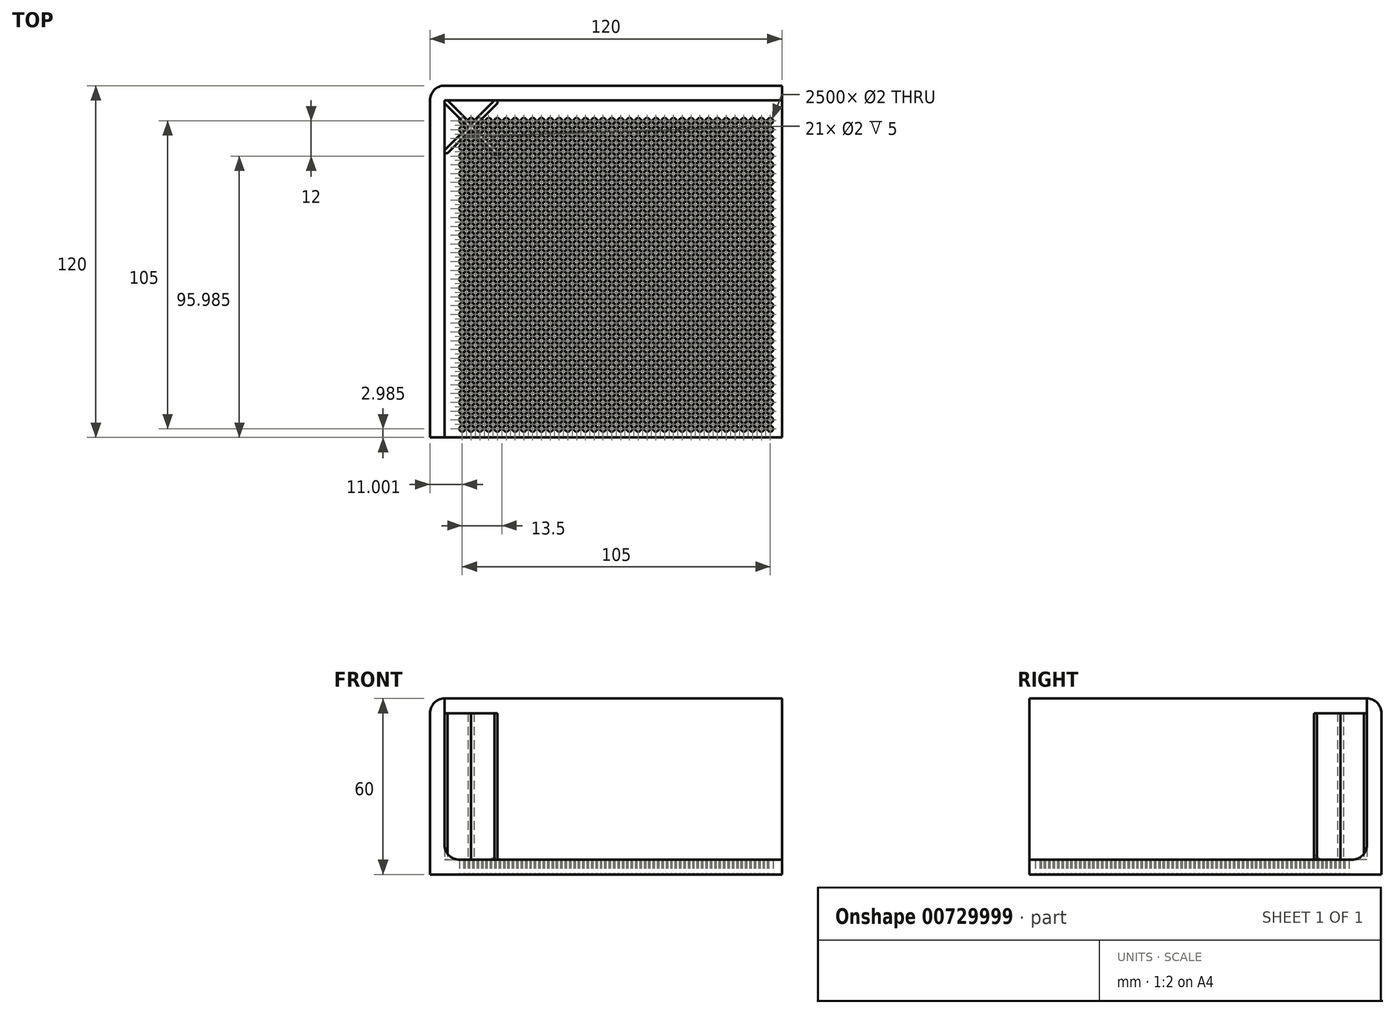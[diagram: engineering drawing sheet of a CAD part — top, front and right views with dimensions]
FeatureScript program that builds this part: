
annotation { "Feature Type Name" : "Feature", "Feature Type Description" : "" }
export const myFeature = defineFeature(function(context is Context, id is Id, definition is map)
    precondition{}
    {
        {
            var Q0;
            Q0=qCreatedBy(makeId("Top.planeOp"),FACE);
            var sketch = newSketch(context, id + "F0", { "sketchPlane" : qUnion([Q0])});
            skLineSegment(sketch, "E0.bottom", {"start": v(-61.1, 44.5) * mm, "end": v(58.9, 44.5) * mm});
            skLineSegment(sketch, "E0.top", {"start": v(-61.1, -75.5) * mm, "end": v(58.9, -75.5) * mm});
            skLineSegment(sketch, "E0.left", {"start": v(-61.1, 44.5) * mm, "end": v(-61.1, -75.5) * mm});
            skLineSegment(sketch, "E0.right", {"start": v(58.9, 44.5) * mm, "end": v(58.9, -75.5) * mm});
            skSolve(sketch);
        }
        {
            var Q0;
            Q0 = qSketchRegion(id + "F0", true);
            extrude(context, id + "F1", {"entities" : qUnion([Q0]), "depth" : 60 * mm, "offsetDistance" : 25 * mm});
        }
        {
            var Q0;
            Q0=makeQuery(id+"F1.opExtrude","CAP_FACE",FACE,{"disambiguationData":[OSD([sQuery(id+"F0.wireOp",EDGE,"E0.bottom"),sQuery(id+"F0.wireOp",EDGE,"E0.top"),sQuery(id+"F0.wireOp",EDGE,"E0.left"),sQuery(id+"F0.wireOp",EDGE,"E0.right")])],"isStart":false});
            var sketch = newSketch(context, id + "F2", { "sketchPlane" : qUnion([Q0])});
            skLineSegment(sketch, "E1.bottom", {"start": v(-56.1, 39.5) * mm, "end": v(58.9, 39.5) * mm});
            skLineSegment(sketch, "E1.top", {"start": v(-56.1, -75.5) * mm, "end": v(58.9, -75.5) * mm});
            skLineSegment(sketch, "E1.left", {"start": v(-56.1, 39.5) * mm, "end": v(-56.1, -75.5) * mm});
            skLineSegment(sketch, "E1.right", {"start": v(58.9, 39.5) * mm, "end": v(58.9, -75.5) * mm});
            skSolve(sketch);
        }
        {
            var Q0;
            Q0 = qSketchRegion(id + "F2", true);
            extrude(context, id + "F3", {"entities" : qUnion([Q0]), "operationType" : NewBodyOperationType.REMOVE, "oppositeDirection" : true, "depth" : 55 * mm, "offsetDistance" : 25 * mm});
        }
        {
            var Q0;
            Q0=makeQuery(id+"F3.boolean.opBoolean","COPY",FACE,{"derivedFrom":makeQuery(id+"F3.opExtrude","CAP_FACE",FACE,{"disambiguationData":[OSD([sQuery(id+"F2.wireOp",EDGE,"E1.bottom"),sQuery(id+"F2.wireOp",EDGE,"E1.top"),sQuery(id+"F2.wireOp",EDGE,"E1.left"),sQuery(id+"F2.wireOp",EDGE,"E1.right")])],"isStart":false})});
            var sketch = newSketch(context, id + "F4", { "sketchPlane" : qUnion([Q0])});
            skLineSegment(sketch, "E2.bottom", {"start": v(-56.1, 39.5) * mm, "end": v(-36.1, 39.5) * mm});
            skLineSegment(sketch, "E2.top", {"start": v(-56.1, 19.5) * mm, "end": v(-36.1, 19.5) * mm});
            skLineSegment(sketch, "E2.left", {"start": v(-56.1, 39.5) * mm, "end": v(-56.1, 19.5) * mm});
            skLineSegment(sketch, "E2.right", {"start": v(-36.1, 39.5) * mm, "end": v(-36.1, 19.5) * mm});
            skLineSegment(sketch, "E3.bottom", {"start": v(-56.1, 39.5) * mm, "end": v(-38.1, 39.5) * mm});
            skLineSegment(sketch, "E3.left", {"start": v(-56.1, 39.5) * mm, "end": v(-56.1, 21.52) * mm});
            skLineSegment(sketch, "E3.right", {"start": v(-38.1, 39.5) * mm, "end": v(-38.1, 21.5) * mm});
            skLineSegment(sketch, "E4", {"start": v(-56.1, 38.5) * mm, "end": v(-48.12, 30.51) * mm});
            skLineSegment(sketch, "E5", {"start": v(-48.12, 30.51) * mm, "end": v(-56.1, 22.52) * mm});
            skLineSegment(sketch, "E6", {"start": v(-55.1, 39.5) * mm, "end": v(-47.1, 31.5) * mm});
            skLineSegment(sketch, "E7", {"start": v(-47.1, 31.5) * mm, "end": v(-39.1, 39.5) * mm});
            skLineSegment(sketch, "E8", {"start": v(-38.1, 38.5) * mm, "end": v(-46.1, 30.5) * mm});
            skLineSegment(sketch, "E9", {"start": v(-46.1, 30.5) * mm, "end": v(-38.1, 22.5) * mm});
            skLineSegment(sketch, "E10", {"start": v(-39.1, 21.5) * mm, "end": v(-47.11, 29.51) * mm});
            skLineSegment(sketch, "E11", {"start": v(-47.11, 29.51) * mm, "end": v(-55.1, 21.52) * mm});
            skLineSegment(sketch, "E12", {"start": v(-56.1, 22.52) * mm, "end": v(-56.1, 21.52) * mm});
            skLineSegment(sketch, "E13", {"start": v(-56.1, 21.52) * mm, "end": v(-38.1, 21.5) * mm});
            skSolve(sketch);
        }
        {
            var Q0;
            Q0=makeQuery(id+"F4.imprint","IMPRINT",FACE,{"disambiguationData":[TD([[makeQuery(id+"F4.imprint","IMPRINT",EDGE,{"derivedFrom":sQuery(id+"F4.wireOp",EDGE,"E2.bottom")}),-1.0]])]});
            extrude(context, id + "F5", {"entities" : qUnion([Q0]), "operationType" : NewBodyOperationType.ADD, "depth" : 50 * mm, "offsetDistance" : 25 * mm});
        }
        {
            var Q0;
            {var subQ9=sQuery(id+"F4.wireOp",EDGE,"E4");Q0=makeQuery(id+"F4.imprint","IMPRINT",FACE,{"disambiguationData":[TD([[makeQuery(id+"F4.imprint","IMPRINT",EDGE,{"derivedFrom":subQ9}),1.0]])]});}
            extrude(context, id + "F6", {"entities" : qUnion([Q0]), "operationType" : NewBodyOperationType.ADD, "depth" : 50 * mm, "offsetDistance" : 25 * mm});
        }
        {
            var Q0;
            Q0=makeQuery(id+"F1.opExtrude","SWEPT_EDGE",EDGE,{"disambiguationData":[OSD([sQuery(id+"F0.wireOp",EDGE,"E0.bottom"),sQuery(id+"F0.wireOp",EDGE,"E0.left")])]});
            var Q1;
            Q1=makeQuery(id+"F1.opExtrude","CAP_EDGE",EDGE,{"disambiguationData":[OSD([sQuery(id+"F0.wireOp",EDGE,"E0.left")])],"isStart":false});
            var Q2;
            Q2=makeQuery(id+"F1.opExtrude","CAP_EDGE",EDGE,{"disambiguationData":[OSD([sQuery(id+"F0.wireOp",EDGE,"E0.bottom")])],"isStart":false});
            fillet(context, id + "F7", {"entities" : qUnion([Q0, Q1, Q2]), "radius" : 5 * mm, "tangentPropagation" : true, "allowEdgeOverflow" : false});
        }
        {
            var Q0;
            {var subQ0=sQuery(id+"F2.wireOp",EDGE,"E1.left");Q0=makeQuery(id+"F5.boolean.opBoolean","SPLIT",EDGE,{"disambiguationData":[TD([makeQuery(id+"F1.opExtrude","SWEPT_FACE",FACE,{"disambiguationData":[OSD([sQuery(id+"F0.wireOp",EDGE,"E0.top")])]})])],"derivedFrom":makeQuery(id+"F3.boolean.opBoolean","COPY",EDGE,{"derivedFrom":makeQuery(id+"F3.opExtrude","CAP_EDGE",EDGE,{"disambiguationData":[OSD([subQ0])],"isStart":false})})});}
            var Q1;
            Q1=makeQuery(id+"F5.opExtrude","CAP_EDGE",EDGE,{"disambiguationData":[OSD([sQuery(id+"F4.wireOp",EDGE,"E2.top")])],"isStart":true});
            var Q2;
            Q2=makeQuery(id+"F5.opExtrude","SWEPT_EDGE",EDGE,{"disambiguationData":[OSD([sQuery(id+"F2.wireOp",EDGE,"E1.left"),sQuery(id+"F4.wireOp",EDGE,"E2.top"),sQuery(id+"F4.wireOp",EDGE,"E2.left")])]});
            var Q3;
            Q3=makeQuery(id+"F5.opExtrude","SWEPT_EDGE",EDGE,{"disambiguationData":[OSD([sQuery(id+"F4.wireOp",EDGE,"E2.top"),sQuery(id+"F4.wireOp",EDGE,"E2.right")])]});
            var Q4;
            Q4=makeQuery(id+"F5.opExtrude","CAP_EDGE",EDGE,{"disambiguationData":[OSD([sQuery(id+"F4.wireOp",EDGE,"E2.right")])],"isStart":true});
            var Q5;
            Q5=makeQuery(id+"F5.opExtrude","SWEPT_EDGE",EDGE,{"disambiguationData":[OSD([sQuery(id+"F2.wireOp",EDGE,"E1.bottom"),sQuery(id+"F4.wireOp",EDGE,"E2.bottom"),sQuery(id+"F4.wireOp",EDGE,"E2.right")])]});
            var Q6;
            {var subQ0=sQuery(id+"F2.wireOp",EDGE,"E1.bottom");Q6=makeQuery(id+"F5.boolean.opBoolean","SPLIT",EDGE,{"disambiguationData":[TD([makeQuery(id+"F1.opExtrude","SWEPT_FACE",FACE,{"disambiguationData":[OSD([sQuery(id+"F0.wireOp",EDGE,"E0.right")])]})])],"derivedFrom":makeQuery(id+"F3.boolean.opBoolean","COPY",EDGE,{"derivedFrom":makeQuery(id+"F3.opExtrude","CAP_EDGE",EDGE,{"disambiguationData":[OSD([subQ0])],"isStart":false})})});}
            fillet(context, id + "F8", {"entities" : qUnion([Q0, Q1, Q2, Q3, Q4, Q5, Q6]), "radius" : 5 * mm, "tangentPropagation" : true, "allowEdgeOverflow" : false});
        }
        {
            var Q0;
            Q0=makeQuery(id+"F6.opExtrude","SWEPT_EDGE",EDGE,{"disambiguationData":[OSD([sQuery(id+"F4.wireOp",EDGE,"E3.left"),sQuery(id+"F4.wireOp",EDGE,"E4")])]});
            var Q1;
            Q1=makeQuery(id+"F6.opExtrude","SWEPT_EDGE",EDGE,{"disambiguationData":[OSD([sQuery(id+"F4.wireOp",EDGE,"E4"),sQuery(id+"F4.wireOp",EDGE,"E5")])]});
            var Q2;
            Q2=makeQuery(id+"F6.opExtrude","SWEPT_EDGE",EDGE,{"disambiguationData":[OSD([sQuery(id+"F4.wireOp",EDGE,"E3.left"),sQuery(id+"F4.wireOp",EDGE,"E5"),sQuery(id+"F4.wireOp",EDGE,"E12")])]});
            var Q3;
            Q3=makeQuery(id+"F6.opExtrude","SWEPT_EDGE",EDGE,{"disambiguationData":[OSD([sQuery(id+"F4.wireOp",EDGE,"E6"),sQuery(id+"F4.wireOp",EDGE,"E7")])]});
            var Q4;
            Q4=makeQuery(id+"F6.opExtrude","SWEPT_EDGE",EDGE,{"disambiguationData":[OSD([sQuery(id+"F4.wireOp",EDGE,"E3.bottom"),sQuery(id+"F4.wireOp",EDGE,"E6")])]});
            var Q5;
            Q5=makeQuery(id+"F6.opExtrude","SWEPT_EDGE",EDGE,{"disambiguationData":[OSD([sQuery(id+"F4.wireOp",EDGE,"E3.bottom"),sQuery(id+"F4.wireOp",EDGE,"E7")])]});
            var Q6;
            Q6=makeQuery(id+"F6.opExtrude","SWEPT_EDGE",EDGE,{"disambiguationData":[OSD([sQuery(id+"F4.wireOp",EDGE,"E8"),sQuery(id+"F4.wireOp",EDGE,"E9")])]});
            var Q7;
            Q7=makeQuery(id+"F6.opExtrude","SWEPT_EDGE",EDGE,{"disambiguationData":[OSD([sQuery(id+"F4.wireOp",EDGE,"E3.right"),sQuery(id+"F4.wireOp",EDGE,"E8")])]});
            var Q8;
            Q8=makeQuery(id+"F6.opExtrude","SWEPT_EDGE",EDGE,{"disambiguationData":[OSD([sQuery(id+"F4.wireOp",EDGE,"E3.right"),sQuery(id+"F4.wireOp",EDGE,"E9")])]});
            var Q9;
            Q9=makeQuery(id+"F6.opExtrude","SWEPT_EDGE",EDGE,{"disambiguationData":[OSD([sQuery(id+"F4.wireOp",EDGE,"E10"),sQuery(id+"F4.wireOp",EDGE,"E11")])]});
            var Q10;
            Q10=makeQuery(id+"F6.opExtrude","SWEPT_EDGE",EDGE,{"disambiguationData":[OSD([sQuery(id+"F4.wireOp",EDGE,"E3.top"),sQuery(id+"F4.wireOp",EDGE,"E10")])]});
            var Q11;
            Q11=makeQuery(id+"F6.opExtrude","SWEPT_EDGE",EDGE,{"disambiguationData":[OSD([sQuery(id+"F4.wireOp",EDGE,"E3.top"),sQuery(id+"F4.wireOp",EDGE,"E11")])]});
            var Q12;
            Q12=makeQuery(id+"F6.opExtrude","CAP_EDGE",EDGE,{"disambiguationData":[OSD([sQuery(id+"F4.wireOp",EDGE,"E11")])],"isStart":true});
            var Q13;
            Q13=makeQuery(id+"F5.opExtrude","CAP_EDGE",EDGE,{"disambiguationData":[OSD([sQuery(id+"F4.wireOp",EDGE,"E3.top")])],"isStart":true});
            var Q14;
            Q14=makeQuery(id+"F6.opExtrude","CAP_EDGE",EDGE,{"disambiguationData":[OSD([sQuery(id+"F4.wireOp",EDGE,"E10")])],"isStart":true});
            var Q15;
            Q15=makeQuery(id+"F6.opExtrude","CAP_EDGE",EDGE,{"disambiguationData":[OSD([sQuery(id+"F4.wireOp",EDGE,"E9")])],"isStart":true});
            var Q16;
            Q16=makeQuery(id+"F6.opExtrude","CAP_EDGE",EDGE,{"disambiguationData":[OSD([sQuery(id+"F4.wireOp",EDGE,"E8")])],"isStart":true});
            var Q17;
            Q17=makeQuery(id+"F5.opExtrude","CAP_EDGE",EDGE,{"disambiguationData":[OSD([sQuery(id+"F4.wireOp",EDGE,"E3.right")])],"isStart":true});
            var Q18;
            Q18=makeQuery(id+"F6.opExtrude","CAP_EDGE",EDGE,{"disambiguationData":[OSD([sQuery(id+"F4.wireOp",EDGE,"E7")])],"isStart":true});
            var Q19;
            {var subQ0=sQuery(id+"F2.wireOp",EDGE,"E1.bottom");var subQ1=sQuery(id+"F2.wireOp",EDGE,"E1.left");Q19=makeQuery(id+"F5.boolean.opBoolean","SPLIT",EDGE,{"disambiguationData":[TD([makeQuery(id+"F3.boolean.opBoolean","COPY",FACE,{"derivedFrom":makeQuery(id+"F3.opExtrude","SWEPT_FACE",FACE,{"disambiguationData":[OSD([subQ1])]})})])],"derivedFrom":makeQuery(id+"F3.boolean.opBoolean","COPY",EDGE,{"derivedFrom":makeQuery(id+"F3.opExtrude","CAP_EDGE",EDGE,{"disambiguationData":[OSD([subQ0])],"isStart":false})})});}
            var Q20;
            Q20=makeQuery(id+"F6.opExtrude","CAP_EDGE",EDGE,{"disambiguationData":[OSD([sQuery(id+"F4.wireOp",EDGE,"E6")])],"isStart":true});
            var Q21;
            {var subQ0=sQuery(id+"F2.wireOp",EDGE,"E1.bottom");var subQ1=sQuery(id+"F2.wireOp",EDGE,"E1.left");Q21=makeQuery(id+"F5.boolean.opBoolean","SPLIT",EDGE,{"disambiguationData":[TD([makeQuery(id+"F3.boolean.opBoolean","COPY",FACE,{"derivedFrom":makeQuery(id+"F3.opExtrude","SWEPT_FACE",FACE,{"disambiguationData":[OSD([subQ0])]})})])],"derivedFrom":makeQuery(id+"F3.boolean.opBoolean","COPY",EDGE,{"derivedFrom":makeQuery(id+"F3.opExtrude","CAP_EDGE",EDGE,{"disambiguationData":[OSD([subQ1])],"isStart":false})})});}
            var Q22;
            Q22=makeQuery(id+"F6.opExtrude","CAP_EDGE",EDGE,{"disambiguationData":[OSD([sQuery(id+"F4.wireOp",EDGE,"E4")])],"isStart":true});
            var Q23;
            Q23=makeQuery(id+"F6.opExtrude","CAP_EDGE",EDGE,{"disambiguationData":[OSD([sQuery(id+"F4.wireOp",EDGE,"E5")])],"isStart":true});
            var Q24;
            Q24=makeQuery(id+"F5.opExtrude","CAP_EDGE",EDGE,{"disambiguationData":[OSD([sQuery(id+"F4.wireOp",EDGE,"E13")])],"isStart":true});
            fillet(context, id + "F9", {"entities" : qUnion([Q0, Q1, Q2, Q3, Q4, Q5, Q6, Q7, Q8, Q9, Q10, Q11, Q12, Q13, Q14, Q15, Q16, Q17, Q18, Q19, Q20, Q21, Q22, Q23, Q24]), "radius" : 1 * mm, "tangentPropagation" : true, "allowEdgeOverflow" : false});
        }
        {
            var Q0;
            Q0=makeQuery(id+"F1.opExtrude","CAP_FACE",FACE,{"disambiguationData":[OSD([sQuery(id+"F0.wireOp",EDGE,"E0.bottom"),sQuery(id+"F0.wireOp",EDGE,"E0.top"),sQuery(id+"F0.wireOp",EDGE,"E0.left"),sQuery(id+"F0.wireOp",EDGE,"E0.right")])],"isStart":true});
            var sketch = newSketch(context, id + "F10", { "sketchPlane" : qUnion([Q0])});
            skLineSegment(sketch, "E14.top", {"start": v(-51.1, -34.5) * mm, "end": v(56.9, -34.5) * mm, "construction": true});
            skLineSegment(sketch, "E14.left", {"start": v(-51.1, 73.5) * mm, "end": v(-51.1, -34.5) * mm, "construction": true});
            skLineSegment(sketch, "E14.right", {"start": v(56.9, 73.5) * mm, "end": v(56.9, -34.5) * mm, "construction": true});
            skLineSegment(sketch, "E15", {"start": v(-51.1, 73.5) * mm, "end": v(56.9, 73.5) * mm, "construction": true});
            skLineSegment(sketch, "E16", {"start": v(-51.1, 72.5) * mm, "end": v(-50.1, 72.5) * mm, "construction": true});
            skLineSegment(sketch, "E17", {"start": v(-50.1, 72.5) * mm, "end": v(-50.1, 73.5) * mm, "construction": true});
            skCircle(sketch, "E18", {"center": v(-50.1, 72.5) * mm, "radius": 1 * mm});
            skLineSegment(sketch, "E19", {"start": v(-51.1, 71) * mm, "end": v(-48.6, 71) * mm, "construction": true});
            skLineSegment(sketch, "E20", {"start": v(-48.6, 71) * mm, "end": v(-48.6, 73.5) * mm, "construction": true});
            skCircle(sketch, "E21", {"center": v(-48.6, 71) * mm, "radius": 1 * mm});
            skCircle(sketch, "E22.1.0.0", {"center": v(-47.1, 72.5) * mm, "radius": 1 * mm});
            skCircle(sketch, "E22.2.0.0", {"center": v(-44.1, 72.5) * mm, "radius": 1 * mm});
            skCircle(sketch, "E22.3.0.0", {"center": v(-41.1, 72.5) * mm, "radius": 1 * mm});
            skCircle(sketch, "E22.4.0.0", {"center": v(-38.1, 72.5) * mm, "radius": 1 * mm});
            skCircle(sketch, "E22.5.0.0", {"center": v(-35.1, 72.5) * mm, "radius": 1 * mm});
            skCircle(sketch, "E22.6.0.0", {"center": v(-32.1, 72.5) * mm, "radius": 1 * mm});
            skCircle(sketch, "E22.7.0.0", {"center": v(-29.1, 72.5) * mm, "radius": 1 * mm});
            skCircle(sketch, "E22.8.0.0", {"center": v(-26.1, 72.5) * mm, "radius": 1 * mm});
            skCircle(sketch, "E22.9.0.0", {"center": v(-23.1, 72.5) * mm, "radius": 1 * mm});
            skCircle(sketch, "E22.10.0.0", {"center": v(-20.1, 72.5) * mm, "radius": 1 * mm});
            skCircle(sketch, "E22.11.0.0", {"center": v(-17.1, 72.5) * mm, "radius": 1 * mm});
            skCircle(sketch, "E22.12.0.0", {"center": v(-14.1, 72.5) * mm, "radius": 1 * mm});
            skCircle(sketch, "E22.13.0.0", {"center": v(-11.1, 72.5) * mm, "radius": 1 * mm});
            skCircle(sketch, "E22.14.0.0", {"center": v(-8.1, 72.5) * mm, "radius": 1 * mm});
            skCircle(sketch, "E22.15.0.0", {"center": v(-5.1, 72.5) * mm, "radius": 1 * mm});
            skCircle(sketch, "E22.16.0.0", {"center": v(-2.1, 72.5) * mm, "radius": 1 * mm});
            skCircle(sketch, "E22.17.0.0", {"center": v(0.9, 72.5) * mm, "radius": 1 * mm});
            skCircle(sketch, "E22.18.0.0", {"center": v(3.9, 72.5) * mm, "radius": 1 * mm});
            skCircle(sketch, "E22.19.0.0", {"center": v(6.9, 72.5) * mm, "radius": 1 * mm});
            skCircle(sketch, "E22.20.0.0", {"center": v(9.9, 72.5) * mm, "radius": 1 * mm});
            skCircle(sketch, "E22.21.0.0", {"center": v(12.9, 72.5) * mm, "radius": 1 * mm});
            skCircle(sketch, "E22.22.0.0", {"center": v(15.9, 72.5) * mm, "radius": 1 * mm});
            skCircle(sketch, "E22.23.0.0", {"center": v(18.9, 72.5) * mm, "radius": 1 * mm});
            skCircle(sketch, "E22.24.0.0", {"center": v(21.9, 72.5) * mm, "radius": 1 * mm});
            skCircle(sketch, "E22.25.0.0", {"center": v(24.9, 72.5) * mm, "radius": 1 * mm});
            skCircle(sketch, "E22.26.0.0", {"center": v(27.9, 72.5) * mm, "radius": 1 * mm});
            skCircle(sketch, "E22.27.0.0", {"center": v(30.9, 72.5) * mm, "radius": 1 * mm});
            skCircle(sketch, "E22.28.0.0", {"center": v(33.9, 72.5) * mm, "radius": 1 * mm});
            skCircle(sketch, "E22.29.0.0", {"center": v(36.9, 72.5) * mm, "radius": 1 * mm});
            skCircle(sketch, "E22.30.0.0", {"center": v(39.9, 72.5) * mm, "radius": 1 * mm});
            skCircle(sketch, "E22.31.0.0", {"center": v(42.9, 72.5) * mm, "radius": 1 * mm});
            skCircle(sketch, "E22.32.0.0", {"center": v(45.9, 72.5) * mm, "radius": 1 * mm});
            skCircle(sketch, "E22.33.0.0", {"center": v(48.9, 72.5) * mm, "radius": 1 * mm});
            skCircle(sketch, "E22.34.0.0", {"center": v(51.9, 72.5) * mm, "radius": 1 * mm});
            skCircle(sketch, "E22.35.0.0", {"center": v(54.9, 72.5) * mm, "radius": 1 * mm});
            skLineSegment(sketch, "E22.direction1", {"start": v(-50.1, 72.5) * mm, "end": v(-47.1, 72.5) * mm, "construction": true});
            skCircle(sketch, "E23.1.0.0", {"center": v(-45.6, 71) * mm, "radius": 1 * mm});
            skCircle(sketch, "E23.2.0.0", {"center": v(-42.6, 71) * mm, "radius": 1 * mm});
            skCircle(sketch, "E23.3.0.0", {"center": v(-39.6, 71) * mm, "radius": 1 * mm});
            skCircle(sketch, "E23.4.0.0", {"center": v(-36.6, 71) * mm, "radius": 1 * mm});
            skCircle(sketch, "E23.5.0.0", {"center": v(-33.6, 71) * mm, "radius": 1 * mm});
            skCircle(sketch, "E23.6.0.0", {"center": v(-30.6, 71) * mm, "radius": 1 * mm});
            skCircle(sketch, "E23.7.0.0", {"center": v(-27.6, 71) * mm, "radius": 1 * mm});
            skCircle(sketch, "E23.8.0.0", {"center": v(-24.6, 71) * mm, "radius": 1 * mm});
            skCircle(sketch, "E23.9.0.0", {"center": v(-21.6, 71) * mm, "radius": 1 * mm});
            skCircle(sketch, "E23.10.0.0", {"center": v(-18.6, 71) * mm, "radius": 1 * mm});
            skCircle(sketch, "E23.11.0.0", {"center": v(-15.6, 71) * mm, "radius": 1 * mm});
            skCircle(sketch, "E23.12.0.0", {"center": v(-12.6, 71) * mm, "radius": 1 * mm});
            skCircle(sketch, "E23.13.0.0", {"center": v(-9.6, 71) * mm, "radius": 1 * mm});
            skCircle(sketch, "E23.14.0.0", {"center": v(-6.6, 71) * mm, "radius": 1 * mm});
            skCircle(sketch, "E23.15.0.0", {"center": v(-3.6, 71) * mm, "radius": 1 * mm});
            skCircle(sketch, "E23.16.0.0", {"center": v(-0.6, 71) * mm, "radius": 1 * mm});
            skCircle(sketch, "E23.17.0.0", {"center": v(2.4, 71) * mm, "radius": 1 * mm});
            skCircle(sketch, "E23.18.0.0", {"center": v(5.4, 71) * mm, "radius": 1 * mm});
            skCircle(sketch, "E23.19.0.0", {"center": v(8.4, 71) * mm, "radius": 1 * mm});
            skCircle(sketch, "E23.20.0.0", {"center": v(11.4, 71) * mm, "radius": 1 * mm});
            skCircle(sketch, "E23.21.0.0", {"center": v(14.4, 71) * mm, "radius": 1 * mm});
            skCircle(sketch, "E23.22.0.0", {"center": v(17.4, 71) * mm, "radius": 1 * mm});
            skCircle(sketch, "E23.23.0.0", {"center": v(20.4, 71) * mm, "radius": 1 * mm});
            skCircle(sketch, "E23.24.0.0", {"center": v(23.4, 71) * mm, "radius": 1 * mm});
            skCircle(sketch, "E23.25.0.0", {"center": v(26.4, 71) * mm, "radius": 1 * mm});
            skCircle(sketch, "E23.26.0.0", {"center": v(29.4, 71) * mm, "radius": 1 * mm});
            skCircle(sketch, "E23.27.0.0", {"center": v(32.4, 71) * mm, "radius": 1 * mm});
            skCircle(sketch, "E23.28.0.0", {"center": v(35.4, 71) * mm, "radius": 1 * mm});
            skCircle(sketch, "E23.29.0.0", {"center": v(38.4, 71) * mm, "radius": 1 * mm});
            skCircle(sketch, "E23.30.0.0", {"center": v(41.4, 71) * mm, "radius": 1 * mm});
            skCircle(sketch, "E23.31.0.0", {"center": v(44.4, 71) * mm, "radius": 1 * mm});
            skCircle(sketch, "E23.32.0.0", {"center": v(47.4, 71) * mm, "radius": 1 * mm});
            skCircle(sketch, "E23.33.0.0", {"center": v(50.4, 71) * mm, "radius": 1 * mm});
            skCircle(sketch, "E23.34.0.0", {"center": v(53.4, 71) * mm, "radius": 1 * mm});
            skLineSegment(sketch, "E23.direction1", {"start": v(-48.6, 71) * mm, "end": v(-45.6, 71) * mm, "construction": true});
            skCircle(sketch, "E24.1.0.0", {"center": v(27.9, 69.5) * mm, "radius": 1 * mm});
            skCircle(sketch, "E24.1.0.1", {"center": v(-32.1, 69.5) * mm, "radius": 1 * mm});
            skCircle(sketch, "E24.1.0.2", {"center": v(36.9, 69.5) * mm, "radius": 1 * mm});
            skCircle(sketch, "E24.1.0.3", {"center": v(3.9, 69.5) * mm, "radius": 1 * mm});
            skCircle(sketch, "E24.1.0.4", {"center": v(54.9, 69.5) * mm, "radius": 1 * mm});
            skCircle(sketch, "E24.1.0.5", {"center": v(53.4, 68) * mm, "radius": 1 * mm});
            skCircle(sketch, "E24.1.0.6", {"center": v(29.4, 68) * mm, "radius": 1 * mm});
            skCircle(sketch, "E24.1.0.7", {"center": v(2.4, 68) * mm, "radius": 1 * mm});
            skCircle(sketch, "E24.1.0.9", {"center": v(18.9, 69.5) * mm, "radius": 1 * mm});
            skCircle(sketch, "E24.1.0.10", {"center": v(-30.6, 68) * mm, "radius": 1 * mm});
            skCircle(sketch, "E24.1.0.12", {"center": v(-44.1, 69.5) * mm, "radius": 1 * mm});
            skCircle(sketch, "E24.1.0.13", {"center": v(30.9, 69.5) * mm, "radius": 1 * mm});
            skCircle(sketch, "E24.1.0.14", {"center": v(-9.6, 68) * mm, "radius": 1 * mm});
            skCircle(sketch, "E24.1.0.16", {"center": v(-14.1, 69.5) * mm, "radius": 1 * mm});
            skCircle(sketch, "E24.1.0.17", {"center": v(-2.1, 69.5) * mm, "radius": 1 * mm});
            skCircle(sketch, "E24.1.0.18", {"center": v(9.9, 69.5) * mm, "radius": 1 * mm});
            skCircle(sketch, "E24.1.0.19", {"center": v(24.9, 69.5) * mm, "radius": 1 * mm});
            skCircle(sketch, "E24.1.0.20", {"center": v(5.4, 68) * mm, "radius": 1 * mm});
            skCircle(sketch, "E24.1.0.21", {"center": v(-23.1, 69.5) * mm, "radius": 1 * mm});
            skCircle(sketch, "E24.1.0.22", {"center": v(-5.1, 69.5) * mm, "radius": 1 * mm});
            skCircle(sketch, "E24.1.0.23", {"center": v(23.4, 68) * mm, "radius": 1 * mm});
            skCircle(sketch, "E24.1.0.24", {"center": v(42.9, 69.5) * mm, "radius": 1 * mm});
            skCircle(sketch, "E24.1.0.25", {"center": v(0.9, 69.5) * mm, "radius": 1 * mm});
            skCircle(sketch, "E24.1.0.26", {"center": v(-36.6, 68) * mm, "radius": 1 * mm});
            skCircle(sketch, "E24.1.0.27", {"center": v(41.4, 68) * mm, "radius": 1 * mm});
            skCircle(sketch, "E24.1.0.28", {"center": v(-12.6, 68) * mm, "radius": 1 * mm});
            skCircle(sketch, "E24.1.0.29", {"center": v(-26.1, 69.5) * mm, "radius": 1 * mm});
            skCircle(sketch, "E24.1.0.30", {"center": v(-8.1, 69.5) * mm, "radius": 1 * mm});
            skCircle(sketch, "E24.1.0.31", {"center": v(-27.6, 68) * mm, "radius": 1 * mm});
            skCircle(sketch, "E24.1.0.32", {"center": v(-29.1, 69.5) * mm, "radius": 1 * mm});
            skCircle(sketch, "E24.1.0.33", {"center": v(15.9, 69.5) * mm, "radius": 1 * mm});
            skCircle(sketch, "E24.1.0.34", {"center": v(-3.6, 68) * mm, "radius": 1 * mm});
            skCircle(sketch, "E24.1.0.35", {"center": v(-11.1, 69.5) * mm, "radius": 1 * mm});
            skCircle(sketch, "E24.1.0.36", {"center": v(44.4, 68) * mm, "radius": 1 * mm});
            skCircle(sketch, "E24.1.0.37", {"center": v(8.4, 68) * mm, "radius": 1 * mm});
            skCircle(sketch, "E24.1.0.38", {"center": v(33.9, 69.5) * mm, "radius": 1 * mm});
            skCircle(sketch, "E24.1.0.39", {"center": v(12.9, 69.5) * mm, "radius": 1 * mm});
            skCircle(sketch, "E24.1.0.40", {"center": v(-38.1, 69.5) * mm, "radius": 1 * mm});
            skCircle(sketch, "E24.1.0.41", {"center": v(-18.6, 68) * mm, "radius": 1 * mm});
            skCircle(sketch, "E24.1.0.42", {"center": v(-17.1, 69.5) * mm, "radius": 1 * mm});
            skCircle(sketch, "E24.1.0.43", {"center": v(48.9, 69.5) * mm, "radius": 1 * mm});
            skCircle(sketch, "E24.1.0.44", {"center": v(35.4, 68) * mm, "radius": 1 * mm});
            skCircle(sketch, "E24.1.0.45", {"center": v(11.4, 68) * mm, "radius": 1 * mm});
            skCircle(sketch, "E24.1.0.46", {"center": v(-24.6, 68) * mm, "radius": 1 * mm});
            skCircle(sketch, "E24.1.0.47", {"center": v(21.9, 69.5) * mm, "radius": 1 * mm});
            skCircle(sketch, "E24.1.0.48", {"center": v(50.4, 68) * mm, "radius": 1 * mm});
            skCircle(sketch, "E24.1.0.49", {"center": v(26.4, 68) * mm, "radius": 1 * mm});
            skCircle(sketch, "E24.1.0.50", {"center": v(20.4, 68) * mm, "radius": 1 * mm});
            skCircle(sketch, "E24.1.0.51", {"center": v(39.9, 69.5) * mm, "radius": 1 * mm});
            skCircle(sketch, "E24.1.0.52", {"center": v(-0.6, 68) * mm, "radius": 1 * mm});
            skCircle(sketch, "E24.1.0.53", {"center": v(47.4, 68) * mm, "radius": 1 * mm});
            skCircle(sketch, "E24.1.0.55", {"center": v(-39.6, 68) * mm, "radius": 1 * mm});
            skCircle(sketch, "E24.1.0.56", {"center": v(38.4, 68) * mm, "radius": 1 * mm});
            skCircle(sketch, "E24.1.0.57", {"center": v(-35.1, 69.5) * mm, "radius": 1 * mm});
            skCircle(sketch, "E24.1.0.58", {"center": v(17.4, 68) * mm, "radius": 1 * mm});
            skCircle(sketch, "E24.1.0.59", {"center": v(51.9, 69.5) * mm, "radius": 1 * mm});
            skCircle(sketch, "E24.1.0.60", {"center": v(-33.6, 68) * mm, "radius": 1 * mm});
            skCircle(sketch, "E24.1.0.62", {"center": v(-15.6, 68) * mm, "radius": 1 * mm});
            skCircle(sketch, "E24.1.0.63", {"center": v(14.4, 68) * mm, "radius": 1 * mm});
            skCircle(sketch, "E24.1.0.64", {"center": v(45.9, 69.5) * mm, "radius": 1 * mm});
            skCircle(sketch, "E24.1.0.65", {"center": v(-6.6, 68) * mm, "radius": 1 * mm});
            skCircle(sketch, "E24.1.0.66", {"center": v(32.4, 68) * mm, "radius": 1 * mm});
            skCircle(sketch, "E24.1.0.67", {"center": v(-21.6, 68) * mm, "radius": 1 * mm});
            skCircle(sketch, "E24.1.0.68", {"center": v(6.9, 69.5) * mm, "radius": 1 * mm});
            skCircle(sketch, "E24.1.0.69", {"center": v(-20.1, 69.5) * mm, "radius": 1 * mm});
            skCircle(sketch, "E24.1.0.70", {"center": v(-41.1, 69.5) * mm, "radius": 1 * mm});
            skCircle(sketch, "E24.1.0.72", {"center": v(-47.1, 69.5) * mm, "radius": 1 * mm});
            skCircle(sketch, "E24.1.0.73", {"center": v(-42.6, 68) * mm, "radius": 1 * mm});
            skCircle(sketch, "E24.1.0.74", {"center": v(-45.6, 68) * mm, "radius": 1 * mm});
            skCircle(sketch, "E24.1.0.75", {"center": v(-48.6, 68) * mm, "radius": 1 * mm});
            skLineSegment(sketch, "E24.1.0.76", {"start": v(-50.1, 69.5) * mm, "end": v(-50.1, 70.5) * mm, "construction": true});
            skCircle(sketch, "E24.1.0.77", {"center": v(-50.1, 69.5) * mm, "radius": 1 * mm});
            skLineSegment(sketch, "E24.1.0.78", {"start": v(-51.1, 69.5) * mm, "end": v(-50.1, 69.5) * mm, "construction": true});
            skLineSegment(sketch, "E24.1.0.79", {"start": v(-51.1, 68) * mm, "end": v(-48.6, 68) * mm, "construction": true});
            skLineSegment(sketch, "E24.1.0.80", {"start": v(-48.6, 68) * mm, "end": v(-48.6, 70.5) * mm, "construction": true});
            skCircle(sketch, "E24.2.0.0", {"center": v(27.9, 66.5) * mm, "radius": 1 * mm});
            skCircle(sketch, "E24.2.0.1", {"center": v(-32.1, 66.5) * mm, "radius": 1 * mm});
            skCircle(sketch, "E24.2.0.2", {"center": v(36.9, 66.5) * mm, "radius": 1 * mm});
            skCircle(sketch, "E24.2.0.3", {"center": v(3.9, 66.5) * mm, "radius": 1 * mm});
            skCircle(sketch, "E24.2.0.4", {"center": v(54.9, 66.5) * mm, "radius": 1 * mm});
            skCircle(sketch, "E24.2.0.5", {"center": v(53.4, 65) * mm, "radius": 1 * mm});
            skCircle(sketch, "E24.2.0.6", {"center": v(29.4, 65) * mm, "radius": 1 * mm});
            skCircle(sketch, "E24.2.0.7", {"center": v(2.4, 65) * mm, "radius": 1 * mm});
            skCircle(sketch, "E24.2.0.9", {"center": v(18.9, 66.5) * mm, "radius": 1 * mm});
            skCircle(sketch, "E24.2.0.10", {"center": v(-30.6, 65) * mm, "radius": 1 * mm});
            skCircle(sketch, "E24.2.0.12", {"center": v(-44.1, 66.5) * mm, "radius": 1 * mm});
            skCircle(sketch, "E24.2.0.13", {"center": v(30.9, 66.5) * mm, "radius": 1 * mm});
            skCircle(sketch, "E24.2.0.14", {"center": v(-9.6, 65) * mm, "radius": 1 * mm});
            skCircle(sketch, "E24.2.0.16", {"center": v(-14.1, 66.5) * mm, "radius": 1 * mm});
            skCircle(sketch, "E24.2.0.17", {"center": v(-2.1, 66.5) * mm, "radius": 1 * mm});
            skCircle(sketch, "E24.2.0.18", {"center": v(9.9, 66.5) * mm, "radius": 1 * mm});
            skCircle(sketch, "E24.2.0.19", {"center": v(24.9, 66.5) * mm, "radius": 1 * mm});
            skCircle(sketch, "E24.2.0.20", {"center": v(5.4, 65) * mm, "radius": 1 * mm});
            skCircle(sketch, "E24.2.0.21", {"center": v(-23.1, 66.5) * mm, "radius": 1 * mm});
            skCircle(sketch, "E24.2.0.22", {"center": v(-5.1, 66.5) * mm, "radius": 1 * mm});
            skCircle(sketch, "E24.2.0.23", {"center": v(23.4, 65) * mm, "radius": 1 * mm});
            skCircle(sketch, "E24.2.0.24", {"center": v(42.9, 66.5) * mm, "radius": 1 * mm});
            skCircle(sketch, "E24.2.0.25", {"center": v(0.9, 66.5) * mm, "radius": 1 * mm});
            skCircle(sketch, "E24.2.0.26", {"center": v(-36.6, 65) * mm, "radius": 1 * mm});
            skCircle(sketch, "E24.2.0.27", {"center": v(41.4, 65) * mm, "radius": 1 * mm});
            skCircle(sketch, "E24.2.0.28", {"center": v(-12.6, 65) * mm, "radius": 1 * mm});
            skCircle(sketch, "E24.2.0.29", {"center": v(-26.1, 66.5) * mm, "radius": 1 * mm});
            skCircle(sketch, "E24.2.0.30", {"center": v(-8.1, 66.5) * mm, "radius": 1 * mm});
            skCircle(sketch, "E24.2.0.31", {"center": v(-27.6, 65) * mm, "radius": 1 * mm});
            skCircle(sketch, "E24.2.0.32", {"center": v(-29.1, 66.5) * mm, "radius": 1 * mm});
            skCircle(sketch, "E24.2.0.33", {"center": v(15.9, 66.5) * mm, "radius": 1 * mm});
            skCircle(sketch, "E24.2.0.34", {"center": v(-3.6, 65) * mm, "radius": 1 * mm});
            skCircle(sketch, "E24.2.0.35", {"center": v(-11.1, 66.5) * mm, "radius": 1 * mm});
            skCircle(sketch, "E24.2.0.36", {"center": v(44.4, 65) * mm, "radius": 1 * mm});
            skCircle(sketch, "E24.2.0.37", {"center": v(8.4, 65) * mm, "radius": 1 * mm});
            skCircle(sketch, "E24.2.0.38", {"center": v(33.9, 66.5) * mm, "radius": 1 * mm});
            skCircle(sketch, "E24.2.0.39", {"center": v(12.9, 66.5) * mm, "radius": 1 * mm});
            skCircle(sketch, "E24.2.0.40", {"center": v(-38.1, 66.5) * mm, "radius": 1 * mm});
            skCircle(sketch, "E24.2.0.41", {"center": v(-18.6, 65) * mm, "radius": 1 * mm});
            skCircle(sketch, "E24.2.0.42", {"center": v(-17.1, 66.5) * mm, "radius": 1 * mm});
            skCircle(sketch, "E24.2.0.43", {"center": v(48.9, 66.5) * mm, "radius": 1 * mm});
            skCircle(sketch, "E24.2.0.44", {"center": v(35.4, 65) * mm, "radius": 1 * mm});
            skCircle(sketch, "E24.2.0.45", {"center": v(11.4, 65) * mm, "radius": 1 * mm});
            skCircle(sketch, "E24.2.0.46", {"center": v(-24.6, 65) * mm, "radius": 1 * mm});
            skCircle(sketch, "E24.2.0.47", {"center": v(21.9, 66.5) * mm, "radius": 1 * mm});
            skCircle(sketch, "E24.2.0.48", {"center": v(50.4, 65) * mm, "radius": 1 * mm});
            skCircle(sketch, "E24.2.0.49", {"center": v(26.4, 65) * mm, "radius": 1 * mm});
            skCircle(sketch, "E24.2.0.50", {"center": v(20.4, 65) * mm, "radius": 1 * mm});
            skCircle(sketch, "E24.2.0.51", {"center": v(39.9, 66.5) * mm, "radius": 1 * mm});
            skCircle(sketch, "E24.2.0.52", {"center": v(-0.6, 65) * mm, "radius": 1 * mm});
            skCircle(sketch, "E24.2.0.53", {"center": v(47.4, 65) * mm, "radius": 1 * mm});
            skCircle(sketch, "E24.2.0.55", {"center": v(-39.6, 65) * mm, "radius": 1 * mm});
            skCircle(sketch, "E24.2.0.56", {"center": v(38.4, 65) * mm, "radius": 1 * mm});
            skCircle(sketch, "E24.2.0.57", {"center": v(-35.1, 66.5) * mm, "radius": 1 * mm});
            skCircle(sketch, "E24.2.0.58", {"center": v(17.4, 65) * mm, "radius": 1 * mm});
            skCircle(sketch, "E24.2.0.59", {"center": v(51.9, 66.5) * mm, "radius": 1 * mm});
            skCircle(sketch, "E24.2.0.60", {"center": v(-33.6, 65) * mm, "radius": 1 * mm});
            skCircle(sketch, "E24.2.0.62", {"center": v(-15.6, 65) * mm, "radius": 1 * mm});
            skCircle(sketch, "E24.2.0.63", {"center": v(14.4, 65) * mm, "radius": 1 * mm});
            skCircle(sketch, "E24.2.0.64", {"center": v(45.9, 66.5) * mm, "radius": 1 * mm});
            skCircle(sketch, "E24.2.0.65", {"center": v(-6.6, 65) * mm, "radius": 1 * mm});
            skCircle(sketch, "E24.2.0.66", {"center": v(32.4, 65) * mm, "radius": 1 * mm});
            skCircle(sketch, "E24.2.0.67", {"center": v(-21.6, 65) * mm, "radius": 1 * mm});
            skCircle(sketch, "E24.2.0.68", {"center": v(6.9, 66.5) * mm, "radius": 1 * mm});
            skCircle(sketch, "E24.2.0.69", {"center": v(-20.1, 66.5) * mm, "radius": 1 * mm});
            skCircle(sketch, "E24.2.0.70", {"center": v(-41.1, 66.5) * mm, "radius": 1 * mm});
            skCircle(sketch, "E24.2.0.72", {"center": v(-47.1, 66.5) * mm, "radius": 1 * mm});
            skCircle(sketch, "E24.2.0.73", {"center": v(-42.6, 65) * mm, "radius": 1 * mm});
            skCircle(sketch, "E24.2.0.74", {"center": v(-45.6, 65) * mm, "radius": 1 * mm});
            skCircle(sketch, "E24.2.0.75", {"center": v(-48.6, 65) * mm, "radius": 1 * mm});
            skLineSegment(sketch, "E24.2.0.76", {"start": v(-50.1, 66.5) * mm, "end": v(-50.1, 67.5) * mm, "construction": true});
            skCircle(sketch, "E24.2.0.77", {"center": v(-50.1, 66.5) * mm, "radius": 1 * mm});
            skLineSegment(sketch, "E24.2.0.78", {"start": v(-51.1, 66.5) * mm, "end": v(-50.1, 66.5) * mm, "construction": true});
            skLineSegment(sketch, "E24.2.0.79", {"start": v(-51.1, 65) * mm, "end": v(-48.6, 65) * mm, "construction": true});
            skLineSegment(sketch, "E24.2.0.80", {"start": v(-48.6, 65) * mm, "end": v(-48.6, 67.5) * mm, "construction": true});
            skLineSegment(sketch, "E24.direction1", {"start": v(-51.1, 71) * mm, "end": v(-51.1, 68) * mm, "construction": true});
            skCircle(sketch, "E25.0.3.0", {"center": v(27.9, 63.5) * mm, "radius": 1 * mm});
            skCircle(sketch, "E25.2.3.0", {"center": v(-32.1, 63.5) * mm, "radius": 1 * mm});
            skCircle(sketch, "E25.4.3.0", {"center": v(36.9, 63.5) * mm, "radius": 1 * mm});
            skCircle(sketch, "E25.6.3.0", {"center": v(3.9, 63.5) * mm, "radius": 1 * mm});
            skCircle(sketch, "E25.8.3.0", {"center": v(54.9, 63.5) * mm, "radius": 1 * mm});
            skCircle(sketch, "E25.10.3.0", {"center": v(53.4, 62) * mm, "radius": 1 * mm});
            skCircle(sketch, "E25.12.3.0", {"center": v(29.4, 62) * mm, "radius": 1 * mm});
            skCircle(sketch, "E25.14.3.0", {"center": v(2.4, 62) * mm, "radius": 1 * mm});
            skCircle(sketch, "E25.18.3.0", {"center": v(18.9, 63.5) * mm, "radius": 1 * mm});
            skCircle(sketch, "E25.20.3.0", {"center": v(-30.6, 62) * mm, "radius": 1 * mm});
            skCircle(sketch, "E25.24.3.0", {"center": v(-44.1, 63.5) * mm, "radius": 1 * mm});
            skCircle(sketch, "E25.26.3.0", {"center": v(30.9, 63.5) * mm, "radius": 1 * mm});
            skCircle(sketch, "E25.28.3.0", {"center": v(-9.6, 62) * mm, "radius": 1 * mm});
            skCircle(sketch, "E25.32.3.0", {"center": v(-14.1, 63.5) * mm, "radius": 1 * mm});
            skCircle(sketch, "E25.34.3.0", {"center": v(-2.1, 63.5) * mm, "radius": 1 * mm});
            skCircle(sketch, "E25.36.3.0", {"center": v(9.9, 63.5) * mm, "radius": 1 * mm});
            skCircle(sketch, "E25.38.3.0", {"center": v(24.9, 63.5) * mm, "radius": 1 * mm});
            skCircle(sketch, "E25.40.3.0", {"center": v(5.4, 62) * mm, "radius": 1 * mm});
            skCircle(sketch, "E25.42.3.0", {"center": v(-23.1, 63.5) * mm, "radius": 1 * mm});
            skCircle(sketch, "E25.44.3.0", {"center": v(-5.1, 63.5) * mm, "radius": 1 * mm});
            skCircle(sketch, "E25.46.3.0", {"center": v(23.4, 62) * mm, "radius": 1 * mm});
            skCircle(sketch, "E25.48.3.0", {"center": v(42.9, 63.5) * mm, "radius": 1 * mm});
            skCircle(sketch, "E25.50.3.0", {"center": v(0.9, 63.5) * mm, "radius": 1 * mm});
            skCircle(sketch, "E25.52.3.0", {"center": v(-36.6, 62) * mm, "radius": 1 * mm});
            skCircle(sketch, "E25.54.3.0", {"center": v(41.4, 62) * mm, "radius": 1 * mm});
            skCircle(sketch, "E25.56.3.0", {"center": v(-12.6, 62) * mm, "radius": 1 * mm});
            skCircle(sketch, "E25.58.3.0", {"center": v(-26.1, 63.5) * mm, "radius": 1 * mm});
            skCircle(sketch, "E25.60.3.0", {"center": v(-8.1, 63.5) * mm, "radius": 1 * mm});
            skCircle(sketch, "E25.62.3.0", {"center": v(-27.6, 62) * mm, "radius": 1 * mm});
            skCircle(sketch, "E25.64.3.0", {"center": v(-29.1, 63.5) * mm, "radius": 1 * mm});
            skCircle(sketch, "E25.66.3.0", {"center": v(15.9, 63.5) * mm, "radius": 1 * mm});
            skCircle(sketch, "E25.68.3.0", {"center": v(-3.6, 62) * mm, "radius": 1 * mm});
            skCircle(sketch, "E25.70.3.0", {"center": v(-11.1, 63.5) * mm, "radius": 1 * mm});
            skCircle(sketch, "E25.72.3.0", {"center": v(44.4, 62) * mm, "radius": 1 * mm});
            skCircle(sketch, "E25.74.3.0", {"center": v(8.4, 62) * mm, "radius": 1 * mm});
            skCircle(sketch, "E25.76.3.0", {"center": v(33.9, 63.5) * mm, "radius": 1 * mm});
            skCircle(sketch, "E25.78.3.0", {"center": v(12.9, 63.5) * mm, "radius": 1 * mm});
            skCircle(sketch, "E25.80.3.0", {"center": v(-38.1, 63.5) * mm, "radius": 1 * mm});
            skCircle(sketch, "E25.82.3.0", {"center": v(-18.6, 62) * mm, "radius": 1 * mm});
            skCircle(sketch, "E25.84.3.0", {"center": v(-17.1, 63.5) * mm, "radius": 1 * mm});
            skCircle(sketch, "E25.86.3.0", {"center": v(48.9, 63.5) * mm, "radius": 1 * mm});
            skCircle(sketch, "E25.88.3.0", {"center": v(35.4, 62) * mm, "radius": 1 * mm});
            skCircle(sketch, "E25.90.3.0", {"center": v(11.4, 62) * mm, "radius": 1 * mm});
            skCircle(sketch, "E25.92.3.0", {"center": v(-24.6, 62) * mm, "radius": 1 * mm});
            skCircle(sketch, "E25.94.3.0", {"center": v(21.9, 63.5) * mm, "radius": 1 * mm});
            skCircle(sketch, "E25.96.3.0", {"center": v(50.4, 62) * mm, "radius": 1 * mm});
            skCircle(sketch, "E25.98.3.0", {"center": v(26.4, 62) * mm, "radius": 1 * mm});
            skCircle(sketch, "E25.100.3.0", {"center": v(20.4, 62) * mm, "radius": 1 * mm});
            skCircle(sketch, "E25.102.3.0", {"center": v(39.9, 63.5) * mm, "radius": 1 * mm});
            skCircle(sketch, "E25.104.3.0", {"center": v(-0.6, 62) * mm, "radius": 1 * mm});
            skCircle(sketch, "E25.106.3.0", {"center": v(47.4, 62) * mm, "radius": 1 * mm});
            skCircle(sketch, "E25.110.3.0", {"center": v(-39.6, 62) * mm, "radius": 1 * mm});
            skCircle(sketch, "E25.112.3.0", {"center": v(38.4, 62) * mm, "radius": 1 * mm});
            skCircle(sketch, "E25.114.3.0", {"center": v(-35.1, 63.5) * mm, "radius": 1 * mm});
            skCircle(sketch, "E25.116.3.0", {"center": v(17.4, 62) * mm, "radius": 1 * mm});
            skCircle(sketch, "E25.118.3.0", {"center": v(51.9, 63.5) * mm, "radius": 1 * mm});
            skCircle(sketch, "E25.120.3.0", {"center": v(-33.6, 62) * mm, "radius": 1 * mm});
            skCircle(sketch, "E25.124.3.0", {"center": v(-15.6, 62) * mm, "radius": 1 * mm});
            skCircle(sketch, "E25.126.3.0", {"center": v(14.4, 62) * mm, "radius": 1 * mm});
            skCircle(sketch, "E25.128.3.0", {"center": v(45.9, 63.5) * mm, "radius": 1 * mm});
            skCircle(sketch, "E25.130.3.0", {"center": v(-6.6, 62) * mm, "radius": 1 * mm});
            skCircle(sketch, "E25.132.3.0", {"center": v(32.4, 62) * mm, "radius": 1 * mm});
            skCircle(sketch, "E25.134.3.0", {"center": v(-21.6, 62) * mm, "radius": 1 * mm});
            skCircle(sketch, "E25.136.3.0", {"center": v(6.9, 63.5) * mm, "radius": 1 * mm});
            skCircle(sketch, "E25.138.3.0", {"center": v(-20.1, 63.5) * mm, "radius": 1 * mm});
            skCircle(sketch, "E25.140.3.0", {"center": v(-41.1, 63.5) * mm, "radius": 1 * mm});
            skCircle(sketch, "E25.144.3.0", {"center": v(-47.1, 63.5) * mm, "radius": 1 * mm});
            skCircle(sketch, "E25.146.3.0", {"center": v(-42.6, 62) * mm, "radius": 1 * mm});
            skCircle(sketch, "E25.148.3.0", {"center": v(-45.6, 62) * mm, "radius": 1 * mm});
            skCircle(sketch, "E25.150.3.0", {"center": v(-48.6, 62) * mm, "radius": 1 * mm});
            skLineSegment(sketch, "E25.152.3.0", {"start": v(-50.1, 63.5) * mm, "end": v(-50.1, 64.5) * mm, "construction": true});
            skCircle(sketch, "E25.155.3.0", {"center": v(-50.1, 63.5) * mm, "radius": 1 * mm});
            skLineSegment(sketch, "E25.157.3.0", {"start": v(-51.1, 63.5) * mm, "end": v(-50.1, 63.5) * mm, "construction": true});
            skLineSegment(sketch, "E25.160.3.0", {"start": v(-51.1, 62) * mm, "end": v(-48.6, 62) * mm, "construction": true});
            skLineSegment(sketch, "E25.163.3.0", {"start": v(-48.6, 62) * mm, "end": v(-48.6, 64.5) * mm, "construction": true});
            skCircle(sketch, "E25.0.4.0", {"center": v(27.9, 60.5) * mm, "radius": 1 * mm});
            skCircle(sketch, "E25.2.4.0", {"center": v(-32.1, 60.5) * mm, "radius": 1 * mm});
            skCircle(sketch, "E25.4.4.0", {"center": v(36.9, 60.5) * mm, "radius": 1 * mm});
            skCircle(sketch, "E25.6.4.0", {"center": v(3.9, 60.5) * mm, "radius": 1 * mm});
            skCircle(sketch, "E25.8.4.0", {"center": v(54.9, 60.5) * mm, "radius": 1 * mm});
            skCircle(sketch, "E25.10.4.0", {"center": v(53.4, 59) * mm, "radius": 1 * mm});
            skCircle(sketch, "E25.12.4.0", {"center": v(29.4, 59) * mm, "radius": 1 * mm});
            skCircle(sketch, "E25.14.4.0", {"center": v(2.4, 59) * mm, "radius": 1 * mm});
            skCircle(sketch, "E25.18.4.0", {"center": v(18.9, 60.5) * mm, "radius": 1 * mm});
            skCircle(sketch, "E25.20.4.0", {"center": v(-30.6, 59) * mm, "radius": 1 * mm});
            skCircle(sketch, "E25.24.4.0", {"center": v(-44.1, 60.5) * mm, "radius": 1 * mm});
            skCircle(sketch, "E25.26.4.0", {"center": v(30.9, 60.5) * mm, "radius": 1 * mm});
            skCircle(sketch, "E25.28.4.0", {"center": v(-9.6, 59) * mm, "radius": 1 * mm});
            skCircle(sketch, "E25.32.4.0", {"center": v(-14.1, 60.5) * mm, "radius": 1 * mm});
            skCircle(sketch, "E25.34.4.0", {"center": v(-2.1, 60.5) * mm, "radius": 1 * mm});
            skCircle(sketch, "E25.36.4.0", {"center": v(9.9, 60.5) * mm, "radius": 1 * mm});
            skCircle(sketch, "E25.38.4.0", {"center": v(24.9, 60.5) * mm, "radius": 1 * mm});
            skCircle(sketch, "E25.40.4.0", {"center": v(5.4, 59) * mm, "radius": 1 * mm});
            skCircle(sketch, "E25.42.4.0", {"center": v(-23.1, 60.5) * mm, "radius": 1 * mm});
            skCircle(sketch, "E25.44.4.0", {"center": v(-5.1, 60.5) * mm, "radius": 1 * mm});
            skCircle(sketch, "E25.46.4.0", {"center": v(23.4, 59) * mm, "radius": 1 * mm});
            skCircle(sketch, "E25.48.4.0", {"center": v(42.9, 60.5) * mm, "radius": 1 * mm});
            skCircle(sketch, "E25.50.4.0", {"center": v(0.9, 60.5) * mm, "radius": 1 * mm});
            skCircle(sketch, "E25.52.4.0", {"center": v(-36.6, 59) * mm, "radius": 1 * mm});
            skCircle(sketch, "E25.54.4.0", {"center": v(41.4, 59) * mm, "radius": 1 * mm});
            skCircle(sketch, "E25.56.4.0", {"center": v(-12.6, 59) * mm, "radius": 1 * mm});
            skCircle(sketch, "E25.58.4.0", {"center": v(-26.1, 60.5) * mm, "radius": 1 * mm});
            skCircle(sketch, "E25.60.4.0", {"center": v(-8.1, 60.5) * mm, "radius": 1 * mm});
            skCircle(sketch, "E25.62.4.0", {"center": v(-27.6, 59) * mm, "radius": 1 * mm});
            skCircle(sketch, "E25.64.4.0", {"center": v(-29.1, 60.5) * mm, "radius": 1 * mm});
            skCircle(sketch, "E25.66.4.0", {"center": v(15.9, 60.5) * mm, "radius": 1 * mm});
            skCircle(sketch, "E25.68.4.0", {"center": v(-3.6, 59) * mm, "radius": 1 * mm});
            skCircle(sketch, "E25.70.4.0", {"center": v(-11.1, 60.5) * mm, "radius": 1 * mm});
            skCircle(sketch, "E25.72.4.0", {"center": v(44.4, 59) * mm, "radius": 1 * mm});
            skCircle(sketch, "E25.74.4.0", {"center": v(8.4, 59) * mm, "radius": 1 * mm});
            skCircle(sketch, "E25.76.4.0", {"center": v(33.9, 60.5) * mm, "radius": 1 * mm});
            skCircle(sketch, "E25.78.4.0", {"center": v(12.9, 60.5) * mm, "radius": 1 * mm});
            skCircle(sketch, "E25.80.4.0", {"center": v(-38.1, 60.5) * mm, "radius": 1 * mm});
            skCircle(sketch, "E25.82.4.0", {"center": v(-18.6, 59) * mm, "radius": 1 * mm});
            skCircle(sketch, "E25.84.4.0", {"center": v(-17.1, 60.5) * mm, "radius": 1 * mm});
            skCircle(sketch, "E25.86.4.0", {"center": v(48.9, 60.5) * mm, "radius": 1 * mm});
            skCircle(sketch, "E25.88.4.0", {"center": v(35.4, 59) * mm, "radius": 1 * mm});
            skCircle(sketch, "E25.90.4.0", {"center": v(11.4, 59) * mm, "radius": 1 * mm});
            skCircle(sketch, "E25.92.4.0", {"center": v(-24.6, 59) * mm, "radius": 1 * mm});
            skCircle(sketch, "E25.94.4.0", {"center": v(21.9, 60.5) * mm, "radius": 1 * mm});
            skCircle(sketch, "E25.96.4.0", {"center": v(50.4, 59) * mm, "radius": 1 * mm});
            skCircle(sketch, "E25.98.4.0", {"center": v(26.4, 59) * mm, "radius": 1 * mm});
            skCircle(sketch, "E25.100.4.0", {"center": v(20.4, 59) * mm, "radius": 1 * mm});
            skCircle(sketch, "E25.102.4.0", {"center": v(39.9, 60.5) * mm, "radius": 1 * mm});
            skCircle(sketch, "E25.104.4.0", {"center": v(-0.6, 59) * mm, "radius": 1 * mm});
            skCircle(sketch, "E25.106.4.0", {"center": v(47.4, 59) * mm, "radius": 1 * mm});
            skCircle(sketch, "E25.110.4.0", {"center": v(-39.6, 59) * mm, "radius": 1 * mm});
            skCircle(sketch, "E25.112.4.0", {"center": v(38.4, 59) * mm, "radius": 1 * mm});
            skCircle(sketch, "E25.114.4.0", {"center": v(-35.1, 60.5) * mm, "radius": 1 * mm});
            skCircle(sketch, "E25.116.4.0", {"center": v(17.4, 59) * mm, "radius": 1 * mm});
            skCircle(sketch, "E25.118.4.0", {"center": v(51.9, 60.5) * mm, "radius": 1 * mm});
            skCircle(sketch, "E25.120.4.0", {"center": v(-33.6, 59) * mm, "radius": 1 * mm});
            skCircle(sketch, "E25.124.4.0", {"center": v(-15.6, 59) * mm, "radius": 1 * mm});
            skCircle(sketch, "E25.126.4.0", {"center": v(14.4, 59) * mm, "radius": 1 * mm});
            skCircle(sketch, "E25.128.4.0", {"center": v(45.9, 60.5) * mm, "radius": 1 * mm});
            skCircle(sketch, "E25.130.4.0", {"center": v(-6.6, 59) * mm, "radius": 1 * mm});
            skCircle(sketch, "E25.132.4.0", {"center": v(32.4, 59) * mm, "radius": 1 * mm});
            skCircle(sketch, "E25.134.4.0", {"center": v(-21.6, 59) * mm, "radius": 1 * mm});
            skCircle(sketch, "E25.136.4.0", {"center": v(6.9, 60.5) * mm, "radius": 1 * mm});
            skCircle(sketch, "E25.138.4.0", {"center": v(-20.1, 60.5) * mm, "radius": 1 * mm});
            skCircle(sketch, "E25.140.4.0", {"center": v(-41.1, 60.5) * mm, "radius": 1 * mm});
            skCircle(sketch, "E25.144.4.0", {"center": v(-47.1, 60.5) * mm, "radius": 1 * mm});
            skCircle(sketch, "E25.146.4.0", {"center": v(-42.6, 59) * mm, "radius": 1 * mm});
            skCircle(sketch, "E25.148.4.0", {"center": v(-45.6, 59) * mm, "radius": 1 * mm});
            skCircle(sketch, "E25.150.4.0", {"center": v(-48.6, 59) * mm, "radius": 1 * mm});
            skLineSegment(sketch, "E25.152.4.0", {"start": v(-50.1, 60.5) * mm, "end": v(-50.1, 61.5) * mm, "construction": true});
            skCircle(sketch, "E25.155.4.0", {"center": v(-50.1, 60.5) * mm, "radius": 1 * mm});
            skLineSegment(sketch, "E25.157.4.0", {"start": v(-51.1, 60.5) * mm, "end": v(-50.1, 60.5) * mm, "construction": true});
            skLineSegment(sketch, "E25.160.4.0", {"start": v(-51.1, 59) * mm, "end": v(-48.6, 59) * mm, "construction": true});
            skLineSegment(sketch, "E25.163.4.0", {"start": v(-48.6, 59) * mm, "end": v(-48.6, 61.5) * mm, "construction": true});
            skCircle(sketch, "E25.0.5.0", {"center": v(27.9, 57.5) * mm, "radius": 1 * mm});
            skCircle(sketch, "E25.2.5.0", {"center": v(-32.1, 57.5) * mm, "radius": 1 * mm});
            skCircle(sketch, "E25.4.5.0", {"center": v(36.9, 57.5) * mm, "radius": 1 * mm});
            skCircle(sketch, "E25.6.5.0", {"center": v(3.9, 57.5) * mm, "radius": 1 * mm});
            skCircle(sketch, "E25.8.5.0", {"center": v(54.9, 57.5) * mm, "radius": 1 * mm});
            skCircle(sketch, "E25.10.5.0", {"center": v(53.4, 56) * mm, "radius": 1 * mm});
            skCircle(sketch, "E25.12.5.0", {"center": v(29.4, 56) * mm, "radius": 1 * mm});
            skCircle(sketch, "E25.14.5.0", {"center": v(2.4, 56) * mm, "radius": 1 * mm});
            skCircle(sketch, "E25.18.5.0", {"center": v(18.9, 57.5) * mm, "radius": 1 * mm});
            skCircle(sketch, "E25.20.5.0", {"center": v(-30.6, 56) * mm, "radius": 1 * mm});
            skCircle(sketch, "E25.24.5.0", {"center": v(-44.1, 57.5) * mm, "radius": 1 * mm});
            skCircle(sketch, "E25.26.5.0", {"center": v(30.9, 57.5) * mm, "radius": 1 * mm});
            skCircle(sketch, "E25.28.5.0", {"center": v(-9.6, 56) * mm, "radius": 1 * mm});
            skCircle(sketch, "E25.32.5.0", {"center": v(-14.1, 57.5) * mm, "radius": 1 * mm});
            skCircle(sketch, "E25.34.5.0", {"center": v(-2.1, 57.5) * mm, "radius": 1 * mm});
            skCircle(sketch, "E25.36.5.0", {"center": v(9.9, 57.5) * mm, "radius": 1 * mm});
            skCircle(sketch, "E25.38.5.0", {"center": v(24.9, 57.5) * mm, "radius": 1 * mm});
            skCircle(sketch, "E25.40.5.0", {"center": v(5.4, 56) * mm, "radius": 1 * mm});
            skCircle(sketch, "E25.42.5.0", {"center": v(-23.1, 57.5) * mm, "radius": 1 * mm});
            skCircle(sketch, "E25.44.5.0", {"center": v(-5.1, 57.5) * mm, "radius": 1 * mm});
            skCircle(sketch, "E25.46.5.0", {"center": v(23.4, 56) * mm, "radius": 1 * mm});
            skCircle(sketch, "E25.48.5.0", {"center": v(42.9, 57.5) * mm, "radius": 1 * mm});
            skCircle(sketch, "E25.50.5.0", {"center": v(0.9, 57.5) * mm, "radius": 1 * mm});
            skCircle(sketch, "E25.52.5.0", {"center": v(-36.6, 56) * mm, "radius": 1 * mm});
            skCircle(sketch, "E25.54.5.0", {"center": v(41.4, 56) * mm, "radius": 1 * mm});
            skCircle(sketch, "E25.56.5.0", {"center": v(-12.6, 56) * mm, "radius": 1 * mm});
            skCircle(sketch, "E25.58.5.0", {"center": v(-26.1, 57.5) * mm, "radius": 1 * mm});
            skCircle(sketch, "E25.60.5.0", {"center": v(-8.1, 57.5) * mm, "radius": 1 * mm});
            skCircle(sketch, "E25.62.5.0", {"center": v(-27.6, 56) * mm, "radius": 1 * mm});
            skCircle(sketch, "E25.64.5.0", {"center": v(-29.1, 57.5) * mm, "radius": 1 * mm});
            skCircle(sketch, "E25.66.5.0", {"center": v(15.9, 57.5) * mm, "radius": 1 * mm});
            skCircle(sketch, "E25.68.5.0", {"center": v(-3.6, 56) * mm, "radius": 1 * mm});
            skCircle(sketch, "E25.70.5.0", {"center": v(-11.1, 57.5) * mm, "radius": 1 * mm});
            skCircle(sketch, "E25.72.5.0", {"center": v(44.4, 56) * mm, "radius": 1 * mm});
            skCircle(sketch, "E25.74.5.0", {"center": v(8.4, 56) * mm, "radius": 1 * mm});
            skCircle(sketch, "E25.76.5.0", {"center": v(33.9, 57.5) * mm, "radius": 1 * mm});
            skCircle(sketch, "E25.78.5.0", {"center": v(12.9, 57.5) * mm, "radius": 1 * mm});
            skCircle(sketch, "E25.80.5.0", {"center": v(-38.1, 57.5) * mm, "radius": 1 * mm});
            skCircle(sketch, "E25.82.5.0", {"center": v(-18.6, 56) * mm, "radius": 1 * mm});
            skCircle(sketch, "E25.84.5.0", {"center": v(-17.1, 57.5) * mm, "radius": 1 * mm});
            skCircle(sketch, "E25.86.5.0", {"center": v(48.9, 57.5) * mm, "radius": 1 * mm});
            skCircle(sketch, "E25.88.5.0", {"center": v(35.4, 56) * mm, "radius": 1 * mm});
            skCircle(sketch, "E25.90.5.0", {"center": v(11.4, 56) * mm, "radius": 1 * mm});
            skCircle(sketch, "E25.92.5.0", {"center": v(-24.6, 56) * mm, "radius": 1 * mm});
            skCircle(sketch, "E25.94.5.0", {"center": v(21.9, 57.5) * mm, "radius": 1 * mm});
            skCircle(sketch, "E25.96.5.0", {"center": v(50.4, 56) * mm, "radius": 1 * mm});
            skCircle(sketch, "E25.98.5.0", {"center": v(26.4, 56) * mm, "radius": 1 * mm});
            skCircle(sketch, "E25.100.5.0", {"center": v(20.4, 56) * mm, "radius": 1 * mm});
            skCircle(sketch, "E25.102.5.0", {"center": v(39.9, 57.5) * mm, "radius": 1 * mm});
            skCircle(sketch, "E25.104.5.0", {"center": v(-0.6, 56) * mm, "radius": 1 * mm});
            skCircle(sketch, "E25.106.5.0", {"center": v(47.4, 56) * mm, "radius": 1 * mm});
            skCircle(sketch, "E25.110.5.0", {"center": v(-39.6, 56) * mm, "radius": 1 * mm});
            skCircle(sketch, "E25.112.5.0", {"center": v(38.4, 56) * mm, "radius": 1 * mm});
            skCircle(sketch, "E25.114.5.0", {"center": v(-35.1, 57.5) * mm, "radius": 1 * mm});
            skCircle(sketch, "E25.116.5.0", {"center": v(17.4, 56) * mm, "radius": 1 * mm});
            skCircle(sketch, "E25.118.5.0", {"center": v(51.9, 57.5) * mm, "radius": 1 * mm});
            skCircle(sketch, "E25.120.5.0", {"center": v(-33.6, 56) * mm, "radius": 1 * mm});
            skCircle(sketch, "E25.124.5.0", {"center": v(-15.6, 56) * mm, "radius": 1 * mm});
            skCircle(sketch, "E25.126.5.0", {"center": v(14.4, 56) * mm, "radius": 1 * mm});
            skCircle(sketch, "E25.128.5.0", {"center": v(45.9, 57.5) * mm, "radius": 1 * mm});
            skCircle(sketch, "E25.130.5.0", {"center": v(-6.6, 56) * mm, "radius": 1 * mm});
            skCircle(sketch, "E25.132.5.0", {"center": v(32.4, 56) * mm, "radius": 1 * mm});
            skCircle(sketch, "E25.134.5.0", {"center": v(-21.6, 56) * mm, "radius": 1 * mm});
            skCircle(sketch, "E25.136.5.0", {"center": v(6.9, 57.5) * mm, "radius": 1 * mm});
            skCircle(sketch, "E25.138.5.0", {"center": v(-20.1, 57.5) * mm, "radius": 1 * mm});
            skCircle(sketch, "E25.140.5.0", {"center": v(-41.1, 57.5) * mm, "radius": 1 * mm});
            skCircle(sketch, "E25.144.5.0", {"center": v(-47.1, 57.5) * mm, "radius": 1 * mm});
            skCircle(sketch, "E25.146.5.0", {"center": v(-42.6, 56) * mm, "radius": 1 * mm});
            skCircle(sketch, "E25.148.5.0", {"center": v(-45.6, 56) * mm, "radius": 1 * mm});
            skCircle(sketch, "E25.150.5.0", {"center": v(-48.6, 56) * mm, "radius": 1 * mm});
            skLineSegment(sketch, "E25.152.5.0", {"start": v(-50.1, 57.5) * mm, "end": v(-50.1, 58.5) * mm, "construction": true});
            skCircle(sketch, "E25.155.5.0", {"center": v(-50.1, 57.5) * mm, "radius": 1 * mm});
            skLineSegment(sketch, "E25.157.5.0", {"start": v(-51.1, 57.5) * mm, "end": v(-50.1, 57.5) * mm, "construction": true});
            skLineSegment(sketch, "E25.160.5.0", {"start": v(-51.1, 56) * mm, "end": v(-48.6, 56) * mm, "construction": true});
            skLineSegment(sketch, "E25.163.5.0", {"start": v(-48.6, 56) * mm, "end": v(-48.6, 58.5) * mm, "construction": true});
            skCircle(sketch, "E25.0.6.0", {"center": v(27.9, 54.5) * mm, "radius": 1 * mm});
            skCircle(sketch, "E25.2.6.0", {"center": v(-32.1, 54.5) * mm, "radius": 1 * mm});
            skCircle(sketch, "E25.4.6.0", {"center": v(36.9, 54.5) * mm, "radius": 1 * mm});
            skCircle(sketch, "E25.6.6.0", {"center": v(3.9, 54.5) * mm, "radius": 1 * mm});
            skCircle(sketch, "E25.8.6.0", {"center": v(54.9, 54.5) * mm, "radius": 1 * mm});
            skCircle(sketch, "E25.10.6.0", {"center": v(53.4, 53) * mm, "radius": 1 * mm});
            skCircle(sketch, "E25.12.6.0", {"center": v(29.4, 53) * mm, "radius": 1 * mm});
            skCircle(sketch, "E25.14.6.0", {"center": v(2.4, 53) * mm, "radius": 1 * mm});
            skCircle(sketch, "E25.18.6.0", {"center": v(18.9, 54.5) * mm, "radius": 1 * mm});
            skCircle(sketch, "E25.20.6.0", {"center": v(-30.6, 53) * mm, "radius": 1 * mm});
            skCircle(sketch, "E25.24.6.0", {"center": v(-44.1, 54.5) * mm, "radius": 1 * mm});
            skCircle(sketch, "E25.26.6.0", {"center": v(30.9, 54.5) * mm, "radius": 1 * mm});
            skCircle(sketch, "E25.28.6.0", {"center": v(-9.6, 53) * mm, "radius": 1 * mm});
            skCircle(sketch, "E25.32.6.0", {"center": v(-14.1, 54.5) * mm, "radius": 1 * mm});
            skCircle(sketch, "E25.34.6.0", {"center": v(-2.1, 54.5) * mm, "radius": 1 * mm});
            skCircle(sketch, "E25.36.6.0", {"center": v(9.9, 54.5) * mm, "radius": 1 * mm});
            skCircle(sketch, "E25.38.6.0", {"center": v(24.9, 54.5) * mm, "radius": 1 * mm});
            skCircle(sketch, "E25.40.6.0", {"center": v(5.4, 53) * mm, "radius": 1 * mm});
            skCircle(sketch, "E25.42.6.0", {"center": v(-23.1, 54.5) * mm, "radius": 1 * mm});
            skCircle(sketch, "E25.44.6.0", {"center": v(-5.1, 54.5) * mm, "radius": 1 * mm});
            skCircle(sketch, "E25.46.6.0", {"center": v(23.4, 53) * mm, "radius": 1 * mm});
            skCircle(sketch, "E25.48.6.0", {"center": v(42.9, 54.5) * mm, "radius": 1 * mm});
            skCircle(sketch, "E25.50.6.0", {"center": v(0.9, 54.5) * mm, "radius": 1 * mm});
            skCircle(sketch, "E25.52.6.0", {"center": v(-36.6, 53) * mm, "radius": 1 * mm});
            skCircle(sketch, "E25.54.6.0", {"center": v(41.4, 53) * mm, "radius": 1 * mm});
            skCircle(sketch, "E25.56.6.0", {"center": v(-12.6, 53) * mm, "radius": 1 * mm});
            skCircle(sketch, "E25.58.6.0", {"center": v(-26.1, 54.5) * mm, "radius": 1 * mm});
            skCircle(sketch, "E25.60.6.0", {"center": v(-8.1, 54.5) * mm, "radius": 1 * mm});
            skCircle(sketch, "E25.62.6.0", {"center": v(-27.6, 53) * mm, "radius": 1 * mm});
            skCircle(sketch, "E25.64.6.0", {"center": v(-29.1, 54.5) * mm, "radius": 1 * mm});
            skCircle(sketch, "E25.66.6.0", {"center": v(15.9, 54.5) * mm, "radius": 1 * mm});
            skCircle(sketch, "E25.68.6.0", {"center": v(-3.6, 53) * mm, "radius": 1 * mm});
            skCircle(sketch, "E25.70.6.0", {"center": v(-11.1, 54.5) * mm, "radius": 1 * mm});
            skCircle(sketch, "E25.72.6.0", {"center": v(44.4, 53) * mm, "radius": 1 * mm});
            skCircle(sketch, "E25.74.6.0", {"center": v(8.4, 53) * mm, "radius": 1 * mm});
            skCircle(sketch, "E25.76.6.0", {"center": v(33.9, 54.5) * mm, "radius": 1 * mm});
            skCircle(sketch, "E25.78.6.0", {"center": v(12.9, 54.5) * mm, "radius": 1 * mm});
            skCircle(sketch, "E25.80.6.0", {"center": v(-38.1, 54.5) * mm, "radius": 1 * mm});
            skCircle(sketch, "E25.82.6.0", {"center": v(-18.6, 53) * mm, "radius": 1 * mm});
            skCircle(sketch, "E25.84.6.0", {"center": v(-17.1, 54.5) * mm, "radius": 1 * mm});
            skCircle(sketch, "E25.86.6.0", {"center": v(48.9, 54.5) * mm, "radius": 1 * mm});
            skCircle(sketch, "E25.88.6.0", {"center": v(35.4, 53) * mm, "radius": 1 * mm});
            skCircle(sketch, "E25.90.6.0", {"center": v(11.4, 53) * mm, "radius": 1 * mm});
            skCircle(sketch, "E25.92.6.0", {"center": v(-24.6, 53) * mm, "radius": 1 * mm});
            skCircle(sketch, "E25.94.6.0", {"center": v(21.9, 54.5) * mm, "radius": 1 * mm});
            skCircle(sketch, "E25.96.6.0", {"center": v(50.4, 53) * mm, "radius": 1 * mm});
            skCircle(sketch, "E25.98.6.0", {"center": v(26.4, 53) * mm, "radius": 1 * mm});
            skCircle(sketch, "E25.100.6.0", {"center": v(20.4, 53) * mm, "radius": 1 * mm});
            skCircle(sketch, "E25.102.6.0", {"center": v(39.9, 54.5) * mm, "radius": 1 * mm});
            skCircle(sketch, "E25.104.6.0", {"center": v(-0.6, 53) * mm, "radius": 1 * mm});
            skCircle(sketch, "E25.106.6.0", {"center": v(47.4, 53) * mm, "radius": 1 * mm});
            skCircle(sketch, "E25.110.6.0", {"center": v(-39.6, 53) * mm, "radius": 1 * mm});
            skCircle(sketch, "E25.112.6.0", {"center": v(38.4, 53) * mm, "radius": 1 * mm});
            skCircle(sketch, "E25.114.6.0", {"center": v(-35.1, 54.5) * mm, "radius": 1 * mm});
            skCircle(sketch, "E25.116.6.0", {"center": v(17.4, 53) * mm, "radius": 1 * mm});
            skCircle(sketch, "E25.118.6.0", {"center": v(51.9, 54.5) * mm, "radius": 1 * mm});
            skCircle(sketch, "E25.120.6.0", {"center": v(-33.6, 53) * mm, "radius": 1 * mm});
            skCircle(sketch, "E25.124.6.0", {"center": v(-15.6, 53) * mm, "radius": 1 * mm});
            skCircle(sketch, "E25.126.6.0", {"center": v(14.4, 53) * mm, "radius": 1 * mm});
            skCircle(sketch, "E25.128.6.0", {"center": v(45.9, 54.5) * mm, "radius": 1 * mm});
            skCircle(sketch, "E25.130.6.0", {"center": v(-6.6, 53) * mm, "radius": 1 * mm});
            skCircle(sketch, "E25.132.6.0", {"center": v(32.4, 53) * mm, "radius": 1 * mm});
            skCircle(sketch, "E25.134.6.0", {"center": v(-21.6, 53) * mm, "radius": 1 * mm});
            skCircle(sketch, "E25.136.6.0", {"center": v(6.9, 54.5) * mm, "radius": 1 * mm});
            skCircle(sketch, "E25.138.6.0", {"center": v(-20.1, 54.5) * mm, "radius": 1 * mm});
            skCircle(sketch, "E25.140.6.0", {"center": v(-41.1, 54.5) * mm, "radius": 1 * mm});
            skCircle(sketch, "E25.144.6.0", {"center": v(-47.1, 54.5) * mm, "radius": 1 * mm});
            skCircle(sketch, "E25.146.6.0", {"center": v(-42.6, 53) * mm, "radius": 1 * mm});
            skCircle(sketch, "E25.148.6.0", {"center": v(-45.6, 53) * mm, "radius": 1 * mm});
            skCircle(sketch, "E25.150.6.0", {"center": v(-48.6, 53) * mm, "radius": 1 * mm});
            skLineSegment(sketch, "E25.152.6.0", {"start": v(-50.1, 54.5) * mm, "end": v(-50.1, 55.5) * mm, "construction": true});
            skCircle(sketch, "E25.155.6.0", {"center": v(-50.1, 54.5) * mm, "radius": 1 * mm});
            skLineSegment(sketch, "E25.157.6.0", {"start": v(-51.1, 54.5) * mm, "end": v(-50.1, 54.5) * mm, "construction": true});
            skLineSegment(sketch, "E25.160.6.0", {"start": v(-51.1, 53) * mm, "end": v(-48.6, 53) * mm, "construction": true});
            skLineSegment(sketch, "E25.163.6.0", {"start": v(-48.6, 53) * mm, "end": v(-48.6, 55.5) * mm, "construction": true});
            skCircle(sketch, "E25.0.7.0", {"center": v(27.9, 51.5) * mm, "radius": 1 * mm});
            skCircle(sketch, "E25.2.7.0", {"center": v(-32.1, 51.5) * mm, "radius": 1 * mm});
            skCircle(sketch, "E25.4.7.0", {"center": v(36.9, 51.5) * mm, "radius": 1 * mm});
            skCircle(sketch, "E25.6.7.0", {"center": v(3.9, 51.5) * mm, "radius": 1 * mm});
            skCircle(sketch, "E25.8.7.0", {"center": v(54.9, 51.5) * mm, "radius": 1 * mm});
            skCircle(sketch, "E25.10.7.0", {"center": v(53.4, 50) * mm, "radius": 1 * mm});
            skCircle(sketch, "E25.12.7.0", {"center": v(29.4, 50) * mm, "radius": 1 * mm});
            skCircle(sketch, "E25.14.7.0", {"center": v(2.4, 50) * mm, "radius": 1 * mm});
            skCircle(sketch, "E25.18.7.0", {"center": v(18.9, 51.5) * mm, "radius": 1 * mm});
            skCircle(sketch, "E25.20.7.0", {"center": v(-30.6, 50) * mm, "radius": 1 * mm});
            skCircle(sketch, "E25.24.7.0", {"center": v(-44.1, 51.5) * mm, "radius": 1 * mm});
            skCircle(sketch, "E25.26.7.0", {"center": v(30.9, 51.5) * mm, "radius": 1 * mm});
            skCircle(sketch, "E25.28.7.0", {"center": v(-9.6, 50) * mm, "radius": 1 * mm});
            skCircle(sketch, "E25.32.7.0", {"center": v(-14.1, 51.5) * mm, "radius": 1 * mm});
            skCircle(sketch, "E25.34.7.0", {"center": v(-2.1, 51.5) * mm, "radius": 1 * mm});
            skCircle(sketch, "E25.36.7.0", {"center": v(9.9, 51.5) * mm, "radius": 1 * mm});
            skCircle(sketch, "E25.38.7.0", {"center": v(24.9, 51.5) * mm, "radius": 1 * mm});
            skCircle(sketch, "E25.40.7.0", {"center": v(5.4, 50) * mm, "radius": 1 * mm});
            skCircle(sketch, "E25.42.7.0", {"center": v(-23.1, 51.5) * mm, "radius": 1 * mm});
            skCircle(sketch, "E25.44.7.0", {"center": v(-5.1, 51.5) * mm, "radius": 1 * mm});
            skCircle(sketch, "E25.46.7.0", {"center": v(23.4, 50) * mm, "radius": 1 * mm});
            skCircle(sketch, "E25.48.7.0", {"center": v(42.9, 51.5) * mm, "radius": 1 * mm});
            skCircle(sketch, "E25.50.7.0", {"center": v(0.9, 51.5) * mm, "radius": 1 * mm});
            skCircle(sketch, "E25.52.7.0", {"center": v(-36.6, 50) * mm, "radius": 1 * mm});
            skCircle(sketch, "E25.54.7.0", {"center": v(41.4, 50) * mm, "radius": 1 * mm});
            skCircle(sketch, "E25.56.7.0", {"center": v(-12.6, 50) * mm, "radius": 1 * mm});
            skCircle(sketch, "E25.58.7.0", {"center": v(-26.1, 51.5) * mm, "radius": 1 * mm});
            skCircle(sketch, "E25.60.7.0", {"center": v(-8.1, 51.5) * mm, "radius": 1 * mm});
            skCircle(sketch, "E25.62.7.0", {"center": v(-27.6, 50) * mm, "radius": 1 * mm});
            skCircle(sketch, "E25.64.7.0", {"center": v(-29.1, 51.5) * mm, "radius": 1 * mm});
            skCircle(sketch, "E25.66.7.0", {"center": v(15.9, 51.5) * mm, "radius": 1 * mm});
            skCircle(sketch, "E25.68.7.0", {"center": v(-3.6, 50) * mm, "radius": 1 * mm});
            skCircle(sketch, "E25.70.7.0", {"center": v(-11.1, 51.5) * mm, "radius": 1 * mm});
            skCircle(sketch, "E25.72.7.0", {"center": v(44.4, 50) * mm, "radius": 1 * mm});
            skCircle(sketch, "E25.74.7.0", {"center": v(8.4, 50) * mm, "radius": 1 * mm});
            skCircle(sketch, "E25.76.7.0", {"center": v(33.9, 51.5) * mm, "radius": 1 * mm});
            skCircle(sketch, "E25.78.7.0", {"center": v(12.9, 51.5) * mm, "radius": 1 * mm});
            skCircle(sketch, "E25.80.7.0", {"center": v(-38.1, 51.5) * mm, "radius": 1 * mm});
            skCircle(sketch, "E25.82.7.0", {"center": v(-18.6, 50) * mm, "radius": 1 * mm});
            skCircle(sketch, "E25.84.7.0", {"center": v(-17.1, 51.5) * mm, "radius": 1 * mm});
            skCircle(sketch, "E25.86.7.0", {"center": v(48.9, 51.5) * mm, "radius": 1 * mm});
            skCircle(sketch, "E25.88.7.0", {"center": v(35.4, 50) * mm, "radius": 1 * mm});
            skCircle(sketch, "E25.90.7.0", {"center": v(11.4, 50) * mm, "radius": 1 * mm});
            skCircle(sketch, "E25.92.7.0", {"center": v(-24.6, 50) * mm, "radius": 1 * mm});
            skCircle(sketch, "E25.94.7.0", {"center": v(21.9, 51.5) * mm, "radius": 1 * mm});
            skCircle(sketch, "E25.96.7.0", {"center": v(50.4, 50) * mm, "radius": 1 * mm});
            skCircle(sketch, "E25.98.7.0", {"center": v(26.4, 50) * mm, "radius": 1 * mm});
            skCircle(sketch, "E25.100.7.0", {"center": v(20.4, 50) * mm, "radius": 1 * mm});
            skCircle(sketch, "E25.102.7.0", {"center": v(39.9, 51.5) * mm, "radius": 1 * mm});
            skCircle(sketch, "E25.104.7.0", {"center": v(-0.6, 50) * mm, "radius": 1 * mm});
            skCircle(sketch, "E25.106.7.0", {"center": v(47.4, 50) * mm, "radius": 1 * mm});
            skCircle(sketch, "E25.110.7.0", {"center": v(-39.6, 50) * mm, "radius": 1 * mm});
            skCircle(sketch, "E25.112.7.0", {"center": v(38.4, 50) * mm, "radius": 1 * mm});
            skCircle(sketch, "E25.114.7.0", {"center": v(-35.1, 51.5) * mm, "radius": 1 * mm});
            skCircle(sketch, "E25.116.7.0", {"center": v(17.4, 50) * mm, "radius": 1 * mm});
            skCircle(sketch, "E25.118.7.0", {"center": v(51.9, 51.5) * mm, "radius": 1 * mm});
            skCircle(sketch, "E25.120.7.0", {"center": v(-33.6, 50) * mm, "radius": 1 * mm});
            skCircle(sketch, "E25.124.7.0", {"center": v(-15.6, 50) * mm, "radius": 1 * mm});
            skCircle(sketch, "E25.126.7.0", {"center": v(14.4, 50) * mm, "radius": 1 * mm});
            skCircle(sketch, "E25.128.7.0", {"center": v(45.9, 51.5) * mm, "radius": 1 * mm});
            skCircle(sketch, "E25.130.7.0", {"center": v(-6.6, 50) * mm, "radius": 1 * mm});
            skCircle(sketch, "E25.132.7.0", {"center": v(32.4, 50) * mm, "radius": 1 * mm});
            skCircle(sketch, "E25.134.7.0", {"center": v(-21.6, 50) * mm, "radius": 1 * mm});
            skCircle(sketch, "E25.136.7.0", {"center": v(6.9, 51.5) * mm, "radius": 1 * mm});
            skCircle(sketch, "E25.138.7.0", {"center": v(-20.1, 51.5) * mm, "radius": 1 * mm});
            skCircle(sketch, "E25.140.7.0", {"center": v(-41.1, 51.5) * mm, "radius": 1 * mm});
            skCircle(sketch, "E25.144.7.0", {"center": v(-47.1, 51.5) * mm, "radius": 1 * mm});
            skCircle(sketch, "E25.146.7.0", {"center": v(-42.6, 50) * mm, "radius": 1 * mm});
            skCircle(sketch, "E25.148.7.0", {"center": v(-45.6, 50) * mm, "radius": 1 * mm});
            skCircle(sketch, "E25.150.7.0", {"center": v(-48.6, 50) * mm, "radius": 1 * mm});
            skLineSegment(sketch, "E25.152.7.0", {"start": v(-50.1, 51.5) * mm, "end": v(-50.1, 52.5) * mm, "construction": true});
            skCircle(sketch, "E25.155.7.0", {"center": v(-50.1, 51.5) * mm, "radius": 1 * mm});
            skLineSegment(sketch, "E25.157.7.0", {"start": v(-51.1, 51.5) * mm, "end": v(-50.1, 51.5) * mm, "construction": true});
            skLineSegment(sketch, "E25.160.7.0", {"start": v(-51.1, 50) * mm, "end": v(-48.6, 50) * mm, "construction": true});
            skLineSegment(sketch, "E25.163.7.0", {"start": v(-48.6, 50) * mm, "end": v(-48.6, 52.5) * mm, "construction": true});
            skCircle(sketch, "E25.0.8.0", {"center": v(27.9, 48.5) * mm, "radius": 1 * mm});
            skCircle(sketch, "E25.2.8.0", {"center": v(-32.1, 48.5) * mm, "radius": 1 * mm});
            skCircle(sketch, "E25.4.8.0", {"center": v(36.9, 48.5) * mm, "radius": 1 * mm});
            skCircle(sketch, "E25.6.8.0", {"center": v(3.9, 48.5) * mm, "radius": 1 * mm});
            skCircle(sketch, "E25.8.8.0", {"center": v(54.9, 48.5) * mm, "radius": 1 * mm});
            skCircle(sketch, "E25.10.8.0", {"center": v(53.4, 47) * mm, "radius": 1 * mm});
            skCircle(sketch, "E25.12.8.0", {"center": v(29.4, 47) * mm, "radius": 1 * mm});
            skCircle(sketch, "E25.14.8.0", {"center": v(2.4, 47) * mm, "radius": 1 * mm});
            skCircle(sketch, "E25.18.8.0", {"center": v(18.9, 48.5) * mm, "radius": 1 * mm});
            skCircle(sketch, "E25.20.8.0", {"center": v(-30.6, 47) * mm, "radius": 1 * mm});
            skCircle(sketch, "E25.24.8.0", {"center": v(-44.1, 48.5) * mm, "radius": 1 * mm});
            skCircle(sketch, "E25.26.8.0", {"center": v(30.9, 48.5) * mm, "radius": 1 * mm});
            skCircle(sketch, "E25.28.8.0", {"center": v(-9.6, 47) * mm, "radius": 1 * mm});
            skCircle(sketch, "E25.32.8.0", {"center": v(-14.1, 48.5) * mm, "radius": 1 * mm});
            skCircle(sketch, "E25.34.8.0", {"center": v(-2.1, 48.5) * mm, "radius": 1 * mm});
            skCircle(sketch, "E25.36.8.0", {"center": v(9.9, 48.5) * mm, "radius": 1 * mm});
            skCircle(sketch, "E25.38.8.0", {"center": v(24.9, 48.5) * mm, "radius": 1 * mm});
            skCircle(sketch, "E25.40.8.0", {"center": v(5.4, 47) * mm, "radius": 1 * mm});
            skCircle(sketch, "E25.42.8.0", {"center": v(-23.1, 48.5) * mm, "radius": 1 * mm});
            skCircle(sketch, "E25.44.8.0", {"center": v(-5.1, 48.5) * mm, "radius": 1 * mm});
            skCircle(sketch, "E25.46.8.0", {"center": v(23.4, 47) * mm, "radius": 1 * mm});
            skCircle(sketch, "E25.48.8.0", {"center": v(42.9, 48.5) * mm, "radius": 1 * mm});
            skCircle(sketch, "E25.50.8.0", {"center": v(0.9, 48.5) * mm, "radius": 1 * mm});
            skCircle(sketch, "E25.52.8.0", {"center": v(-36.6, 47) * mm, "radius": 1 * mm});
            skCircle(sketch, "E25.54.8.0", {"center": v(41.4, 47) * mm, "radius": 1 * mm});
            skCircle(sketch, "E25.56.8.0", {"center": v(-12.6, 47) * mm, "radius": 1 * mm});
            skCircle(sketch, "E25.58.8.0", {"center": v(-26.1, 48.5) * mm, "radius": 1 * mm});
            skCircle(sketch, "E25.60.8.0", {"center": v(-8.1, 48.5) * mm, "radius": 1 * mm});
            skCircle(sketch, "E25.62.8.0", {"center": v(-27.6, 47) * mm, "radius": 1 * mm});
            skCircle(sketch, "E25.64.8.0", {"center": v(-29.1, 48.5) * mm, "radius": 1 * mm});
            skCircle(sketch, "E25.66.8.0", {"center": v(15.9, 48.5) * mm, "radius": 1 * mm});
            skCircle(sketch, "E25.68.8.0", {"center": v(-3.6, 47) * mm, "radius": 1 * mm});
            skCircle(sketch, "E25.70.8.0", {"center": v(-11.1, 48.5) * mm, "radius": 1 * mm});
            skCircle(sketch, "E25.72.8.0", {"center": v(44.4, 47) * mm, "radius": 1 * mm});
            skCircle(sketch, "E25.74.8.0", {"center": v(8.4, 47) * mm, "radius": 1 * mm});
            skCircle(sketch, "E25.76.8.0", {"center": v(33.9, 48.5) * mm, "radius": 1 * mm});
            skCircle(sketch, "E25.78.8.0", {"center": v(12.9, 48.5) * mm, "radius": 1 * mm});
            skCircle(sketch, "E25.80.8.0", {"center": v(-38.1, 48.5) * mm, "radius": 1 * mm});
            skCircle(sketch, "E25.82.8.0", {"center": v(-18.6, 47) * mm, "radius": 1 * mm});
            skCircle(sketch, "E25.84.8.0", {"center": v(-17.1, 48.5) * mm, "radius": 1 * mm});
            skCircle(sketch, "E25.86.8.0", {"center": v(48.9, 48.5) * mm, "radius": 1 * mm});
            skCircle(sketch, "E25.88.8.0", {"center": v(35.4, 47) * mm, "radius": 1 * mm});
            skCircle(sketch, "E25.90.8.0", {"center": v(11.4, 47) * mm, "radius": 1 * mm});
            skCircle(sketch, "E25.92.8.0", {"center": v(-24.6, 47) * mm, "radius": 1 * mm});
            skCircle(sketch, "E25.94.8.0", {"center": v(21.9, 48.5) * mm, "radius": 1 * mm});
            skCircle(sketch, "E25.96.8.0", {"center": v(50.4, 47) * mm, "radius": 1 * mm});
            skCircle(sketch, "E25.98.8.0", {"center": v(26.4, 47) * mm, "radius": 1 * mm});
            skCircle(sketch, "E25.100.8.0", {"center": v(20.4, 47) * mm, "radius": 1 * mm});
            skCircle(sketch, "E25.102.8.0", {"center": v(39.9, 48.5) * mm, "radius": 1 * mm});
            skCircle(sketch, "E25.104.8.0", {"center": v(-0.6, 47) * mm, "radius": 1 * mm});
            skCircle(sketch, "E25.106.8.0", {"center": v(47.4, 47) * mm, "radius": 1 * mm});
            skCircle(sketch, "E25.110.8.0", {"center": v(-39.6, 47) * mm, "radius": 1 * mm});
            skCircle(sketch, "E25.112.8.0", {"center": v(38.4, 47) * mm, "radius": 1 * mm});
            skCircle(sketch, "E25.114.8.0", {"center": v(-35.1, 48.5) * mm, "radius": 1 * mm});
            skCircle(sketch, "E25.116.8.0", {"center": v(17.4, 47) * mm, "radius": 1 * mm});
            skCircle(sketch, "E25.118.8.0", {"center": v(51.9, 48.5) * mm, "radius": 1 * mm});
            skCircle(sketch, "E25.120.8.0", {"center": v(-33.6, 47) * mm, "radius": 1 * mm});
            skCircle(sketch, "E25.124.8.0", {"center": v(-15.6, 47) * mm, "radius": 1 * mm});
            skCircle(sketch, "E25.126.8.0", {"center": v(14.4, 47) * mm, "radius": 1 * mm});
            skCircle(sketch, "E25.128.8.0", {"center": v(45.9, 48.5) * mm, "radius": 1 * mm});
            skCircle(sketch, "E25.130.8.0", {"center": v(-6.6, 47) * mm, "radius": 1 * mm});
            skCircle(sketch, "E25.132.8.0", {"center": v(32.4, 47) * mm, "radius": 1 * mm});
            skCircle(sketch, "E25.134.8.0", {"center": v(-21.6, 47) * mm, "radius": 1 * mm});
            skCircle(sketch, "E25.136.8.0", {"center": v(6.9, 48.5) * mm, "radius": 1 * mm});
            skCircle(sketch, "E25.138.8.0", {"center": v(-20.1, 48.5) * mm, "radius": 1 * mm});
            skCircle(sketch, "E25.140.8.0", {"center": v(-41.1, 48.5) * mm, "radius": 1 * mm});
            skCircle(sketch, "E25.144.8.0", {"center": v(-47.1, 48.5) * mm, "radius": 1 * mm});
            skCircle(sketch, "E25.146.8.0", {"center": v(-42.6, 47) * mm, "radius": 1 * mm});
            skCircle(sketch, "E25.148.8.0", {"center": v(-45.6, 47) * mm, "radius": 1 * mm});
            skCircle(sketch, "E25.150.8.0", {"center": v(-48.6, 47) * mm, "radius": 1 * mm});
            skLineSegment(sketch, "E25.152.8.0", {"start": v(-50.1, 48.5) * mm, "end": v(-50.1, 49.5) * mm, "construction": true});
            skCircle(sketch, "E25.155.8.0", {"center": v(-50.1, 48.5) * mm, "radius": 1 * mm});
            skLineSegment(sketch, "E25.157.8.0", {"start": v(-51.1, 48.5) * mm, "end": v(-50.1, 48.5) * mm, "construction": true});
            skLineSegment(sketch, "E25.160.8.0", {"start": v(-51.1, 47) * mm, "end": v(-48.6, 47) * mm, "construction": true});
            skLineSegment(sketch, "E25.163.8.0", {"start": v(-48.6, 47) * mm, "end": v(-48.6, 49.5) * mm, "construction": true});
            skCircle(sketch, "E25.0.9.0", {"center": v(27.9, 45.5) * mm, "radius": 1 * mm});
            skCircle(sketch, "E25.2.9.0", {"center": v(-32.1, 45.5) * mm, "radius": 1 * mm});
            skCircle(sketch, "E25.4.9.0", {"center": v(36.9, 45.5) * mm, "radius": 1 * mm});
            skCircle(sketch, "E25.6.9.0", {"center": v(3.9, 45.5) * mm, "radius": 1 * mm});
            skCircle(sketch, "E25.8.9.0", {"center": v(54.9, 45.5) * mm, "radius": 1 * mm});
            skCircle(sketch, "E25.10.9.0", {"center": v(53.4, 44) * mm, "radius": 1 * mm});
            skCircle(sketch, "E25.12.9.0", {"center": v(29.4, 44) * mm, "radius": 1 * mm});
            skCircle(sketch, "E25.14.9.0", {"center": v(2.4, 44) * mm, "radius": 1 * mm});
            skCircle(sketch, "E25.18.9.0", {"center": v(18.9, 45.5) * mm, "radius": 1 * mm});
            skCircle(sketch, "E25.20.9.0", {"center": v(-30.6, 44) * mm, "radius": 1 * mm});
            skCircle(sketch, "E25.24.9.0", {"center": v(-44.1, 45.5) * mm, "radius": 1 * mm});
            skCircle(sketch, "E25.26.9.0", {"center": v(30.9, 45.5) * mm, "radius": 1 * mm});
            skCircle(sketch, "E25.28.9.0", {"center": v(-9.6, 44) * mm, "radius": 1 * mm});
            skCircle(sketch, "E25.32.9.0", {"center": v(-14.1, 45.5) * mm, "radius": 1 * mm});
            skCircle(sketch, "E25.34.9.0", {"center": v(-2.1, 45.5) * mm, "radius": 1 * mm});
            skCircle(sketch, "E25.36.9.0", {"center": v(9.9, 45.5) * mm, "radius": 1 * mm});
            skCircle(sketch, "E25.38.9.0", {"center": v(24.9, 45.5) * mm, "radius": 1 * mm});
            skCircle(sketch, "E25.40.9.0", {"center": v(5.4, 44) * mm, "radius": 1 * mm});
            skCircle(sketch, "E25.42.9.0", {"center": v(-23.1, 45.5) * mm, "radius": 1 * mm});
            skCircle(sketch, "E25.44.9.0", {"center": v(-5.1, 45.5) * mm, "radius": 1 * mm});
            skCircle(sketch, "E25.46.9.0", {"center": v(23.4, 44) * mm, "radius": 1 * mm});
            skCircle(sketch, "E25.48.9.0", {"center": v(42.9, 45.5) * mm, "radius": 1 * mm});
            skCircle(sketch, "E25.50.9.0", {"center": v(0.9, 45.5) * mm, "radius": 1 * mm});
            skCircle(sketch, "E25.52.9.0", {"center": v(-36.6, 44) * mm, "radius": 1 * mm});
            skCircle(sketch, "E25.54.9.0", {"center": v(41.4, 44) * mm, "radius": 1 * mm});
            skCircle(sketch, "E25.56.9.0", {"center": v(-12.6, 44) * mm, "radius": 1 * mm});
            skCircle(sketch, "E25.58.9.0", {"center": v(-26.1, 45.5) * mm, "radius": 1 * mm});
            skCircle(sketch, "E25.60.9.0", {"center": v(-8.1, 45.5) * mm, "radius": 1 * mm});
            skCircle(sketch, "E25.62.9.0", {"center": v(-27.6, 44) * mm, "radius": 1 * mm});
            skCircle(sketch, "E25.64.9.0", {"center": v(-29.1, 45.5) * mm, "radius": 1 * mm});
            skCircle(sketch, "E25.66.9.0", {"center": v(15.9, 45.5) * mm, "radius": 1 * mm});
            skCircle(sketch, "E25.68.9.0", {"center": v(-3.6, 44) * mm, "radius": 1 * mm});
            skCircle(sketch, "E25.70.9.0", {"center": v(-11.1, 45.5) * mm, "radius": 1 * mm});
            skCircle(sketch, "E25.72.9.0", {"center": v(44.4, 44) * mm, "radius": 1 * mm});
            skCircle(sketch, "E25.74.9.0", {"center": v(8.4, 44) * mm, "radius": 1 * mm});
            skCircle(sketch, "E25.76.9.0", {"center": v(33.9, 45.5) * mm, "radius": 1 * mm});
            skCircle(sketch, "E25.78.9.0", {"center": v(12.9, 45.5) * mm, "radius": 1 * mm});
            skCircle(sketch, "E25.80.9.0", {"center": v(-38.1, 45.5) * mm, "radius": 1 * mm});
            skCircle(sketch, "E25.82.9.0", {"center": v(-18.6, 44) * mm, "radius": 1 * mm});
            skCircle(sketch, "E25.84.9.0", {"center": v(-17.1, 45.5) * mm, "radius": 1 * mm});
            skCircle(sketch, "E25.86.9.0", {"center": v(48.9, 45.5) * mm, "radius": 1 * mm});
            skCircle(sketch, "E25.88.9.0", {"center": v(35.4, 44) * mm, "radius": 1 * mm});
            skCircle(sketch, "E25.90.9.0", {"center": v(11.4, 44) * mm, "radius": 1 * mm});
            skCircle(sketch, "E25.92.9.0", {"center": v(-24.6, 44) * mm, "radius": 1 * mm});
            skCircle(sketch, "E25.94.9.0", {"center": v(21.9, 45.5) * mm, "radius": 1 * mm});
            skCircle(sketch, "E25.96.9.0", {"center": v(50.4, 44) * mm, "radius": 1 * mm});
            skCircle(sketch, "E25.98.9.0", {"center": v(26.4, 44) * mm, "radius": 1 * mm});
            skCircle(sketch, "E25.100.9.0", {"center": v(20.4, 44) * mm, "radius": 1 * mm});
            skCircle(sketch, "E25.102.9.0", {"center": v(39.9, 45.5) * mm, "radius": 1 * mm});
            skCircle(sketch, "E25.104.9.0", {"center": v(-0.6, 44) * mm, "radius": 1 * mm});
            skCircle(sketch, "E25.106.9.0", {"center": v(47.4, 44) * mm, "radius": 1 * mm});
            skCircle(sketch, "E25.110.9.0", {"center": v(-39.6, 44) * mm, "radius": 1 * mm});
            skCircle(sketch, "E25.112.9.0", {"center": v(38.4, 44) * mm, "radius": 1 * mm});
            skCircle(sketch, "E25.114.9.0", {"center": v(-35.1, 45.5) * mm, "radius": 1 * mm});
            skCircle(sketch, "E25.116.9.0", {"center": v(17.4, 44) * mm, "radius": 1 * mm});
            skCircle(sketch, "E25.118.9.0", {"center": v(51.9, 45.5) * mm, "radius": 1 * mm});
            skCircle(sketch, "E25.120.9.0", {"center": v(-33.6, 44) * mm, "radius": 1 * mm});
            skCircle(sketch, "E25.124.9.0", {"center": v(-15.6, 44) * mm, "radius": 1 * mm});
            skCircle(sketch, "E25.126.9.0", {"center": v(14.4, 44) * mm, "radius": 1 * mm});
            skCircle(sketch, "E25.128.9.0", {"center": v(45.9, 45.5) * mm, "radius": 1 * mm});
            skCircle(sketch, "E25.130.9.0", {"center": v(-6.6, 44) * mm, "radius": 1 * mm});
            skCircle(sketch, "E25.132.9.0", {"center": v(32.4, 44) * mm, "radius": 1 * mm});
            skCircle(sketch, "E25.134.9.0", {"center": v(-21.6, 44) * mm, "radius": 1 * mm});
            skCircle(sketch, "E25.136.9.0", {"center": v(6.9, 45.5) * mm, "radius": 1 * mm});
            skCircle(sketch, "E25.138.9.0", {"center": v(-20.1, 45.5) * mm, "radius": 1 * mm});
            skCircle(sketch, "E25.140.9.0", {"center": v(-41.1, 45.5) * mm, "radius": 1 * mm});
            skCircle(sketch, "E25.144.9.0", {"center": v(-47.1, 45.5) * mm, "radius": 1 * mm});
            skCircle(sketch, "E25.146.9.0", {"center": v(-42.6, 44) * mm, "radius": 1 * mm});
            skCircle(sketch, "E25.148.9.0", {"center": v(-45.6, 44) * mm, "radius": 1 * mm});
            skCircle(sketch, "E25.150.9.0", {"center": v(-48.6, 44) * mm, "radius": 1 * mm});
            skLineSegment(sketch, "E25.152.9.0", {"start": v(-50.1, 45.5) * mm, "end": v(-50.1, 46.5) * mm, "construction": true});
            skCircle(sketch, "E25.155.9.0", {"center": v(-50.1, 45.5) * mm, "radius": 1 * mm});
            skLineSegment(sketch, "E25.157.9.0", {"start": v(-51.1, 45.5) * mm, "end": v(-50.1, 45.5) * mm, "construction": true});
            skLineSegment(sketch, "E25.160.9.0", {"start": v(-51.1, 44) * mm, "end": v(-48.6, 44) * mm, "construction": true});
            skLineSegment(sketch, "E25.163.9.0", {"start": v(-48.6, 44) * mm, "end": v(-48.6, 46.5) * mm, "construction": true});
            skCircle(sketch, "E26.0.10.0", {"center": v(27.9, 42.5) * mm, "radius": 1 * mm});
            skCircle(sketch, "E26.2.10.0", {"center": v(-32.1, 42.5) * mm, "radius": 1 * mm});
            skCircle(sketch, "E26.4.10.0", {"center": v(36.9, 42.5) * mm, "radius": 1 * mm});
            skCircle(sketch, "E26.6.10.0", {"center": v(3.9, 42.5) * mm, "radius": 1 * mm});
            skCircle(sketch, "E26.8.10.0", {"center": v(54.9, 42.5) * mm, "radius": 1 * mm});
            skCircle(sketch, "E26.10.10.0", {"center": v(53.4, 41) * mm, "radius": 1 * mm});
            skCircle(sketch, "E26.12.10.0", {"center": v(29.4, 41) * mm, "radius": 1 * mm});
            skCircle(sketch, "E26.14.10.0", {"center": v(2.4, 41) * mm, "radius": 1 * mm});
            skCircle(sketch, "E26.18.10.0", {"center": v(18.9, 42.5) * mm, "radius": 1 * mm});
            skCircle(sketch, "E26.20.10.0", {"center": v(-30.6, 41) * mm, "radius": 1 * mm});
            skCircle(sketch, "E26.24.10.0", {"center": v(-44.1, 42.5) * mm, "radius": 1 * mm});
            skCircle(sketch, "E26.26.10.0", {"center": v(30.9, 42.5) * mm, "radius": 1 * mm});
            skCircle(sketch, "E26.28.10.0", {"center": v(-9.6, 41) * mm, "radius": 1 * mm});
            skCircle(sketch, "E26.32.10.0", {"center": v(-14.1, 42.5) * mm, "radius": 1 * mm});
            skCircle(sketch, "E26.34.10.0", {"center": v(-2.1, 42.5) * mm, "radius": 1 * mm});
            skCircle(sketch, "E26.36.10.0", {"center": v(9.9, 42.5) * mm, "radius": 1 * mm});
            skCircle(sketch, "E26.38.10.0", {"center": v(24.9, 42.5) * mm, "radius": 1 * mm});
            skCircle(sketch, "E26.40.10.0", {"center": v(5.4, 41) * mm, "radius": 1 * mm});
            skCircle(sketch, "E26.42.10.0", {"center": v(-23.1, 42.5) * mm, "radius": 1 * mm});
            skCircle(sketch, "E26.44.10.0", {"center": v(-5.1, 42.5) * mm, "radius": 1 * mm});
            skCircle(sketch, "E26.46.10.0", {"center": v(23.4, 41) * mm, "radius": 1 * mm});
            skCircle(sketch, "E26.48.10.0", {"center": v(42.9, 42.5) * mm, "radius": 1 * mm});
            skCircle(sketch, "E26.50.10.0", {"center": v(0.9, 42.5) * mm, "radius": 1 * mm});
            skCircle(sketch, "E26.52.10.0", {"center": v(-36.6, 41) * mm, "radius": 1 * mm});
            skCircle(sketch, "E26.54.10.0", {"center": v(41.4, 41) * mm, "radius": 1 * mm});
            skCircle(sketch, "E26.56.10.0", {"center": v(-12.6, 41) * mm, "radius": 1 * mm});
            skCircle(sketch, "E26.58.10.0", {"center": v(-26.1, 42.5) * mm, "radius": 1 * mm});
            skCircle(sketch, "E26.60.10.0", {"center": v(-8.1, 42.5) * mm, "radius": 1 * mm});
            skCircle(sketch, "E26.62.10.0", {"center": v(-27.6, 41) * mm, "radius": 1 * mm});
            skCircle(sketch, "E26.64.10.0", {"center": v(-29.1, 42.5) * mm, "radius": 1 * mm});
            skCircle(sketch, "E26.66.10.0", {"center": v(15.9, 42.5) * mm, "radius": 1 * mm});
            skCircle(sketch, "E26.68.10.0", {"center": v(-3.6, 41) * mm, "radius": 1 * mm});
            skCircle(sketch, "E26.70.10.0", {"center": v(-11.1, 42.5) * mm, "radius": 1 * mm});
            skCircle(sketch, "E26.72.10.0", {"center": v(44.4, 41) * mm, "radius": 1 * mm});
            skCircle(sketch, "E26.74.10.0", {"center": v(8.4, 41) * mm, "radius": 1 * mm});
            skCircle(sketch, "E26.76.10.0", {"center": v(33.9, 42.5) * mm, "radius": 1 * mm});
            skCircle(sketch, "E26.78.10.0", {"center": v(12.9, 42.5) * mm, "radius": 1 * mm});
            skCircle(sketch, "E26.80.10.0", {"center": v(-38.1, 42.5) * mm, "radius": 1 * mm});
            skCircle(sketch, "E26.82.10.0", {"center": v(-18.6, 41) * mm, "radius": 1 * mm});
            skCircle(sketch, "E26.84.10.0", {"center": v(-17.1, 42.5) * mm, "radius": 1 * mm});
            skCircle(sketch, "E26.86.10.0", {"center": v(48.9, 42.5) * mm, "radius": 1 * mm});
            skCircle(sketch, "E26.88.10.0", {"center": v(35.4, 41) * mm, "radius": 1 * mm});
            skCircle(sketch, "E26.90.10.0", {"center": v(11.4, 41) * mm, "radius": 1 * mm});
            skCircle(sketch, "E26.92.10.0", {"center": v(-24.6, 41) * mm, "radius": 1 * mm});
            skCircle(sketch, "E26.94.10.0", {"center": v(21.9, 42.5) * mm, "radius": 1 * mm});
            skCircle(sketch, "E26.96.10.0", {"center": v(50.4, 41) * mm, "radius": 1 * mm});
            skCircle(sketch, "E26.98.10.0", {"center": v(26.4, 41) * mm, "radius": 1 * mm});
            skCircle(sketch, "E26.100.10.0", {"center": v(20.4, 41) * mm, "radius": 1 * mm});
            skCircle(sketch, "E26.102.10.0", {"center": v(39.9, 42.5) * mm, "radius": 1 * mm});
            skCircle(sketch, "E26.104.10.0", {"center": v(-0.6, 41) * mm, "radius": 1 * mm});
            skCircle(sketch, "E26.106.10.0", {"center": v(47.4, 41) * mm, "radius": 1 * mm});
            skCircle(sketch, "E26.110.10.0", {"center": v(-39.6, 41) * mm, "radius": 1 * mm});
            skCircle(sketch, "E26.112.10.0", {"center": v(38.4, 41) * mm, "radius": 1 * mm});
            skCircle(sketch, "E26.114.10.0", {"center": v(-35.1, 42.5) * mm, "radius": 1 * mm});
            skCircle(sketch, "E26.116.10.0", {"center": v(17.4, 41) * mm, "radius": 1 * mm});
            skCircle(sketch, "E26.118.10.0", {"center": v(51.9, 42.5) * mm, "radius": 1 * mm});
            skCircle(sketch, "E26.120.10.0", {"center": v(-33.6, 41) * mm, "radius": 1 * mm});
            skCircle(sketch, "E26.124.10.0", {"center": v(-15.6, 41) * mm, "radius": 1 * mm});
            skCircle(sketch, "E26.126.10.0", {"center": v(14.4, 41) * mm, "radius": 1 * mm});
            skCircle(sketch, "E26.128.10.0", {"center": v(45.9, 42.5) * mm, "radius": 1 * mm});
            skCircle(sketch, "E26.130.10.0", {"center": v(-6.6, 41) * mm, "radius": 1 * mm});
            skCircle(sketch, "E26.132.10.0", {"center": v(32.4, 41) * mm, "radius": 1 * mm});
            skCircle(sketch, "E26.134.10.0", {"center": v(-21.6, 41) * mm, "radius": 1 * mm});
            skCircle(sketch, "E26.136.10.0", {"center": v(6.9, 42.5) * mm, "radius": 1 * mm});
            skCircle(sketch, "E26.138.10.0", {"center": v(-20.1, 42.5) * mm, "radius": 1 * mm});
            skCircle(sketch, "E26.140.10.0", {"center": v(-41.1, 42.5) * mm, "radius": 1 * mm});
            skCircle(sketch, "E26.144.10.0", {"center": v(-47.1, 42.5) * mm, "radius": 1 * mm});
            skCircle(sketch, "E26.146.10.0", {"center": v(-42.6, 41) * mm, "radius": 1 * mm});
            skCircle(sketch, "E26.148.10.0", {"center": v(-45.6, 41) * mm, "radius": 1 * mm});
            skCircle(sketch, "E26.150.10.0", {"center": v(-48.6, 41) * mm, "radius": 1 * mm});
            skLineSegment(sketch, "E26.152.10.0", {"start": v(-50.1, 42.5) * mm, "end": v(-50.1, 43.5) * mm, "construction": true});
            skCircle(sketch, "E26.155.10.0", {"center": v(-50.1, 42.5) * mm, "radius": 1 * mm});
            skLineSegment(sketch, "E26.157.10.0", {"start": v(-51.1, 42.5) * mm, "end": v(-50.1, 42.5) * mm, "construction": true});
            skLineSegment(sketch, "E26.160.10.0", {"start": v(-51.1, 41) * mm, "end": v(-48.6, 41) * mm, "construction": true});
            skLineSegment(sketch, "E26.163.10.0", {"start": v(-48.6, 41) * mm, "end": v(-48.6, 43.5) * mm, "construction": true});
            skCircle(sketch, "E26.0.11.0", {"center": v(27.9, 39.5) * mm, "radius": 1 * mm});
            skCircle(sketch, "E26.2.11.0", {"center": v(-32.1, 39.5) * mm, "radius": 1 * mm});
            skCircle(sketch, "E26.4.11.0", {"center": v(36.9, 39.5) * mm, "radius": 1 * mm});
            skCircle(sketch, "E26.6.11.0", {"center": v(3.9, 39.5) * mm, "radius": 1 * mm});
            skCircle(sketch, "E26.8.11.0", {"center": v(54.9, 39.5) * mm, "radius": 1 * mm});
            skCircle(sketch, "E26.10.11.0", {"center": v(53.4, 38) * mm, "radius": 1 * mm});
            skCircle(sketch, "E26.12.11.0", {"center": v(29.4, 38) * mm, "radius": 1 * mm});
            skCircle(sketch, "E26.14.11.0", {"center": v(2.4, 38) * mm, "radius": 1 * mm});
            skCircle(sketch, "E26.18.11.0", {"center": v(18.9, 39.5) * mm, "radius": 1 * mm});
            skCircle(sketch, "E26.20.11.0", {"center": v(-30.6, 38) * mm, "radius": 1 * mm});
            skCircle(sketch, "E26.24.11.0", {"center": v(-44.1, 39.5) * mm, "radius": 1 * mm});
            skCircle(sketch, "E26.26.11.0", {"center": v(30.9, 39.5) * mm, "radius": 1 * mm});
            skCircle(sketch, "E26.28.11.0", {"center": v(-9.6, 38) * mm, "radius": 1 * mm});
            skCircle(sketch, "E26.32.11.0", {"center": v(-14.1, 39.5) * mm, "radius": 1 * mm});
            skCircle(sketch, "E26.34.11.0", {"center": v(-2.1, 39.5) * mm, "radius": 1 * mm});
            skCircle(sketch, "E26.36.11.0", {"center": v(9.9, 39.5) * mm, "radius": 1 * mm});
            skCircle(sketch, "E26.38.11.0", {"center": v(24.9, 39.5) * mm, "radius": 1 * mm});
            skCircle(sketch, "E26.40.11.0", {"center": v(5.4, 38) * mm, "radius": 1 * mm});
            skCircle(sketch, "E26.42.11.0", {"center": v(-23.1, 39.5) * mm, "radius": 1 * mm});
            skCircle(sketch, "E26.44.11.0", {"center": v(-5.1, 39.5) * mm, "radius": 1 * mm});
            skCircle(sketch, "E26.46.11.0", {"center": v(23.4, 38) * mm, "radius": 1 * mm});
            skCircle(sketch, "E26.48.11.0", {"center": v(42.9, 39.5) * mm, "radius": 1 * mm});
            skCircle(sketch, "E26.50.11.0", {"center": v(0.9, 39.5) * mm, "radius": 1 * mm});
            skCircle(sketch, "E26.52.11.0", {"center": v(-36.6, 38) * mm, "radius": 1 * mm});
            skCircle(sketch, "E26.54.11.0", {"center": v(41.4, 38) * mm, "radius": 1 * mm});
            skCircle(sketch, "E26.56.11.0", {"center": v(-12.6, 38) * mm, "radius": 1 * mm});
            skCircle(sketch, "E26.58.11.0", {"center": v(-26.1, 39.5) * mm, "radius": 1 * mm});
            skCircle(sketch, "E26.60.11.0", {"center": v(-8.1, 39.5) * mm, "radius": 1 * mm});
            skCircle(sketch, "E26.62.11.0", {"center": v(-27.6, 38) * mm, "radius": 1 * mm});
            skCircle(sketch, "E26.64.11.0", {"center": v(-29.1, 39.5) * mm, "radius": 1 * mm});
            skCircle(sketch, "E26.66.11.0", {"center": v(15.9, 39.5) * mm, "radius": 1 * mm});
            skCircle(sketch, "E26.68.11.0", {"center": v(-3.6, 38) * mm, "radius": 1 * mm});
            skCircle(sketch, "E26.70.11.0", {"center": v(-11.1, 39.5) * mm, "radius": 1 * mm});
            skCircle(sketch, "E26.72.11.0", {"center": v(44.4, 38) * mm, "radius": 1 * mm});
            skCircle(sketch, "E26.74.11.0", {"center": v(8.4, 38) * mm, "radius": 1 * mm});
            skCircle(sketch, "E26.76.11.0", {"center": v(33.9, 39.5) * mm, "radius": 1 * mm});
            skCircle(sketch, "E26.78.11.0", {"center": v(12.9, 39.5) * mm, "radius": 1 * mm});
            skCircle(sketch, "E26.80.11.0", {"center": v(-38.1, 39.5) * mm, "radius": 1 * mm});
            skCircle(sketch, "E26.82.11.0", {"center": v(-18.6, 38) * mm, "radius": 1 * mm});
            skCircle(sketch, "E26.84.11.0", {"center": v(-17.1, 39.5) * mm, "radius": 1 * mm});
            skCircle(sketch, "E26.86.11.0", {"center": v(48.9, 39.5) * mm, "radius": 1 * mm});
            skCircle(sketch, "E26.88.11.0", {"center": v(35.4, 38) * mm, "radius": 1 * mm});
            skCircle(sketch, "E26.90.11.0", {"center": v(11.4, 38) * mm, "radius": 1 * mm});
            skCircle(sketch, "E26.92.11.0", {"center": v(-24.6, 38) * mm, "radius": 1 * mm});
            skCircle(sketch, "E26.94.11.0", {"center": v(21.9, 39.5) * mm, "radius": 1 * mm});
            skCircle(sketch, "E26.96.11.0", {"center": v(50.4, 38) * mm, "radius": 1 * mm});
            skCircle(sketch, "E26.98.11.0", {"center": v(26.4, 38) * mm, "radius": 1 * mm});
            skCircle(sketch, "E26.100.11.0", {"center": v(20.4, 38) * mm, "radius": 1 * mm});
            skCircle(sketch, "E26.102.11.0", {"center": v(39.9, 39.5) * mm, "radius": 1 * mm});
            skCircle(sketch, "E26.104.11.0", {"center": v(-0.6, 38) * mm, "radius": 1 * mm});
            skCircle(sketch, "E26.106.11.0", {"center": v(47.4, 38) * mm, "radius": 1 * mm});
            skCircle(sketch, "E26.110.11.0", {"center": v(-39.6, 38) * mm, "radius": 1 * mm});
            skCircle(sketch, "E26.112.11.0", {"center": v(38.4, 38) * mm, "radius": 1 * mm});
            skCircle(sketch, "E26.114.11.0", {"center": v(-35.1, 39.5) * mm, "radius": 1 * mm});
            skCircle(sketch, "E26.116.11.0", {"center": v(17.4, 38) * mm, "radius": 1 * mm});
            skCircle(sketch, "E26.118.11.0", {"center": v(51.9, 39.5) * mm, "radius": 1 * mm});
            skCircle(sketch, "E26.120.11.0", {"center": v(-33.6, 38) * mm, "radius": 1 * mm});
            skCircle(sketch, "E26.124.11.0", {"center": v(-15.6, 38) * mm, "radius": 1 * mm});
            skCircle(sketch, "E26.126.11.0", {"center": v(14.4, 38) * mm, "radius": 1 * mm});
            skCircle(sketch, "E26.128.11.0", {"center": v(45.9, 39.5) * mm, "radius": 1 * mm});
            skCircle(sketch, "E26.130.11.0", {"center": v(-6.6, 38) * mm, "radius": 1 * mm});
            skCircle(sketch, "E26.132.11.0", {"center": v(32.4, 38) * mm, "radius": 1 * mm});
            skCircle(sketch, "E26.134.11.0", {"center": v(-21.6, 38) * mm, "radius": 1 * mm});
            skCircle(sketch, "E26.136.11.0", {"center": v(6.9, 39.5) * mm, "radius": 1 * mm});
            skCircle(sketch, "E26.138.11.0", {"center": v(-20.1, 39.5) * mm, "radius": 1 * mm});
            skCircle(sketch, "E26.140.11.0", {"center": v(-41.1, 39.5) * mm, "radius": 1 * mm});
            skCircle(sketch, "E26.144.11.0", {"center": v(-47.1, 39.5) * mm, "radius": 1 * mm});
            skCircle(sketch, "E26.146.11.0", {"center": v(-42.6, 38) * mm, "radius": 1 * mm});
            skCircle(sketch, "E26.148.11.0", {"center": v(-45.6, 38) * mm, "radius": 1 * mm});
            skCircle(sketch, "E26.150.11.0", {"center": v(-48.6, 38) * mm, "radius": 1 * mm});
            skLineSegment(sketch, "E26.152.11.0", {"start": v(-50.1, 39.5) * mm, "end": v(-50.1, 40.5) * mm, "construction": true});
            skCircle(sketch, "E26.155.11.0", {"center": v(-50.1, 39.5) * mm, "radius": 1 * mm});
            skLineSegment(sketch, "E26.157.11.0", {"start": v(-51.1, 39.5) * mm, "end": v(-50.1, 39.5) * mm, "construction": true});
            skLineSegment(sketch, "E26.160.11.0", {"start": v(-51.1, 38) * mm, "end": v(-48.6, 38) * mm, "construction": true});
            skLineSegment(sketch, "E26.163.11.0", {"start": v(-48.6, 38) * mm, "end": v(-48.6, 40.5) * mm, "construction": true});
            skCircle(sketch, "E26.0.12.0", {"center": v(27.9, 36.5) * mm, "radius": 1 * mm});
            skCircle(sketch, "E26.2.12.0", {"center": v(-32.1, 36.5) * mm, "radius": 1 * mm});
            skCircle(sketch, "E26.4.12.0", {"center": v(36.9, 36.5) * mm, "radius": 1 * mm});
            skCircle(sketch, "E26.6.12.0", {"center": v(3.9, 36.5) * mm, "radius": 1 * mm});
            skCircle(sketch, "E26.8.12.0", {"center": v(54.9, 36.5) * mm, "radius": 1 * mm});
            skCircle(sketch, "E26.10.12.0", {"center": v(53.4, 35) * mm, "radius": 1 * mm});
            skCircle(sketch, "E26.12.12.0", {"center": v(29.4, 35) * mm, "radius": 1 * mm});
            skCircle(sketch, "E26.14.12.0", {"center": v(2.4, 35) * mm, "radius": 1 * mm});
            skCircle(sketch, "E26.18.12.0", {"center": v(18.9, 36.5) * mm, "radius": 1 * mm});
            skCircle(sketch, "E26.20.12.0", {"center": v(-30.6, 35) * mm, "radius": 1 * mm});
            skCircle(sketch, "E26.24.12.0", {"center": v(-44.1, 36.5) * mm, "radius": 1 * mm});
            skCircle(sketch, "E26.26.12.0", {"center": v(30.9, 36.5) * mm, "radius": 1 * mm});
            skCircle(sketch, "E26.28.12.0", {"center": v(-9.6, 35) * mm, "radius": 1 * mm});
            skCircle(sketch, "E26.32.12.0", {"center": v(-14.1, 36.5) * mm, "radius": 1 * mm});
            skCircle(sketch, "E26.34.12.0", {"center": v(-2.1, 36.5) * mm, "radius": 1 * mm});
            skCircle(sketch, "E26.36.12.0", {"center": v(9.9, 36.5) * mm, "radius": 1 * mm});
            skCircle(sketch, "E26.38.12.0", {"center": v(24.9, 36.5) * mm, "radius": 1 * mm});
            skCircle(sketch, "E26.40.12.0", {"center": v(5.4, 35) * mm, "radius": 1 * mm});
            skCircle(sketch, "E26.42.12.0", {"center": v(-23.1, 36.5) * mm, "radius": 1 * mm});
            skCircle(sketch, "E26.44.12.0", {"center": v(-5.1, 36.5) * mm, "radius": 1 * mm});
            skCircle(sketch, "E26.46.12.0", {"center": v(23.4, 35) * mm, "radius": 1 * mm});
            skCircle(sketch, "E26.48.12.0", {"center": v(42.9, 36.5) * mm, "radius": 1 * mm});
            skCircle(sketch, "E26.50.12.0", {"center": v(0.9, 36.5) * mm, "radius": 1 * mm});
            skCircle(sketch, "E26.52.12.0", {"center": v(-36.6, 35) * mm, "radius": 1 * mm});
            skCircle(sketch, "E26.54.12.0", {"center": v(41.4, 35) * mm, "radius": 1 * mm});
            skCircle(sketch, "E26.56.12.0", {"center": v(-12.6, 35) * mm, "radius": 1 * mm});
            skCircle(sketch, "E26.58.12.0", {"center": v(-26.1, 36.5) * mm, "radius": 1 * mm});
            skCircle(sketch, "E26.60.12.0", {"center": v(-8.1, 36.5) * mm, "radius": 1 * mm});
            skCircle(sketch, "E26.62.12.0", {"center": v(-27.6, 35) * mm, "radius": 1 * mm});
            skCircle(sketch, "E26.64.12.0", {"center": v(-29.1, 36.5) * mm, "radius": 1 * mm});
            skCircle(sketch, "E26.66.12.0", {"center": v(15.9, 36.5) * mm, "radius": 1 * mm});
            skCircle(sketch, "E26.68.12.0", {"center": v(-3.6, 35) * mm, "radius": 1 * mm});
            skCircle(sketch, "E26.70.12.0", {"center": v(-11.1, 36.5) * mm, "radius": 1 * mm});
            skCircle(sketch, "E26.72.12.0", {"center": v(44.4, 35) * mm, "radius": 1 * mm});
            skCircle(sketch, "E26.74.12.0", {"center": v(8.4, 35) * mm, "radius": 1 * mm});
            skCircle(sketch, "E26.76.12.0", {"center": v(33.9, 36.5) * mm, "radius": 1 * mm});
            skCircle(sketch, "E26.78.12.0", {"center": v(12.9, 36.5) * mm, "radius": 1 * mm});
            skCircle(sketch, "E26.80.12.0", {"center": v(-38.1, 36.5) * mm, "radius": 1 * mm});
            skCircle(sketch, "E26.82.12.0", {"center": v(-18.6, 35) * mm, "radius": 1 * mm});
            skCircle(sketch, "E26.84.12.0", {"center": v(-17.1, 36.5) * mm, "radius": 1 * mm});
            skCircle(sketch, "E26.86.12.0", {"center": v(48.9, 36.5) * mm, "radius": 1 * mm});
            skCircle(sketch, "E26.88.12.0", {"center": v(35.4, 35) * mm, "radius": 1 * mm});
            skCircle(sketch, "E26.90.12.0", {"center": v(11.4, 35) * mm, "radius": 1 * mm});
            skCircle(sketch, "E26.92.12.0", {"center": v(-24.6, 35) * mm, "radius": 1 * mm});
            skCircle(sketch, "E26.94.12.0", {"center": v(21.9, 36.5) * mm, "radius": 1 * mm});
            skCircle(sketch, "E26.96.12.0", {"center": v(50.4, 35) * mm, "radius": 1 * mm});
            skCircle(sketch, "E26.98.12.0", {"center": v(26.4, 35) * mm, "radius": 1 * mm});
            skCircle(sketch, "E26.100.12.0", {"center": v(20.4, 35) * mm, "radius": 1 * mm});
            skCircle(sketch, "E26.102.12.0", {"center": v(39.9, 36.5) * mm, "radius": 1 * mm});
            skCircle(sketch, "E26.104.12.0", {"center": v(-0.6, 35) * mm, "radius": 1 * mm});
            skCircle(sketch, "E26.106.12.0", {"center": v(47.4, 35) * mm, "radius": 1 * mm});
            skCircle(sketch, "E26.110.12.0", {"center": v(-39.6, 35) * mm, "radius": 1 * mm});
            skCircle(sketch, "E26.112.12.0", {"center": v(38.4, 35) * mm, "radius": 1 * mm});
            skCircle(sketch, "E26.114.12.0", {"center": v(-35.1, 36.5) * mm, "radius": 1 * mm});
            skCircle(sketch, "E26.116.12.0", {"center": v(17.4, 35) * mm, "radius": 1 * mm});
            skCircle(sketch, "E26.118.12.0", {"center": v(51.9, 36.5) * mm, "radius": 1 * mm});
            skCircle(sketch, "E26.120.12.0", {"center": v(-33.6, 35) * mm, "radius": 1 * mm});
            skCircle(sketch, "E26.124.12.0", {"center": v(-15.6, 35) * mm, "radius": 1 * mm});
            skCircle(sketch, "E26.126.12.0", {"center": v(14.4, 35) * mm, "radius": 1 * mm});
            skCircle(sketch, "E26.128.12.0", {"center": v(45.9, 36.5) * mm, "radius": 1 * mm});
            skCircle(sketch, "E26.130.12.0", {"center": v(-6.6, 35) * mm, "radius": 1 * mm});
            skCircle(sketch, "E26.132.12.0", {"center": v(32.4, 35) * mm, "radius": 1 * mm});
            skCircle(sketch, "E26.134.12.0", {"center": v(-21.6, 35) * mm, "radius": 1 * mm});
            skCircle(sketch, "E26.136.12.0", {"center": v(6.9, 36.5) * mm, "radius": 1 * mm});
            skCircle(sketch, "E26.138.12.0", {"center": v(-20.1, 36.5) * mm, "radius": 1 * mm});
            skCircle(sketch, "E26.140.12.0", {"center": v(-41.1, 36.5) * mm, "radius": 1 * mm});
            skCircle(sketch, "E26.144.12.0", {"center": v(-47.1, 36.5) * mm, "radius": 1 * mm});
            skCircle(sketch, "E26.146.12.0", {"center": v(-42.6, 35) * mm, "radius": 1 * mm});
            skCircle(sketch, "E26.148.12.0", {"center": v(-45.6, 35) * mm, "radius": 1 * mm});
            skCircle(sketch, "E26.150.12.0", {"center": v(-48.6, 35) * mm, "radius": 1 * mm});
            skLineSegment(sketch, "E26.152.12.0", {"start": v(-50.1, 36.5) * mm, "end": v(-50.1, 37.5) * mm, "construction": true});
            skCircle(sketch, "E26.155.12.0", {"center": v(-50.1, 36.5) * mm, "radius": 1 * mm});
            skLineSegment(sketch, "E26.157.12.0", {"start": v(-51.1, 36.5) * mm, "end": v(-50.1, 36.5) * mm, "construction": true});
            skLineSegment(sketch, "E26.160.12.0", {"start": v(-51.1, 35) * mm, "end": v(-48.6, 35) * mm, "construction": true});
            skLineSegment(sketch, "E26.163.12.0", {"start": v(-48.6, 35) * mm, "end": v(-48.6, 37.5) * mm, "construction": true});
            skCircle(sketch, "E26.0.13.0", {"center": v(27.9, 33.5) * mm, "radius": 1 * mm});
            skCircle(sketch, "E26.2.13.0", {"center": v(-32.1, 33.5) * mm, "radius": 1 * mm});
            skCircle(sketch, "E26.4.13.0", {"center": v(36.9, 33.5) * mm, "radius": 1 * mm});
            skCircle(sketch, "E26.6.13.0", {"center": v(3.9, 33.5) * mm, "radius": 1 * mm});
            skCircle(sketch, "E26.8.13.0", {"center": v(54.9, 33.5) * mm, "radius": 1 * mm});
            skCircle(sketch, "E26.10.13.0", {"center": v(53.4, 32) * mm, "radius": 1 * mm});
            skCircle(sketch, "E26.12.13.0", {"center": v(29.4, 32) * mm, "radius": 1 * mm});
            skCircle(sketch, "E26.14.13.0", {"center": v(2.4, 32) * mm, "radius": 1 * mm});
            skCircle(sketch, "E26.18.13.0", {"center": v(18.9, 33.5) * mm, "radius": 1 * mm});
            skCircle(sketch, "E26.20.13.0", {"center": v(-30.6, 32) * mm, "radius": 1 * mm});
            skCircle(sketch, "E26.24.13.0", {"center": v(-44.1, 33.5) * mm, "radius": 1 * mm});
            skCircle(sketch, "E26.26.13.0", {"center": v(30.9, 33.5) * mm, "radius": 1 * mm});
            skCircle(sketch, "E26.28.13.0", {"center": v(-9.6, 32) * mm, "radius": 1 * mm});
            skCircle(sketch, "E26.32.13.0", {"center": v(-14.1, 33.5) * mm, "radius": 1 * mm});
            skCircle(sketch, "E26.34.13.0", {"center": v(-2.1, 33.5) * mm, "radius": 1 * mm});
            skCircle(sketch, "E26.36.13.0", {"center": v(9.9, 33.5) * mm, "radius": 1 * mm});
            skCircle(sketch, "E26.38.13.0", {"center": v(24.9, 33.5) * mm, "radius": 1 * mm});
            skCircle(sketch, "E26.40.13.0", {"center": v(5.4, 32) * mm, "radius": 1 * mm});
            skCircle(sketch, "E26.42.13.0", {"center": v(-23.1, 33.5) * mm, "radius": 1 * mm});
            skCircle(sketch, "E26.44.13.0", {"center": v(-5.1, 33.5) * mm, "radius": 1 * mm});
            skCircle(sketch, "E26.46.13.0", {"center": v(23.4, 32) * mm, "radius": 1 * mm});
            skCircle(sketch, "E26.48.13.0", {"center": v(42.9, 33.5) * mm, "radius": 1 * mm});
            skCircle(sketch, "E26.50.13.0", {"center": v(0.9, 33.5) * mm, "radius": 1 * mm});
            skCircle(sketch, "E26.52.13.0", {"center": v(-36.6, 32) * mm, "radius": 1 * mm});
            skCircle(sketch, "E26.54.13.0", {"center": v(41.4, 32) * mm, "radius": 1 * mm});
            skCircle(sketch, "E26.56.13.0", {"center": v(-12.6, 32) * mm, "radius": 1 * mm});
            skCircle(sketch, "E26.58.13.0", {"center": v(-26.1, 33.5) * mm, "radius": 1 * mm});
            skCircle(sketch, "E26.60.13.0", {"center": v(-8.1, 33.5) * mm, "radius": 1 * mm});
            skCircle(sketch, "E26.62.13.0", {"center": v(-27.6, 32) * mm, "radius": 1 * mm});
            skCircle(sketch, "E26.64.13.0", {"center": v(-29.1, 33.5) * mm, "radius": 1 * mm});
            skCircle(sketch, "E26.66.13.0", {"center": v(15.9, 33.5) * mm, "radius": 1 * mm});
            skCircle(sketch, "E26.68.13.0", {"center": v(-3.6, 32) * mm, "radius": 1 * mm});
            skCircle(sketch, "E26.70.13.0", {"center": v(-11.1, 33.5) * mm, "radius": 1 * mm});
            skCircle(sketch, "E26.72.13.0", {"center": v(44.4, 32) * mm, "radius": 1 * mm});
            skCircle(sketch, "E26.74.13.0", {"center": v(8.4, 32) * mm, "radius": 1 * mm});
            skCircle(sketch, "E26.76.13.0", {"center": v(33.9, 33.5) * mm, "radius": 1 * mm});
            skCircle(sketch, "E26.78.13.0", {"center": v(12.9, 33.5) * mm, "radius": 1 * mm});
            skCircle(sketch, "E26.80.13.0", {"center": v(-38.1, 33.5) * mm, "radius": 1 * mm});
            skCircle(sketch, "E26.82.13.0", {"center": v(-18.6, 32) * mm, "radius": 1 * mm});
            skCircle(sketch, "E26.84.13.0", {"center": v(-17.1, 33.5) * mm, "radius": 1 * mm});
            skCircle(sketch, "E26.86.13.0", {"center": v(48.9, 33.5) * mm, "radius": 1 * mm});
            skCircle(sketch, "E26.88.13.0", {"center": v(35.4, 32) * mm, "radius": 1 * mm});
            skCircle(sketch, "E26.90.13.0", {"center": v(11.4, 32) * mm, "radius": 1 * mm});
            skCircle(sketch, "E26.92.13.0", {"center": v(-24.6, 32) * mm, "radius": 1 * mm});
            skCircle(sketch, "E26.94.13.0", {"center": v(21.9, 33.5) * mm, "radius": 1 * mm});
            skCircle(sketch, "E26.96.13.0", {"center": v(50.4, 32) * mm, "radius": 1 * mm});
            skCircle(sketch, "E26.98.13.0", {"center": v(26.4, 32) * mm, "radius": 1 * mm});
            skCircle(sketch, "E26.100.13.0", {"center": v(20.4, 32) * mm, "radius": 1 * mm});
            skCircle(sketch, "E26.102.13.0", {"center": v(39.9, 33.5) * mm, "radius": 1 * mm});
            skCircle(sketch, "E26.104.13.0", {"center": v(-0.6, 32) * mm, "radius": 1 * mm});
            skCircle(sketch, "E26.106.13.0", {"center": v(47.4, 32) * mm, "radius": 1 * mm});
            skCircle(sketch, "E26.110.13.0", {"center": v(-39.6, 32) * mm, "radius": 1 * mm});
            skCircle(sketch, "E26.112.13.0", {"center": v(38.4, 32) * mm, "radius": 1 * mm});
            skCircle(sketch, "E26.114.13.0", {"center": v(-35.1, 33.5) * mm, "radius": 1 * mm});
            skCircle(sketch, "E26.116.13.0", {"center": v(17.4, 32) * mm, "radius": 1 * mm});
            skCircle(sketch, "E26.118.13.0", {"center": v(51.9, 33.5) * mm, "radius": 1 * mm});
            skCircle(sketch, "E26.120.13.0", {"center": v(-33.6, 32) * mm, "radius": 1 * mm});
            skCircle(sketch, "E26.124.13.0", {"center": v(-15.6, 32) * mm, "radius": 1 * mm});
            skCircle(sketch, "E26.126.13.0", {"center": v(14.4, 32) * mm, "radius": 1 * mm});
            skCircle(sketch, "E26.128.13.0", {"center": v(45.9, 33.5) * mm, "radius": 1 * mm});
            skCircle(sketch, "E26.130.13.0", {"center": v(-6.6, 32) * mm, "radius": 1 * mm});
            skCircle(sketch, "E26.132.13.0", {"center": v(32.4, 32) * mm, "radius": 1 * mm});
            skCircle(sketch, "E26.134.13.0", {"center": v(-21.6, 32) * mm, "radius": 1 * mm});
            skCircle(sketch, "E26.136.13.0", {"center": v(6.9, 33.5) * mm, "radius": 1 * mm});
            skCircle(sketch, "E26.138.13.0", {"center": v(-20.1, 33.5) * mm, "radius": 1 * mm});
            skCircle(sketch, "E26.140.13.0", {"center": v(-41.1, 33.5) * mm, "radius": 1 * mm});
            skCircle(sketch, "E26.144.13.0", {"center": v(-47.1, 33.5) * mm, "radius": 1 * mm});
            skCircle(sketch, "E26.146.13.0", {"center": v(-42.6, 32) * mm, "radius": 1 * mm});
            skCircle(sketch, "E26.148.13.0", {"center": v(-45.6, 32) * mm, "radius": 1 * mm});
            skCircle(sketch, "E26.150.13.0", {"center": v(-48.6, 32) * mm, "radius": 1 * mm});
            skLineSegment(sketch, "E26.152.13.0", {"start": v(-50.1, 33.5) * mm, "end": v(-50.1, 34.5) * mm, "construction": true});
            skCircle(sketch, "E26.155.13.0", {"center": v(-50.1, 33.5) * mm, "radius": 1 * mm});
            skLineSegment(sketch, "E26.157.13.0", {"start": v(-51.1, 33.5) * mm, "end": v(-50.1, 33.5) * mm, "construction": true});
            skLineSegment(sketch, "E26.160.13.0", {"start": v(-51.1, 32) * mm, "end": v(-48.6, 32) * mm, "construction": true});
            skLineSegment(sketch, "E26.163.13.0", {"start": v(-48.6, 32) * mm, "end": v(-48.6, 34.5) * mm, "construction": true});
            skCircle(sketch, "E26.0.14.0", {"center": v(27.9, 30.5) * mm, "radius": 1 * mm});
            skCircle(sketch, "E26.2.14.0", {"center": v(-32.1, 30.5) * mm, "radius": 1 * mm});
            skCircle(sketch, "E26.4.14.0", {"center": v(36.9, 30.5) * mm, "radius": 1 * mm});
            skCircle(sketch, "E26.6.14.0", {"center": v(3.9, 30.5) * mm, "radius": 1 * mm});
            skCircle(sketch, "E26.8.14.0", {"center": v(54.9, 30.5) * mm, "radius": 1 * mm});
            skCircle(sketch, "E26.10.14.0", {"center": v(53.4, 29) * mm, "radius": 1 * mm});
            skCircle(sketch, "E26.12.14.0", {"center": v(29.4, 29) * mm, "radius": 1 * mm});
            skCircle(sketch, "E26.14.14.0", {"center": v(2.4, 29) * mm, "radius": 1 * mm});
            skCircle(sketch, "E26.18.14.0", {"center": v(18.9, 30.5) * mm, "radius": 1 * mm});
            skCircle(sketch, "E26.20.14.0", {"center": v(-30.6, 29) * mm, "radius": 1 * mm});
            skCircle(sketch, "E26.24.14.0", {"center": v(-44.1, 30.5) * mm, "radius": 1 * mm});
            skCircle(sketch, "E26.26.14.0", {"center": v(30.9, 30.5) * mm, "radius": 1 * mm});
            skCircle(sketch, "E26.28.14.0", {"center": v(-9.6, 29) * mm, "radius": 1 * mm});
            skCircle(sketch, "E26.32.14.0", {"center": v(-14.1, 30.5) * mm, "radius": 1 * mm});
            skCircle(sketch, "E26.34.14.0", {"center": v(-2.1, 30.5) * mm, "radius": 1 * mm});
            skCircle(sketch, "E26.36.14.0", {"center": v(9.9, 30.5) * mm, "radius": 1 * mm});
            skCircle(sketch, "E26.38.14.0", {"center": v(24.9, 30.5) * mm, "radius": 1 * mm});
            skCircle(sketch, "E26.40.14.0", {"center": v(5.4, 29) * mm, "radius": 1 * mm});
            skCircle(sketch, "E26.42.14.0", {"center": v(-23.1, 30.5) * mm, "radius": 1 * mm});
            skCircle(sketch, "E26.44.14.0", {"center": v(-5.1, 30.5) * mm, "radius": 1 * mm});
            skCircle(sketch, "E26.46.14.0", {"center": v(23.4, 29) * mm, "radius": 1 * mm});
            skCircle(sketch, "E26.48.14.0", {"center": v(42.9, 30.5) * mm, "radius": 1 * mm});
            skCircle(sketch, "E26.50.14.0", {"center": v(0.9, 30.5) * mm, "radius": 1 * mm});
            skCircle(sketch, "E26.52.14.0", {"center": v(-36.6, 29) * mm, "radius": 1 * mm});
            skCircle(sketch, "E26.54.14.0", {"center": v(41.4, 29) * mm, "radius": 1 * mm});
            skCircle(sketch, "E26.56.14.0", {"center": v(-12.6, 29) * mm, "radius": 1 * mm});
            skCircle(sketch, "E26.58.14.0", {"center": v(-26.1, 30.5) * mm, "radius": 1 * mm});
            skCircle(sketch, "E26.60.14.0", {"center": v(-8.1, 30.5) * mm, "radius": 1 * mm});
            skCircle(sketch, "E26.62.14.0", {"center": v(-27.6, 29) * mm, "radius": 1 * mm});
            skCircle(sketch, "E26.64.14.0", {"center": v(-29.1, 30.5) * mm, "radius": 1 * mm});
            skCircle(sketch, "E26.66.14.0", {"center": v(15.9, 30.5) * mm, "radius": 1 * mm});
            skCircle(sketch, "E26.68.14.0", {"center": v(-3.6, 29) * mm, "radius": 1 * mm});
            skCircle(sketch, "E26.70.14.0", {"center": v(-11.1, 30.5) * mm, "radius": 1 * mm});
            skCircle(sketch, "E26.72.14.0", {"center": v(44.4, 29) * mm, "radius": 1 * mm});
            skCircle(sketch, "E26.74.14.0", {"center": v(8.4, 29) * mm, "radius": 1 * mm});
            skCircle(sketch, "E26.76.14.0", {"center": v(33.9, 30.5) * mm, "radius": 1 * mm});
            skCircle(sketch, "E26.78.14.0", {"center": v(12.9, 30.5) * mm, "radius": 1 * mm});
            skCircle(sketch, "E26.80.14.0", {"center": v(-38.1, 30.5) * mm, "radius": 1 * mm});
            skCircle(sketch, "E26.82.14.0", {"center": v(-18.6, 29) * mm, "radius": 1 * mm});
            skCircle(sketch, "E26.84.14.0", {"center": v(-17.1, 30.5) * mm, "radius": 1 * mm});
            skCircle(sketch, "E26.86.14.0", {"center": v(48.9, 30.5) * mm, "radius": 1 * mm});
            skCircle(sketch, "E26.88.14.0", {"center": v(35.4, 29) * mm, "radius": 1 * mm});
            skCircle(sketch, "E26.90.14.0", {"center": v(11.4, 29) * mm, "radius": 1 * mm});
            skCircle(sketch, "E26.92.14.0", {"center": v(-24.6, 29) * mm, "radius": 1 * mm});
            skCircle(sketch, "E26.94.14.0", {"center": v(21.9, 30.5) * mm, "radius": 1 * mm});
            skCircle(sketch, "E26.96.14.0", {"center": v(50.4, 29) * mm, "radius": 1 * mm});
            skCircle(sketch, "E26.98.14.0", {"center": v(26.4, 29) * mm, "radius": 1 * mm});
            skCircle(sketch, "E26.100.14.0", {"center": v(20.4, 29) * mm, "radius": 1 * mm});
            skCircle(sketch, "E26.102.14.0", {"center": v(39.9, 30.5) * mm, "radius": 1 * mm});
            skCircle(sketch, "E26.104.14.0", {"center": v(-0.6, 29) * mm, "radius": 1 * mm});
            skCircle(sketch, "E26.106.14.0", {"center": v(47.4, 29) * mm, "radius": 1 * mm});
            skCircle(sketch, "E26.110.14.0", {"center": v(-39.6, 29) * mm, "radius": 1 * mm});
            skCircle(sketch, "E26.112.14.0", {"center": v(38.4, 29) * mm, "radius": 1 * mm});
            skCircle(sketch, "E26.114.14.0", {"center": v(-35.1, 30.5) * mm, "radius": 1 * mm});
            skCircle(sketch, "E26.116.14.0", {"center": v(17.4, 29) * mm, "radius": 1 * mm});
            skCircle(sketch, "E26.118.14.0", {"center": v(51.9, 30.5) * mm, "radius": 1 * mm});
            skCircle(sketch, "E26.120.14.0", {"center": v(-33.6, 29) * mm, "radius": 1 * mm});
            skCircle(sketch, "E26.124.14.0", {"center": v(-15.6, 29) * mm, "radius": 1 * mm});
            skCircle(sketch, "E26.126.14.0", {"center": v(14.4, 29) * mm, "radius": 1 * mm});
            skCircle(sketch, "E26.128.14.0", {"center": v(45.9, 30.5) * mm, "radius": 1 * mm});
            skCircle(sketch, "E26.130.14.0", {"center": v(-6.6, 29) * mm, "radius": 1 * mm});
            skCircle(sketch, "E26.132.14.0", {"center": v(32.4, 29) * mm, "radius": 1 * mm});
            skCircle(sketch, "E26.134.14.0", {"center": v(-21.6, 29) * mm, "radius": 1 * mm});
            skCircle(sketch, "E26.136.14.0", {"center": v(6.9, 30.5) * mm, "radius": 1 * mm});
            skCircle(sketch, "E26.138.14.0", {"center": v(-20.1, 30.5) * mm, "radius": 1 * mm});
            skCircle(sketch, "E26.140.14.0", {"center": v(-41.1, 30.5) * mm, "radius": 1 * mm});
            skCircle(sketch, "E26.144.14.0", {"center": v(-47.1, 30.5) * mm, "radius": 1 * mm});
            skCircle(sketch, "E26.146.14.0", {"center": v(-42.6, 29) * mm, "radius": 1 * mm});
            skCircle(sketch, "E26.148.14.0", {"center": v(-45.6, 29) * mm, "radius": 1 * mm});
            skCircle(sketch, "E26.150.14.0", {"center": v(-48.6, 29) * mm, "radius": 1 * mm});
            skLineSegment(sketch, "E26.152.14.0", {"start": v(-50.1, 30.5) * mm, "end": v(-50.1, 31.5) * mm, "construction": true});
            skCircle(sketch, "E26.155.14.0", {"center": v(-50.1, 30.5) * mm, "radius": 1 * mm});
            skLineSegment(sketch, "E26.157.14.0", {"start": v(-51.1, 30.5) * mm, "end": v(-50.1, 30.5) * mm, "construction": true});
            skLineSegment(sketch, "E26.160.14.0", {"start": v(-51.1, 29) * mm, "end": v(-48.6, 29) * mm, "construction": true});
            skLineSegment(sketch, "E26.163.14.0", {"start": v(-48.6, 29) * mm, "end": v(-48.6, 31.5) * mm, "construction": true});
            skCircle(sketch, "E26.0.15.0", {"center": v(27.9, 27.5) * mm, "radius": 1 * mm});
            skCircle(sketch, "E26.2.15.0", {"center": v(-32.1, 27.5) * mm, "radius": 1 * mm});
            skCircle(sketch, "E26.4.15.0", {"center": v(36.9, 27.5) * mm, "radius": 1 * mm});
            skCircle(sketch, "E26.6.15.0", {"center": v(3.9, 27.5) * mm, "radius": 1 * mm});
            skCircle(sketch, "E26.8.15.0", {"center": v(54.9, 27.5) * mm, "radius": 1 * mm});
            skCircle(sketch, "E26.10.15.0", {"center": v(53.4, 26) * mm, "radius": 1 * mm});
            skCircle(sketch, "E26.12.15.0", {"center": v(29.4, 26) * mm, "radius": 1 * mm});
            skCircle(sketch, "E26.14.15.0", {"center": v(2.4, 26) * mm, "radius": 1 * mm});
            skCircle(sketch, "E26.18.15.0", {"center": v(18.9, 27.5) * mm, "radius": 1 * mm});
            skCircle(sketch, "E26.20.15.0", {"center": v(-30.6, 26) * mm, "radius": 1 * mm});
            skCircle(sketch, "E26.24.15.0", {"center": v(-44.1, 27.5) * mm, "radius": 1 * mm});
            skCircle(sketch, "E26.26.15.0", {"center": v(30.9, 27.5) * mm, "radius": 1 * mm});
            skCircle(sketch, "E26.28.15.0", {"center": v(-9.6, 26) * mm, "radius": 1 * mm});
            skCircle(sketch, "E26.32.15.0", {"center": v(-14.1, 27.5) * mm, "radius": 1 * mm});
            skCircle(sketch, "E26.34.15.0", {"center": v(-2.1, 27.5) * mm, "radius": 1 * mm});
            skCircle(sketch, "E26.36.15.0", {"center": v(9.9, 27.5) * mm, "radius": 1 * mm});
            skCircle(sketch, "E26.38.15.0", {"center": v(24.9, 27.5) * mm, "radius": 1 * mm});
            skCircle(sketch, "E26.40.15.0", {"center": v(5.4, 26) * mm, "radius": 1 * mm});
            skCircle(sketch, "E26.42.15.0", {"center": v(-23.1, 27.5) * mm, "radius": 1 * mm});
            skCircle(sketch, "E26.44.15.0", {"center": v(-5.1, 27.5) * mm, "radius": 1 * mm});
            skCircle(sketch, "E26.46.15.0", {"center": v(23.4, 26) * mm, "radius": 1 * mm});
            skCircle(sketch, "E26.48.15.0", {"center": v(42.9, 27.5) * mm, "radius": 1 * mm});
            skCircle(sketch, "E26.50.15.0", {"center": v(0.9, 27.5) * mm, "radius": 1 * mm});
            skCircle(sketch, "E26.52.15.0", {"center": v(-36.6, 26) * mm, "radius": 1 * mm});
            skCircle(sketch, "E26.54.15.0", {"center": v(41.4, 26) * mm, "radius": 1 * mm});
            skCircle(sketch, "E26.56.15.0", {"center": v(-12.6, 26) * mm, "radius": 1 * mm});
            skCircle(sketch, "E26.58.15.0", {"center": v(-26.1, 27.5) * mm, "radius": 1 * mm});
            skCircle(sketch, "E26.60.15.0", {"center": v(-8.1, 27.5) * mm, "radius": 1 * mm});
            skCircle(sketch, "E26.62.15.0", {"center": v(-27.6, 26) * mm, "radius": 1 * mm});
            skCircle(sketch, "E26.64.15.0", {"center": v(-29.1, 27.5) * mm, "radius": 1 * mm});
            skCircle(sketch, "E26.66.15.0", {"center": v(15.9, 27.5) * mm, "radius": 1 * mm});
            skCircle(sketch, "E26.68.15.0", {"center": v(-3.6, 26) * mm, "radius": 1 * mm});
            skCircle(sketch, "E26.70.15.0", {"center": v(-11.1, 27.5) * mm, "radius": 1 * mm});
            skCircle(sketch, "E26.72.15.0", {"center": v(44.4, 26) * mm, "radius": 1 * mm});
            skCircle(sketch, "E26.74.15.0", {"center": v(8.4, 26) * mm, "radius": 1 * mm});
            skCircle(sketch, "E26.76.15.0", {"center": v(33.9, 27.5) * mm, "radius": 1 * mm});
            skCircle(sketch, "E26.78.15.0", {"center": v(12.9, 27.5) * mm, "radius": 1 * mm});
            skCircle(sketch, "E26.80.15.0", {"center": v(-38.1, 27.5) * mm, "radius": 1 * mm});
            skCircle(sketch, "E26.82.15.0", {"center": v(-18.6, 26) * mm, "radius": 1 * mm});
            skCircle(sketch, "E26.84.15.0", {"center": v(-17.1, 27.5) * mm, "radius": 1 * mm});
            skCircle(sketch, "E26.86.15.0", {"center": v(48.9, 27.5) * mm, "radius": 1 * mm});
            skCircle(sketch, "E26.88.15.0", {"center": v(35.4, 26) * mm, "radius": 1 * mm});
            skCircle(sketch, "E26.90.15.0", {"center": v(11.4, 26) * mm, "radius": 1 * mm});
            skCircle(sketch, "E26.92.15.0", {"center": v(-24.6, 26) * mm, "radius": 1 * mm});
            skCircle(sketch, "E26.94.15.0", {"center": v(21.9, 27.5) * mm, "radius": 1 * mm});
            skCircle(sketch, "E26.96.15.0", {"center": v(50.4, 26) * mm, "radius": 1 * mm});
            skCircle(sketch, "E26.98.15.0", {"center": v(26.4, 26) * mm, "radius": 1 * mm});
            skCircle(sketch, "E26.100.15.0", {"center": v(20.4, 26) * mm, "radius": 1 * mm});
            skCircle(sketch, "E26.102.15.0", {"center": v(39.9, 27.5) * mm, "radius": 1 * mm});
            skCircle(sketch, "E26.104.15.0", {"center": v(-0.6, 26) * mm, "radius": 1 * mm});
            skCircle(sketch, "E26.106.15.0", {"center": v(47.4, 26) * mm, "radius": 1 * mm});
            skCircle(sketch, "E26.110.15.0", {"center": v(-39.6, 26) * mm, "radius": 1 * mm});
            skCircle(sketch, "E26.112.15.0", {"center": v(38.4, 26) * mm, "radius": 1 * mm});
            skCircle(sketch, "E26.114.15.0", {"center": v(-35.1, 27.5) * mm, "radius": 1 * mm});
            skCircle(sketch, "E26.116.15.0", {"center": v(17.4, 26) * mm, "radius": 1 * mm});
            skCircle(sketch, "E26.118.15.0", {"center": v(51.9, 27.5) * mm, "radius": 1 * mm});
            skCircle(sketch, "E26.120.15.0", {"center": v(-33.6, 26) * mm, "radius": 1 * mm});
            skCircle(sketch, "E26.124.15.0", {"center": v(-15.6, 26) * mm, "radius": 1 * mm});
            skCircle(sketch, "E26.126.15.0", {"center": v(14.4, 26) * mm, "radius": 1 * mm});
            skCircle(sketch, "E26.128.15.0", {"center": v(45.9, 27.5) * mm, "radius": 1 * mm});
            skCircle(sketch, "E26.130.15.0", {"center": v(-6.6, 26) * mm, "radius": 1 * mm});
            skCircle(sketch, "E26.132.15.0", {"center": v(32.4, 26) * mm, "radius": 1 * mm});
            skCircle(sketch, "E26.134.15.0", {"center": v(-21.6, 26) * mm, "radius": 1 * mm});
            skCircle(sketch, "E26.136.15.0", {"center": v(6.9, 27.5) * mm, "radius": 1 * mm});
            skCircle(sketch, "E26.138.15.0", {"center": v(-20.1, 27.5) * mm, "radius": 1 * mm});
            skCircle(sketch, "E26.140.15.0", {"center": v(-41.1, 27.5) * mm, "radius": 1 * mm});
            skCircle(sketch, "E26.144.15.0", {"center": v(-47.1, 27.5) * mm, "radius": 1 * mm});
            skCircle(sketch, "E26.146.15.0", {"center": v(-42.6, 26) * mm, "radius": 1 * mm});
            skCircle(sketch, "E26.148.15.0", {"center": v(-45.6, 26) * mm, "radius": 1 * mm});
            skCircle(sketch, "E26.150.15.0", {"center": v(-48.6, 26) * mm, "radius": 1 * mm});
            skLineSegment(sketch, "E26.152.15.0", {"start": v(-50.1, 27.5) * mm, "end": v(-50.1, 28.5) * mm, "construction": true});
            skCircle(sketch, "E26.155.15.0", {"center": v(-50.1, 27.5) * mm, "radius": 1 * mm});
            skLineSegment(sketch, "E26.157.15.0", {"start": v(-51.1, 27.5) * mm, "end": v(-50.1, 27.5) * mm, "construction": true});
            skLineSegment(sketch, "E26.160.15.0", {"start": v(-51.1, 26) * mm, "end": v(-48.6, 26) * mm, "construction": true});
            skLineSegment(sketch, "E26.163.15.0", {"start": v(-48.6, 26) * mm, "end": v(-48.6, 28.5) * mm, "construction": true});
            skCircle(sketch, "E26.0.16.0", {"center": v(27.9, 24.5) * mm, "radius": 1 * mm});
            skCircle(sketch, "E26.2.16.0", {"center": v(-32.1, 24.5) * mm, "radius": 1 * mm});
            skCircle(sketch, "E26.4.16.0", {"center": v(36.9, 24.5) * mm, "radius": 1 * mm});
            skCircle(sketch, "E26.6.16.0", {"center": v(3.9, 24.5) * mm, "radius": 1 * mm});
            skCircle(sketch, "E26.8.16.0", {"center": v(54.9, 24.5) * mm, "radius": 1 * mm});
            skCircle(sketch, "E26.10.16.0", {"center": v(53.4, 23) * mm, "radius": 1 * mm});
            skCircle(sketch, "E26.12.16.0", {"center": v(29.4, 23) * mm, "radius": 1 * mm});
            skCircle(sketch, "E26.14.16.0", {"center": v(2.4, 23) * mm, "radius": 1 * mm});
            skCircle(sketch, "E26.18.16.0", {"center": v(18.9, 24.5) * mm, "radius": 1 * mm});
            skCircle(sketch, "E26.20.16.0", {"center": v(-30.6, 23) * mm, "radius": 1 * mm});
            skCircle(sketch, "E26.24.16.0", {"center": v(-44.1, 24.5) * mm, "radius": 1 * mm});
            skCircle(sketch, "E26.26.16.0", {"center": v(30.9, 24.5) * mm, "radius": 1 * mm});
            skCircle(sketch, "E26.28.16.0", {"center": v(-9.6, 23) * mm, "radius": 1 * mm});
            skCircle(sketch, "E26.32.16.0", {"center": v(-14.1, 24.5) * mm, "radius": 1 * mm});
            skCircle(sketch, "E26.34.16.0", {"center": v(-2.1, 24.5) * mm, "radius": 1 * mm});
            skCircle(sketch, "E26.36.16.0", {"center": v(9.9, 24.5) * mm, "radius": 1 * mm});
            skCircle(sketch, "E26.38.16.0", {"center": v(24.9, 24.5) * mm, "radius": 1 * mm});
            skCircle(sketch, "E26.40.16.0", {"center": v(5.4, 23) * mm, "radius": 1 * mm});
            skCircle(sketch, "E26.42.16.0", {"center": v(-23.1, 24.5) * mm, "radius": 1 * mm});
            skCircle(sketch, "E26.44.16.0", {"center": v(-5.1, 24.5) * mm, "radius": 1 * mm});
            skCircle(sketch, "E26.46.16.0", {"center": v(23.4, 23) * mm, "radius": 1 * mm});
            skCircle(sketch, "E26.48.16.0", {"center": v(42.9, 24.5) * mm, "radius": 1 * mm});
            skCircle(sketch, "E26.50.16.0", {"center": v(0.9, 24.5) * mm, "radius": 1 * mm});
            skCircle(sketch, "E26.52.16.0", {"center": v(-36.6, 23) * mm, "radius": 1 * mm});
            skCircle(sketch, "E26.54.16.0", {"center": v(41.4, 23) * mm, "radius": 1 * mm});
            skCircle(sketch, "E26.56.16.0", {"center": v(-12.6, 23) * mm, "radius": 1 * mm});
            skCircle(sketch, "E26.58.16.0", {"center": v(-26.1, 24.5) * mm, "radius": 1 * mm});
            skCircle(sketch, "E26.60.16.0", {"center": v(-8.1, 24.5) * mm, "radius": 1 * mm});
            skCircle(sketch, "E26.62.16.0", {"center": v(-27.6, 23) * mm, "radius": 1 * mm});
            skCircle(sketch, "E26.64.16.0", {"center": v(-29.1, 24.5) * mm, "radius": 1 * mm});
            skCircle(sketch, "E26.66.16.0", {"center": v(15.9, 24.5) * mm, "radius": 1 * mm});
            skCircle(sketch, "E26.68.16.0", {"center": v(-3.6, 23) * mm, "radius": 1 * mm});
            skCircle(sketch, "E26.70.16.0", {"center": v(-11.1, 24.5) * mm, "radius": 1 * mm});
            skCircle(sketch, "E26.72.16.0", {"center": v(44.4, 23) * mm, "radius": 1 * mm});
            skCircle(sketch, "E26.74.16.0", {"center": v(8.4, 23) * mm, "radius": 1 * mm});
            skCircle(sketch, "E26.76.16.0", {"center": v(33.9, 24.5) * mm, "radius": 1 * mm});
            skCircle(sketch, "E26.78.16.0", {"center": v(12.9, 24.5) * mm, "radius": 1 * mm});
            skCircle(sketch, "E26.80.16.0", {"center": v(-38.1, 24.5) * mm, "radius": 1 * mm});
            skCircle(sketch, "E26.82.16.0", {"center": v(-18.6, 23) * mm, "radius": 1 * mm});
            skCircle(sketch, "E26.84.16.0", {"center": v(-17.1, 24.5) * mm, "radius": 1 * mm});
            skCircle(sketch, "E26.86.16.0", {"center": v(48.9, 24.5) * mm, "radius": 1 * mm});
            skCircle(sketch, "E26.88.16.0", {"center": v(35.4, 23) * mm, "radius": 1 * mm});
            skCircle(sketch, "E26.90.16.0", {"center": v(11.4, 23) * mm, "radius": 1 * mm});
            skCircle(sketch, "E26.92.16.0", {"center": v(-24.6, 23) * mm, "radius": 1 * mm});
            skCircle(sketch, "E26.94.16.0", {"center": v(21.9, 24.5) * mm, "radius": 1 * mm});
            skCircle(sketch, "E26.96.16.0", {"center": v(50.4, 23) * mm, "radius": 1 * mm});
            skCircle(sketch, "E26.98.16.0", {"center": v(26.4, 23) * mm, "radius": 1 * mm});
            skCircle(sketch, "E26.100.16.0", {"center": v(20.4, 23) * mm, "radius": 1 * mm});
            skCircle(sketch, "E26.102.16.0", {"center": v(39.9, 24.5) * mm, "radius": 1 * mm});
            skCircle(sketch, "E26.104.16.0", {"center": v(-0.6, 23) * mm, "radius": 1 * mm});
            skCircle(sketch, "E26.106.16.0", {"center": v(47.4, 23) * mm, "radius": 1 * mm});
            skCircle(sketch, "E26.110.16.0", {"center": v(-39.6, 23) * mm, "radius": 1 * mm});
            skCircle(sketch, "E26.112.16.0", {"center": v(38.4, 23) * mm, "radius": 1 * mm});
            skCircle(sketch, "E26.114.16.0", {"center": v(-35.1, 24.5) * mm, "radius": 1 * mm});
            skCircle(sketch, "E26.116.16.0", {"center": v(17.4, 23) * mm, "radius": 1 * mm});
            skCircle(sketch, "E26.118.16.0", {"center": v(51.9, 24.5) * mm, "radius": 1 * mm});
            skCircle(sketch, "E26.120.16.0", {"center": v(-33.6, 23) * mm, "radius": 1 * mm});
            skCircle(sketch, "E26.124.16.0", {"center": v(-15.6, 23) * mm, "radius": 1 * mm});
            skCircle(sketch, "E26.126.16.0", {"center": v(14.4, 23) * mm, "radius": 1 * mm});
            skCircle(sketch, "E26.128.16.0", {"center": v(45.9, 24.5) * mm, "radius": 1 * mm});
            skCircle(sketch, "E26.130.16.0", {"center": v(-6.6, 23) * mm, "radius": 1 * mm});
            skCircle(sketch, "E26.132.16.0", {"center": v(32.4, 23) * mm, "radius": 1 * mm});
            skCircle(sketch, "E26.134.16.0", {"center": v(-21.6, 23) * mm, "radius": 1 * mm});
            skCircle(sketch, "E26.136.16.0", {"center": v(6.9, 24.5) * mm, "radius": 1 * mm});
            skCircle(sketch, "E26.138.16.0", {"center": v(-20.1, 24.5) * mm, "radius": 1 * mm});
            skCircle(sketch, "E26.140.16.0", {"center": v(-41.1, 24.5) * mm, "radius": 1 * mm});
            skCircle(sketch, "E26.144.16.0", {"center": v(-47.1, 24.5) * mm, "radius": 1 * mm});
            skCircle(sketch, "E26.146.16.0", {"center": v(-42.6, 23) * mm, "radius": 1 * mm});
            skCircle(sketch, "E26.148.16.0", {"center": v(-45.6, 23) * mm, "radius": 1 * mm});
            skCircle(sketch, "E26.150.16.0", {"center": v(-48.6, 23) * mm, "radius": 1 * mm});
            skLineSegment(sketch, "E26.152.16.0", {"start": v(-50.1, 24.5) * mm, "end": v(-50.1, 25.5) * mm, "construction": true});
            skCircle(sketch, "E26.155.16.0", {"center": v(-50.1, 24.5) * mm, "radius": 1 * mm});
            skLineSegment(sketch, "E26.157.16.0", {"start": v(-51.1, 24.5) * mm, "end": v(-50.1, 24.5) * mm, "construction": true});
            skLineSegment(sketch, "E26.160.16.0", {"start": v(-51.1, 23) * mm, "end": v(-48.6, 23) * mm, "construction": true});
            skLineSegment(sketch, "E26.163.16.0", {"start": v(-48.6, 23) * mm, "end": v(-48.6, 25.5) * mm, "construction": true});
            skCircle(sketch, "E26.0.17.0", {"center": v(27.9, 21.5) * mm, "radius": 1 * mm});
            skCircle(sketch, "E26.2.17.0", {"center": v(-32.1, 21.5) * mm, "radius": 1 * mm});
            skCircle(sketch, "E26.4.17.0", {"center": v(36.9, 21.5) * mm, "radius": 1 * mm});
            skCircle(sketch, "E26.6.17.0", {"center": v(3.9, 21.5) * mm, "radius": 1 * mm});
            skCircle(sketch, "E26.8.17.0", {"center": v(54.9, 21.5) * mm, "radius": 1 * mm});
            skCircle(sketch, "E26.10.17.0", {"center": v(53.4, 20) * mm, "radius": 1 * mm});
            skCircle(sketch, "E26.12.17.0", {"center": v(29.4, 20) * mm, "radius": 1 * mm});
            skCircle(sketch, "E26.14.17.0", {"center": v(2.4, 20) * mm, "radius": 1 * mm});
            skCircle(sketch, "E26.18.17.0", {"center": v(18.9, 21.5) * mm, "radius": 1 * mm});
            skCircle(sketch, "E26.20.17.0", {"center": v(-30.6, 20) * mm, "radius": 1 * mm});
            skCircle(sketch, "E26.24.17.0", {"center": v(-44.1, 21.5) * mm, "radius": 1 * mm});
            skCircle(sketch, "E26.26.17.0", {"center": v(30.9, 21.5) * mm, "radius": 1 * mm});
            skCircle(sketch, "E26.28.17.0", {"center": v(-9.6, 20) * mm, "radius": 1 * mm});
            skCircle(sketch, "E26.32.17.0", {"center": v(-14.1, 21.5) * mm, "radius": 1 * mm});
            skCircle(sketch, "E26.34.17.0", {"center": v(-2.1, 21.5) * mm, "radius": 1 * mm});
            skCircle(sketch, "E26.36.17.0", {"center": v(9.9, 21.5) * mm, "radius": 1 * mm});
            skCircle(sketch, "E26.38.17.0", {"center": v(24.9, 21.5) * mm, "radius": 1 * mm});
            skCircle(sketch, "E26.40.17.0", {"center": v(5.4, 20) * mm, "radius": 1 * mm});
            skCircle(sketch, "E26.42.17.0", {"center": v(-23.1, 21.5) * mm, "radius": 1 * mm});
            skCircle(sketch, "E26.44.17.0", {"center": v(-5.1, 21.5) * mm, "radius": 1 * mm});
            skCircle(sketch, "E26.46.17.0", {"center": v(23.4, 20) * mm, "radius": 1 * mm});
            skCircle(sketch, "E26.48.17.0", {"center": v(42.9, 21.5) * mm, "radius": 1 * mm});
            skCircle(sketch, "E26.50.17.0", {"center": v(0.9, 21.5) * mm, "radius": 1 * mm});
            skCircle(sketch, "E26.52.17.0", {"center": v(-36.6, 20) * mm, "radius": 1 * mm});
            skCircle(sketch, "E26.54.17.0", {"center": v(41.4, 20) * mm, "radius": 1 * mm});
            skCircle(sketch, "E26.56.17.0", {"center": v(-12.6, 20) * mm, "radius": 1 * mm});
            skCircle(sketch, "E26.58.17.0", {"center": v(-26.1, 21.5) * mm, "radius": 1 * mm});
            skCircle(sketch, "E26.60.17.0", {"center": v(-8.1, 21.5) * mm, "radius": 1 * mm});
            skCircle(sketch, "E26.62.17.0", {"center": v(-27.6, 20) * mm, "radius": 1 * mm});
            skCircle(sketch, "E26.64.17.0", {"center": v(-29.1, 21.5) * mm, "radius": 1 * mm});
            skCircle(sketch, "E26.66.17.0", {"center": v(15.9, 21.5) * mm, "radius": 1 * mm});
            skCircle(sketch, "E26.68.17.0", {"center": v(-3.6, 20) * mm, "radius": 1 * mm});
            skCircle(sketch, "E26.70.17.0", {"center": v(-11.1, 21.5) * mm, "radius": 1 * mm});
            skCircle(sketch, "E26.72.17.0", {"center": v(44.4, 20) * mm, "radius": 1 * mm});
            skCircle(sketch, "E26.74.17.0", {"center": v(8.4, 20) * mm, "radius": 1 * mm});
            skCircle(sketch, "E26.76.17.0", {"center": v(33.9, 21.5) * mm, "radius": 1 * mm});
            skCircle(sketch, "E26.78.17.0", {"center": v(12.9, 21.5) * mm, "radius": 1 * mm});
            skCircle(sketch, "E26.80.17.0", {"center": v(-38.1, 21.5) * mm, "radius": 1 * mm});
            skCircle(sketch, "E26.82.17.0", {"center": v(-18.6, 20) * mm, "radius": 1 * mm});
            skCircle(sketch, "E26.84.17.0", {"center": v(-17.1, 21.5) * mm, "radius": 1 * mm});
            skCircle(sketch, "E26.86.17.0", {"center": v(48.9, 21.5) * mm, "radius": 1 * mm});
            skCircle(sketch, "E26.88.17.0", {"center": v(35.4, 20) * mm, "radius": 1 * mm});
            skCircle(sketch, "E26.90.17.0", {"center": v(11.4, 20) * mm, "radius": 1 * mm});
            skCircle(sketch, "E26.92.17.0", {"center": v(-24.6, 20) * mm, "radius": 1 * mm});
            skCircle(sketch, "E26.94.17.0", {"center": v(21.9, 21.5) * mm, "radius": 1 * mm});
            skCircle(sketch, "E26.96.17.0", {"center": v(50.4, 20) * mm, "radius": 1 * mm});
            skCircle(sketch, "E26.98.17.0", {"center": v(26.4, 20) * mm, "radius": 1 * mm});
            skCircle(sketch, "E26.100.17.0", {"center": v(20.4, 20) * mm, "radius": 1 * mm});
            skCircle(sketch, "E26.102.17.0", {"center": v(39.9, 21.5) * mm, "radius": 1 * mm});
            skCircle(sketch, "E26.104.17.0", {"center": v(-0.6, 20) * mm, "radius": 1 * mm});
            skCircle(sketch, "E26.106.17.0", {"center": v(47.4, 20) * mm, "radius": 1 * mm});
            skCircle(sketch, "E26.110.17.0", {"center": v(-39.6, 20) * mm, "radius": 1 * mm});
            skCircle(sketch, "E26.112.17.0", {"center": v(38.4, 20) * mm, "radius": 1 * mm});
            skCircle(sketch, "E26.114.17.0", {"center": v(-35.1, 21.5) * mm, "radius": 1 * mm});
            skCircle(sketch, "E26.116.17.0", {"center": v(17.4, 20) * mm, "radius": 1 * mm});
            skCircle(sketch, "E26.118.17.0", {"center": v(51.9, 21.5) * mm, "radius": 1 * mm});
            skCircle(sketch, "E26.120.17.0", {"center": v(-33.6, 20) * mm, "radius": 1 * mm});
            skCircle(sketch, "E26.124.17.0", {"center": v(-15.6, 20) * mm, "radius": 1 * mm});
            skCircle(sketch, "E26.126.17.0", {"center": v(14.4, 20) * mm, "radius": 1 * mm});
            skCircle(sketch, "E26.128.17.0", {"center": v(45.9, 21.5) * mm, "radius": 1 * mm});
            skCircle(sketch, "E26.130.17.0", {"center": v(-6.6, 20) * mm, "radius": 1 * mm});
            skCircle(sketch, "E26.132.17.0", {"center": v(32.4, 20) * mm, "radius": 1 * mm});
            skCircle(sketch, "E26.134.17.0", {"center": v(-21.6, 20) * mm, "radius": 1 * mm});
            skCircle(sketch, "E26.136.17.0", {"center": v(6.9, 21.5) * mm, "radius": 1 * mm});
            skCircle(sketch, "E26.138.17.0", {"center": v(-20.1, 21.5) * mm, "radius": 1 * mm});
            skCircle(sketch, "E26.140.17.0", {"center": v(-41.1, 21.5) * mm, "radius": 1 * mm});
            skCircle(sketch, "E26.144.17.0", {"center": v(-47.1, 21.5) * mm, "radius": 1 * mm});
            skCircle(sketch, "E26.146.17.0", {"center": v(-42.6, 20) * mm, "radius": 1 * mm});
            skCircle(sketch, "E26.148.17.0", {"center": v(-45.6, 20) * mm, "radius": 1 * mm});
            skCircle(sketch, "E26.150.17.0", {"center": v(-48.6, 20) * mm, "radius": 1 * mm});
            skLineSegment(sketch, "E26.152.17.0", {"start": v(-50.1, 21.5) * mm, "end": v(-50.1, 22.5) * mm, "construction": true});
            skCircle(sketch, "E26.155.17.0", {"center": v(-50.1, 21.5) * mm, "radius": 1 * mm});
            skLineSegment(sketch, "E26.157.17.0", {"start": v(-51.1, 21.5) * mm, "end": v(-50.1, 21.5) * mm, "construction": true});
            skLineSegment(sketch, "E26.160.17.0", {"start": v(-51.1, 20) * mm, "end": v(-48.6, 20) * mm, "construction": true});
            skLineSegment(sketch, "E26.163.17.0", {"start": v(-48.6, 20) * mm, "end": v(-48.6, 22.5) * mm, "construction": true});
            skCircle(sketch, "E26.0.18.0", {"center": v(27.9, 18.5) * mm, "radius": 1 * mm});
            skCircle(sketch, "E26.2.18.0", {"center": v(-32.1, 18.5) * mm, "radius": 1 * mm});
            skCircle(sketch, "E26.4.18.0", {"center": v(36.9, 18.5) * mm, "radius": 1 * mm});
            skCircle(sketch, "E26.6.18.0", {"center": v(3.9, 18.5) * mm, "radius": 1 * mm});
            skCircle(sketch, "E26.8.18.0", {"center": v(54.9, 18.5) * mm, "radius": 1 * mm});
            skCircle(sketch, "E26.10.18.0", {"center": v(53.4, 17) * mm, "radius": 1 * mm});
            skCircle(sketch, "E26.12.18.0", {"center": v(29.4, 17) * mm, "radius": 1 * mm});
            skCircle(sketch, "E26.14.18.0", {"center": v(2.4, 17) * mm, "radius": 1 * mm});
            skCircle(sketch, "E26.18.18.0", {"center": v(18.9, 18.5) * mm, "radius": 1 * mm});
            skCircle(sketch, "E26.20.18.0", {"center": v(-30.6, 17) * mm, "radius": 1 * mm});
            skCircle(sketch, "E26.24.18.0", {"center": v(-44.1, 18.5) * mm, "radius": 1 * mm});
            skCircle(sketch, "E26.26.18.0", {"center": v(30.9, 18.5) * mm, "radius": 1 * mm});
            skCircle(sketch, "E26.28.18.0", {"center": v(-9.6, 17) * mm, "radius": 1 * mm});
            skCircle(sketch, "E26.32.18.0", {"center": v(-14.1, 18.5) * mm, "radius": 1 * mm});
            skCircle(sketch, "E26.34.18.0", {"center": v(-2.1, 18.5) * mm, "radius": 1 * mm});
            skCircle(sketch, "E26.36.18.0", {"center": v(9.9, 18.5) * mm, "radius": 1 * mm});
            skCircle(sketch, "E26.38.18.0", {"center": v(24.9, 18.5) * mm, "radius": 1 * mm});
            skCircle(sketch, "E26.40.18.0", {"center": v(5.4, 17) * mm, "radius": 1 * mm});
            skCircle(sketch, "E26.42.18.0", {"center": v(-23.1, 18.5) * mm, "radius": 1 * mm});
            skCircle(sketch, "E26.44.18.0", {"center": v(-5.1, 18.5) * mm, "radius": 1 * mm});
            skCircle(sketch, "E26.46.18.0", {"center": v(23.4, 17) * mm, "radius": 1 * mm});
            skCircle(sketch, "E26.48.18.0", {"center": v(42.9, 18.5) * mm, "radius": 1 * mm});
            skCircle(sketch, "E26.50.18.0", {"center": v(0.9, 18.5) * mm, "radius": 1 * mm});
            skCircle(sketch, "E26.52.18.0", {"center": v(-36.6, 17) * mm, "radius": 1 * mm});
            skCircle(sketch, "E26.54.18.0", {"center": v(41.4, 17) * mm, "radius": 1 * mm});
            skCircle(sketch, "E26.56.18.0", {"center": v(-12.6, 17) * mm, "radius": 1 * mm});
            skCircle(sketch, "E26.58.18.0", {"center": v(-26.1, 18.5) * mm, "radius": 1 * mm});
            skCircle(sketch, "E26.60.18.0", {"center": v(-8.1, 18.5) * mm, "radius": 1 * mm});
            skCircle(sketch, "E26.62.18.0", {"center": v(-27.6, 17) * mm, "radius": 1 * mm});
            skCircle(sketch, "E26.64.18.0", {"center": v(-29.1, 18.5) * mm, "radius": 1 * mm});
            skCircle(sketch, "E26.66.18.0", {"center": v(15.9, 18.5) * mm, "radius": 1 * mm});
            skCircle(sketch, "E26.68.18.0", {"center": v(-3.6, 17) * mm, "radius": 1 * mm});
            skCircle(sketch, "E26.70.18.0", {"center": v(-11.1, 18.5) * mm, "radius": 1 * mm});
            skCircle(sketch, "E26.72.18.0", {"center": v(44.4, 17) * mm, "radius": 1 * mm});
            skCircle(sketch, "E26.74.18.0", {"center": v(8.4, 17) * mm, "radius": 1 * mm});
            skCircle(sketch, "E26.76.18.0", {"center": v(33.9, 18.5) * mm, "radius": 1 * mm});
            skCircle(sketch, "E26.78.18.0", {"center": v(12.9, 18.5) * mm, "radius": 1 * mm});
            skCircle(sketch, "E26.80.18.0", {"center": v(-38.1, 18.5) * mm, "radius": 1 * mm});
            skCircle(sketch, "E26.82.18.0", {"center": v(-18.6, 17) * mm, "radius": 1 * mm});
            skCircle(sketch, "E26.84.18.0", {"center": v(-17.1, 18.5) * mm, "radius": 1 * mm});
            skCircle(sketch, "E26.86.18.0", {"center": v(48.9, 18.5) * mm, "radius": 1 * mm});
            skCircle(sketch, "E26.88.18.0", {"center": v(35.4, 17) * mm, "radius": 1 * mm});
            skCircle(sketch, "E26.90.18.0", {"center": v(11.4, 17) * mm, "radius": 1 * mm});
            skCircle(sketch, "E26.92.18.0", {"center": v(-24.6, 17) * mm, "radius": 1 * mm});
            skCircle(sketch, "E26.94.18.0", {"center": v(21.9, 18.5) * mm, "radius": 1 * mm});
            skCircle(sketch, "E26.96.18.0", {"center": v(50.4, 17) * mm, "radius": 1 * mm});
            skCircle(sketch, "E26.98.18.0", {"center": v(26.4, 17) * mm, "radius": 1 * mm});
            skCircle(sketch, "E26.100.18.0", {"center": v(20.4, 17) * mm, "radius": 1 * mm});
            skCircle(sketch, "E26.102.18.0", {"center": v(39.9, 18.5) * mm, "radius": 1 * mm});
            skCircle(sketch, "E26.104.18.0", {"center": v(-0.6, 17) * mm, "radius": 1 * mm});
            skCircle(sketch, "E26.106.18.0", {"center": v(47.4, 17) * mm, "radius": 1 * mm});
            skCircle(sketch, "E26.110.18.0", {"center": v(-39.6, 17) * mm, "radius": 1 * mm});
            skCircle(sketch, "E26.112.18.0", {"center": v(38.4, 17) * mm, "radius": 1 * mm});
            skCircle(sketch, "E26.114.18.0", {"center": v(-35.1, 18.5) * mm, "radius": 1 * mm});
            skCircle(sketch, "E26.116.18.0", {"center": v(17.4, 17) * mm, "radius": 1 * mm});
            skCircle(sketch, "E26.118.18.0", {"center": v(51.9, 18.5) * mm, "radius": 1 * mm});
            skCircle(sketch, "E26.120.18.0", {"center": v(-33.6, 17) * mm, "radius": 1 * mm});
            skCircle(sketch, "E26.124.18.0", {"center": v(-15.6, 17) * mm, "radius": 1 * mm});
            skCircle(sketch, "E26.126.18.0", {"center": v(14.4, 17) * mm, "radius": 1 * mm});
            skCircle(sketch, "E26.128.18.0", {"center": v(45.9, 18.5) * mm, "radius": 1 * mm});
            skCircle(sketch, "E26.130.18.0", {"center": v(-6.6, 17) * mm, "radius": 1 * mm});
            skCircle(sketch, "E26.132.18.0", {"center": v(32.4, 17) * mm, "radius": 1 * mm});
            skCircle(sketch, "E26.134.18.0", {"center": v(-21.6, 17) * mm, "radius": 1 * mm});
            skCircle(sketch, "E26.136.18.0", {"center": v(6.9, 18.5) * mm, "radius": 1 * mm});
            skCircle(sketch, "E26.138.18.0", {"center": v(-20.1, 18.5) * mm, "radius": 1 * mm});
            skCircle(sketch, "E26.140.18.0", {"center": v(-41.1, 18.5) * mm, "radius": 1 * mm});
            skCircle(sketch, "E26.144.18.0", {"center": v(-47.1, 18.5) * mm, "radius": 1 * mm});
            skCircle(sketch, "E26.146.18.0", {"center": v(-42.6, 17) * mm, "radius": 1 * mm});
            skCircle(sketch, "E26.148.18.0", {"center": v(-45.6, 17) * mm, "radius": 1 * mm});
            skCircle(sketch, "E26.150.18.0", {"center": v(-48.6, 17) * mm, "radius": 1 * mm});
            skLineSegment(sketch, "E26.152.18.0", {"start": v(-50.1, 18.5) * mm, "end": v(-50.1, 19.5) * mm, "construction": true});
            skCircle(sketch, "E26.155.18.0", {"center": v(-50.1, 18.5) * mm, "radius": 1 * mm});
            skLineSegment(sketch, "E26.157.18.0", {"start": v(-51.1, 18.5) * mm, "end": v(-50.1, 18.5) * mm, "construction": true});
            skLineSegment(sketch, "E26.160.18.0", {"start": v(-51.1, 17) * mm, "end": v(-48.6, 17) * mm, "construction": true});
            skLineSegment(sketch, "E26.163.18.0", {"start": v(-48.6, 17) * mm, "end": v(-48.6, 19.5) * mm, "construction": true});
            skCircle(sketch, "E26.0.19.0", {"center": v(27.9, 15.5) * mm, "radius": 1 * mm});
            skCircle(sketch, "E26.2.19.0", {"center": v(-32.1, 15.5) * mm, "radius": 1 * mm});
            skCircle(sketch, "E26.4.19.0", {"center": v(36.9, 15.5) * mm, "radius": 1 * mm});
            skCircle(sketch, "E26.6.19.0", {"center": v(3.9, 15.5) * mm, "radius": 1 * mm});
            skCircle(sketch, "E26.8.19.0", {"center": v(54.9, 15.5) * mm, "radius": 1 * mm});
            skCircle(sketch, "E26.10.19.0", {"center": v(53.4, 14) * mm, "radius": 1 * mm});
            skCircle(sketch, "E26.12.19.0", {"center": v(29.4, 14) * mm, "radius": 1 * mm});
            skCircle(sketch, "E26.14.19.0", {"center": v(2.4, 14) * mm, "radius": 1 * mm});
            skCircle(sketch, "E26.18.19.0", {"center": v(18.9, 15.5) * mm, "radius": 1 * mm});
            skCircle(sketch, "E26.20.19.0", {"center": v(-30.6, 14) * mm, "radius": 1 * mm});
            skCircle(sketch, "E26.24.19.0", {"center": v(-44.1, 15.5) * mm, "radius": 1 * mm});
            skCircle(sketch, "E26.26.19.0", {"center": v(30.9, 15.5) * mm, "radius": 1 * mm});
            skCircle(sketch, "E26.28.19.0", {"center": v(-9.6, 14) * mm, "radius": 1 * mm});
            skCircle(sketch, "E26.32.19.0", {"center": v(-14.1, 15.5) * mm, "radius": 1 * mm});
            skCircle(sketch, "E26.34.19.0", {"center": v(-2.1, 15.5) * mm, "radius": 1 * mm});
            skCircle(sketch, "E26.36.19.0", {"center": v(9.9, 15.5) * mm, "radius": 1 * mm});
            skCircle(sketch, "E26.38.19.0", {"center": v(24.9, 15.5) * mm, "radius": 1 * mm});
            skCircle(sketch, "E26.40.19.0", {"center": v(5.4, 14) * mm, "radius": 1 * mm});
            skCircle(sketch, "E26.42.19.0", {"center": v(-23.1, 15.5) * mm, "radius": 1 * mm});
            skCircle(sketch, "E26.44.19.0", {"center": v(-5.1, 15.5) * mm, "radius": 1 * mm});
            skCircle(sketch, "E26.46.19.0", {"center": v(23.4, 14) * mm, "radius": 1 * mm});
            skCircle(sketch, "E26.48.19.0", {"center": v(42.9, 15.5) * mm, "radius": 1 * mm});
            skCircle(sketch, "E26.50.19.0", {"center": v(0.9, 15.5) * mm, "radius": 1 * mm});
            skCircle(sketch, "E26.52.19.0", {"center": v(-36.6, 14) * mm, "radius": 1 * mm});
            skCircle(sketch, "E26.54.19.0", {"center": v(41.4, 14) * mm, "radius": 1 * mm});
            skCircle(sketch, "E26.56.19.0", {"center": v(-12.6, 14) * mm, "radius": 1 * mm});
            skCircle(sketch, "E26.58.19.0", {"center": v(-26.1, 15.5) * mm, "radius": 1 * mm});
            skCircle(sketch, "E26.60.19.0", {"center": v(-8.1, 15.5) * mm, "radius": 1 * mm});
            skCircle(sketch, "E26.62.19.0", {"center": v(-27.6, 14) * mm, "radius": 1 * mm});
            skCircle(sketch, "E26.64.19.0", {"center": v(-29.1, 15.5) * mm, "radius": 1 * mm});
            skCircle(sketch, "E26.66.19.0", {"center": v(15.9, 15.5) * mm, "radius": 1 * mm});
            skCircle(sketch, "E26.68.19.0", {"center": v(-3.6, 14) * mm, "radius": 1 * mm});
            skCircle(sketch, "E26.70.19.0", {"center": v(-11.1, 15.5) * mm, "radius": 1 * mm});
            skCircle(sketch, "E26.72.19.0", {"center": v(44.4, 14) * mm, "radius": 1 * mm});
            skCircle(sketch, "E26.74.19.0", {"center": v(8.4, 14) * mm, "radius": 1 * mm});
            skCircle(sketch, "E26.76.19.0", {"center": v(33.9, 15.5) * mm, "radius": 1 * mm});
            skCircle(sketch, "E26.78.19.0", {"center": v(12.9, 15.5) * mm, "radius": 1 * mm});
            skCircle(sketch, "E26.80.19.0", {"center": v(-38.1, 15.5) * mm, "radius": 1 * mm});
            skCircle(sketch, "E26.82.19.0", {"center": v(-18.6, 14) * mm, "radius": 1 * mm});
            skCircle(sketch, "E26.84.19.0", {"center": v(-17.1, 15.5) * mm, "radius": 1 * mm});
            skCircle(sketch, "E26.86.19.0", {"center": v(48.9, 15.5) * mm, "radius": 1 * mm});
            skCircle(sketch, "E26.88.19.0", {"center": v(35.4, 14) * mm, "radius": 1 * mm});
            skCircle(sketch, "E26.90.19.0", {"center": v(11.4, 14) * mm, "radius": 1 * mm});
            skCircle(sketch, "E26.92.19.0", {"center": v(-24.6, 14) * mm, "radius": 1 * mm});
            skCircle(sketch, "E26.94.19.0", {"center": v(21.9, 15.5) * mm, "radius": 1 * mm});
            skCircle(sketch, "E26.96.19.0", {"center": v(50.4, 14) * mm, "radius": 1 * mm});
            skCircle(sketch, "E26.98.19.0", {"center": v(26.4, 14) * mm, "radius": 1 * mm});
            skCircle(sketch, "E26.100.19.0", {"center": v(20.4, 14) * mm, "radius": 1 * mm});
            skCircle(sketch, "E26.102.19.0", {"center": v(39.9, 15.5) * mm, "radius": 1 * mm});
            skCircle(sketch, "E26.104.19.0", {"center": v(-0.6, 14) * mm, "radius": 1 * mm});
            skCircle(sketch, "E26.106.19.0", {"center": v(47.4, 14) * mm, "radius": 1 * mm});
            skCircle(sketch, "E26.110.19.0", {"center": v(-39.6, 14) * mm, "radius": 1 * mm});
            skCircle(sketch, "E26.112.19.0", {"center": v(38.4, 14) * mm, "radius": 1 * mm});
            skCircle(sketch, "E26.114.19.0", {"center": v(-35.1, 15.5) * mm, "radius": 1 * mm});
            skCircle(sketch, "E26.116.19.0", {"center": v(17.4, 14) * mm, "radius": 1 * mm});
            skCircle(sketch, "E26.118.19.0", {"center": v(51.9, 15.5) * mm, "radius": 1 * mm});
            skCircle(sketch, "E26.120.19.0", {"center": v(-33.6, 14) * mm, "radius": 1 * mm});
            skCircle(sketch, "E26.124.19.0", {"center": v(-15.6, 14) * mm, "radius": 1 * mm});
            skCircle(sketch, "E26.126.19.0", {"center": v(14.4, 14) * mm, "radius": 1 * mm});
            skCircle(sketch, "E26.128.19.0", {"center": v(45.9, 15.5) * mm, "radius": 1 * mm});
            skCircle(sketch, "E26.130.19.0", {"center": v(-6.6, 14) * mm, "radius": 1 * mm});
            skCircle(sketch, "E26.132.19.0", {"center": v(32.4, 14) * mm, "radius": 1 * mm});
            skCircle(sketch, "E26.134.19.0", {"center": v(-21.6, 14) * mm, "radius": 1 * mm});
            skCircle(sketch, "E26.136.19.0", {"center": v(6.9, 15.5) * mm, "radius": 1 * mm});
            skCircle(sketch, "E26.138.19.0", {"center": v(-20.1, 15.5) * mm, "radius": 1 * mm});
            skCircle(sketch, "E26.140.19.0", {"center": v(-41.1, 15.5) * mm, "radius": 1 * mm});
            skCircle(sketch, "E26.144.19.0", {"center": v(-47.1, 15.5) * mm, "radius": 1 * mm});
            skCircle(sketch, "E26.146.19.0", {"center": v(-42.6, 14) * mm, "radius": 1 * mm});
            skCircle(sketch, "E26.148.19.0", {"center": v(-45.6, 14) * mm, "radius": 1 * mm});
            skCircle(sketch, "E26.150.19.0", {"center": v(-48.6, 14) * mm, "radius": 1 * mm});
            skLineSegment(sketch, "E26.152.19.0", {"start": v(-50.1, 15.5) * mm, "end": v(-50.1, 16.5) * mm, "construction": true});
            skCircle(sketch, "E26.155.19.0", {"center": v(-50.1, 15.5) * mm, "radius": 1 * mm});
            skLineSegment(sketch, "E26.157.19.0", {"start": v(-51.1, 15.5) * mm, "end": v(-50.1, 15.5) * mm, "construction": true});
            skLineSegment(sketch, "E26.160.19.0", {"start": v(-51.1, 14) * mm, "end": v(-48.6, 14) * mm, "construction": true});
            skLineSegment(sketch, "E26.163.19.0", {"start": v(-48.6, 14) * mm, "end": v(-48.6, 16.5) * mm, "construction": true});
            skCircle(sketch, "E27.0.20.0", {"center": v(27.9, 12.5) * mm, "radius": 1 * mm});
            skCircle(sketch, "E27.2.20.0", {"center": v(-32.1, 12.5) * mm, "radius": 1 * mm});
            skCircle(sketch, "E27.4.20.0", {"center": v(36.9, 12.5) * mm, "radius": 1 * mm});
            skCircle(sketch, "E27.6.20.0", {"center": v(3.9, 12.5) * mm, "radius": 1 * mm});
            skCircle(sketch, "E27.8.20.0", {"center": v(54.9, 12.5) * mm, "radius": 1 * mm});
            skCircle(sketch, "E27.10.20.0", {"center": v(53.4, 11) * mm, "radius": 1 * mm});
            skCircle(sketch, "E27.12.20.0", {"center": v(29.4, 11) * mm, "radius": 1 * mm});
            skCircle(sketch, "E27.14.20.0", {"center": v(2.4, 11) * mm, "radius": 1 * mm});
            skCircle(sketch, "E27.18.20.0", {"center": v(18.9, 12.5) * mm, "radius": 1 * mm});
            skCircle(sketch, "E27.20.20.0", {"center": v(-30.6, 11) * mm, "radius": 1 * mm});
            skCircle(sketch, "E27.24.20.0", {"center": v(-44.1, 12.5) * mm, "radius": 1 * mm});
            skCircle(sketch, "E27.26.20.0", {"center": v(30.9, 12.5) * mm, "radius": 1 * mm});
            skCircle(sketch, "E27.28.20.0", {"center": v(-9.6, 11) * mm, "radius": 1 * mm});
            skCircle(sketch, "E27.32.20.0", {"center": v(-14.1, 12.5) * mm, "radius": 1 * mm});
            skCircle(sketch, "E27.34.20.0", {"center": v(-2.1, 12.5) * mm, "radius": 1 * mm});
            skCircle(sketch, "E27.36.20.0", {"center": v(9.9, 12.5) * mm, "radius": 1 * mm});
            skCircle(sketch, "E27.38.20.0", {"center": v(24.9, 12.5) * mm, "radius": 1 * mm});
            skCircle(sketch, "E27.40.20.0", {"center": v(5.4, 11) * mm, "radius": 1 * mm});
            skCircle(sketch, "E27.42.20.0", {"center": v(-23.1, 12.5) * mm, "radius": 1 * mm});
            skCircle(sketch, "E27.44.20.0", {"center": v(-5.1, 12.5) * mm, "radius": 1 * mm});
            skCircle(sketch, "E27.46.20.0", {"center": v(23.4, 11) * mm, "radius": 1 * mm});
            skCircle(sketch, "E27.48.20.0", {"center": v(42.9, 12.5) * mm, "radius": 1 * mm});
            skCircle(sketch, "E27.50.20.0", {"center": v(0.9, 12.5) * mm, "radius": 1 * mm});
            skCircle(sketch, "E27.52.20.0", {"center": v(-36.6, 11) * mm, "radius": 1 * mm});
            skCircle(sketch, "E27.54.20.0", {"center": v(41.4, 11) * mm, "radius": 1 * mm});
            skCircle(sketch, "E27.56.20.0", {"center": v(-12.6, 11) * mm, "radius": 1 * mm});
            skCircle(sketch, "E27.58.20.0", {"center": v(-26.1, 12.5) * mm, "radius": 1 * mm});
            skCircle(sketch, "E27.60.20.0", {"center": v(-8.1, 12.5) * mm, "radius": 1 * mm});
            skCircle(sketch, "E27.62.20.0", {"center": v(-27.6, 11) * mm, "radius": 1 * mm});
            skCircle(sketch, "E27.64.20.0", {"center": v(-29.1, 12.5) * mm, "radius": 1 * mm});
            skCircle(sketch, "E27.66.20.0", {"center": v(15.9, 12.5) * mm, "radius": 1 * mm});
            skCircle(sketch, "E27.68.20.0", {"center": v(-3.6, 11) * mm, "radius": 1 * mm});
            skCircle(sketch, "E27.70.20.0", {"center": v(-11.1, 12.5) * mm, "radius": 1 * mm});
            skCircle(sketch, "E27.72.20.0", {"center": v(44.4, 11) * mm, "radius": 1 * mm});
            skCircle(sketch, "E27.74.20.0", {"center": v(8.4, 11) * mm, "radius": 1 * mm});
            skCircle(sketch, "E27.76.20.0", {"center": v(33.9, 12.5) * mm, "radius": 1 * mm});
            skCircle(sketch, "E27.78.20.0", {"center": v(12.9, 12.5) * mm, "radius": 1 * mm});
            skCircle(sketch, "E27.80.20.0", {"center": v(-38.1, 12.5) * mm, "radius": 1 * mm});
            skCircle(sketch, "E27.82.20.0", {"center": v(-18.6, 11) * mm, "radius": 1 * mm});
            skCircle(sketch, "E27.84.20.0", {"center": v(-17.1, 12.5) * mm, "radius": 1 * mm});
            skCircle(sketch, "E27.86.20.0", {"center": v(48.9, 12.5) * mm, "radius": 1 * mm});
            skCircle(sketch, "E27.88.20.0", {"center": v(35.4, 11) * mm, "radius": 1 * mm});
            skCircle(sketch, "E27.90.20.0", {"center": v(11.4, 11) * mm, "radius": 1 * mm});
            skCircle(sketch, "E27.92.20.0", {"center": v(-24.6, 11) * mm, "radius": 1 * mm});
            skCircle(sketch, "E27.94.20.0", {"center": v(21.9, 12.5) * mm, "radius": 1 * mm});
            skCircle(sketch, "E27.96.20.0", {"center": v(50.4, 11) * mm, "radius": 1 * mm});
            skCircle(sketch, "E27.98.20.0", {"center": v(26.4, 11) * mm, "radius": 1 * mm});
            skCircle(sketch, "E27.100.20.0", {"center": v(20.4, 11) * mm, "radius": 1 * mm});
            skCircle(sketch, "E27.102.20.0", {"center": v(39.9, 12.5) * mm, "radius": 1 * mm});
            skCircle(sketch, "E27.104.20.0", {"center": v(-0.6, 11) * mm, "radius": 1 * mm});
            skCircle(sketch, "E27.106.20.0", {"center": v(47.4, 11) * mm, "radius": 1 * mm});
            skCircle(sketch, "E27.110.20.0", {"center": v(-39.6, 11) * mm, "radius": 1 * mm});
            skCircle(sketch, "E27.112.20.0", {"center": v(38.4, 11) * mm, "radius": 1 * mm});
            skCircle(sketch, "E27.114.20.0", {"center": v(-35.1, 12.5) * mm, "radius": 1 * mm});
            skCircle(sketch, "E27.116.20.0", {"center": v(17.4, 11) * mm, "radius": 1 * mm});
            skCircle(sketch, "E27.118.20.0", {"center": v(51.9, 12.5) * mm, "radius": 1 * mm});
            skCircle(sketch, "E27.120.20.0", {"center": v(-33.6, 11) * mm, "radius": 1 * mm});
            skCircle(sketch, "E27.124.20.0", {"center": v(-15.6, 11) * mm, "radius": 1 * mm});
            skCircle(sketch, "E27.126.20.0", {"center": v(14.4, 11) * mm, "radius": 1 * mm});
            skCircle(sketch, "E27.128.20.0", {"center": v(45.9, 12.5) * mm, "radius": 1 * mm});
            skCircle(sketch, "E27.130.20.0", {"center": v(-6.6, 11) * mm, "radius": 1 * mm});
            skCircle(sketch, "E27.132.20.0", {"center": v(32.4, 11) * mm, "radius": 1 * mm});
            skCircle(sketch, "E27.134.20.0", {"center": v(-21.6, 11) * mm, "radius": 1 * mm});
            skCircle(sketch, "E27.136.20.0", {"center": v(6.9, 12.5) * mm, "radius": 1 * mm});
            skCircle(sketch, "E27.138.20.0", {"center": v(-20.1, 12.5) * mm, "radius": 1 * mm});
            skCircle(sketch, "E27.140.20.0", {"center": v(-41.1, 12.5) * mm, "radius": 1 * mm});
            skCircle(sketch, "E27.144.20.0", {"center": v(-47.1, 12.5) * mm, "radius": 1 * mm});
            skCircle(sketch, "E27.146.20.0", {"center": v(-42.6, 11) * mm, "radius": 1 * mm});
            skCircle(sketch, "E27.148.20.0", {"center": v(-45.6, 11) * mm, "radius": 1 * mm});
            skCircle(sketch, "E27.150.20.0", {"center": v(-48.6, 11) * mm, "radius": 1 * mm});
            skLineSegment(sketch, "E27.152.20.0", {"start": v(-50.1, 12.5) * mm, "end": v(-50.1, 13.5) * mm, "construction": true});
            skCircle(sketch, "E27.155.20.0", {"center": v(-50.1, 12.5) * mm, "radius": 1 * mm});
            skLineSegment(sketch, "E27.157.20.0", {"start": v(-51.1, 12.5) * mm, "end": v(-50.1, 12.5) * mm, "construction": true});
            skLineSegment(sketch, "E27.160.20.0", {"start": v(-51.1, 11) * mm, "end": v(-48.6, 11) * mm, "construction": true});
            skLineSegment(sketch, "E27.163.20.0", {"start": v(-48.6, 11) * mm, "end": v(-48.6, 13.5) * mm, "construction": true});
            skCircle(sketch, "E27.0.21.0", {"center": v(27.9, 9.5) * mm, "radius": 1 * mm});
            skCircle(sketch, "E27.2.21.0", {"center": v(-32.1, 9.5) * mm, "radius": 1 * mm});
            skCircle(sketch, "E27.4.21.0", {"center": v(36.9, 9.5) * mm, "radius": 1 * mm});
            skCircle(sketch, "E27.6.21.0", {"center": v(3.9, 9.5) * mm, "radius": 1 * mm});
            skCircle(sketch, "E27.8.21.0", {"center": v(54.9, 9.5) * mm, "radius": 1 * mm});
            skCircle(sketch, "E27.10.21.0", {"center": v(53.4, 8) * mm, "radius": 1 * mm});
            skCircle(sketch, "E27.12.21.0", {"center": v(29.4, 8) * mm, "radius": 1 * mm});
            skCircle(sketch, "E27.14.21.0", {"center": v(2.4, 8) * mm, "radius": 1 * mm});
            skCircle(sketch, "E27.18.21.0", {"center": v(18.9, 9.5) * mm, "radius": 1 * mm});
            skCircle(sketch, "E27.20.21.0", {"center": v(-30.6, 8) * mm, "radius": 1 * mm});
            skCircle(sketch, "E27.24.21.0", {"center": v(-44.1, 9.5) * mm, "radius": 1 * mm});
            skCircle(sketch, "E27.26.21.0", {"center": v(30.9, 9.5) * mm, "radius": 1 * mm});
            skCircle(sketch, "E27.28.21.0", {"center": v(-9.6, 8) * mm, "radius": 1 * mm});
            skCircle(sketch, "E27.32.21.0", {"center": v(-14.1, 9.5) * mm, "radius": 1 * mm});
            skCircle(sketch, "E27.34.21.0", {"center": v(-2.1, 9.5) * mm, "radius": 1 * mm});
            skCircle(sketch, "E27.36.21.0", {"center": v(9.9, 9.5) * mm, "radius": 1 * mm});
            skCircle(sketch, "E27.38.21.0", {"center": v(24.9, 9.5) * mm, "radius": 1 * mm});
            skCircle(sketch, "E27.40.21.0", {"center": v(5.4, 8) * mm, "radius": 1 * mm});
            skCircle(sketch, "E27.42.21.0", {"center": v(-23.1, 9.5) * mm, "radius": 1 * mm});
            skCircle(sketch, "E27.44.21.0", {"center": v(-5.1, 9.5) * mm, "radius": 1 * mm});
            skCircle(sketch, "E27.46.21.0", {"center": v(23.4, 8) * mm, "radius": 1 * mm});
            skCircle(sketch, "E27.48.21.0", {"center": v(42.9, 9.5) * mm, "radius": 1 * mm});
            skCircle(sketch, "E27.50.21.0", {"center": v(0.9, 9.5) * mm, "radius": 1 * mm});
            skCircle(sketch, "E27.52.21.0", {"center": v(-36.6, 8) * mm, "radius": 1 * mm});
            skCircle(sketch, "E27.54.21.0", {"center": v(41.4, 8) * mm, "radius": 1 * mm});
            skCircle(sketch, "E27.56.21.0", {"center": v(-12.6, 8) * mm, "radius": 1 * mm});
            skCircle(sketch, "E27.58.21.0", {"center": v(-26.1, 9.5) * mm, "radius": 1 * mm});
            skCircle(sketch, "E27.60.21.0", {"center": v(-8.1, 9.5) * mm, "radius": 1 * mm});
            skCircle(sketch, "E27.62.21.0", {"center": v(-27.6, 8) * mm, "radius": 1 * mm});
            skCircle(sketch, "E27.64.21.0", {"center": v(-29.1, 9.5) * mm, "radius": 1 * mm});
            skCircle(sketch, "E27.66.21.0", {"center": v(15.9, 9.5) * mm, "radius": 1 * mm});
            skCircle(sketch, "E27.68.21.0", {"center": v(-3.6, 8) * mm, "radius": 1 * mm});
            skCircle(sketch, "E27.70.21.0", {"center": v(-11.1, 9.5) * mm, "radius": 1 * mm});
            skCircle(sketch, "E27.72.21.0", {"center": v(44.4, 8) * mm, "radius": 1 * mm});
            skCircle(sketch, "E27.74.21.0", {"center": v(8.4, 8) * mm, "radius": 1 * mm});
            skCircle(sketch, "E27.76.21.0", {"center": v(33.9, 9.5) * mm, "radius": 1 * mm});
            skCircle(sketch, "E27.78.21.0", {"center": v(12.9, 9.5) * mm, "radius": 1 * mm});
            skCircle(sketch, "E27.80.21.0", {"center": v(-38.1, 9.5) * mm, "radius": 1 * mm});
            skCircle(sketch, "E27.82.21.0", {"center": v(-18.6, 8) * mm, "radius": 1 * mm});
            skCircle(sketch, "E27.84.21.0", {"center": v(-17.1, 9.5) * mm, "radius": 1 * mm});
            skCircle(sketch, "E27.86.21.0", {"center": v(48.9, 9.5) * mm, "radius": 1 * mm});
            skCircle(sketch, "E27.88.21.0", {"center": v(35.4, 8) * mm, "radius": 1 * mm});
            skCircle(sketch, "E27.90.21.0", {"center": v(11.4, 8) * mm, "radius": 1 * mm});
            skCircle(sketch, "E27.92.21.0", {"center": v(-24.6, 8) * mm, "radius": 1 * mm});
            skCircle(sketch, "E27.94.21.0", {"center": v(21.9, 9.5) * mm, "radius": 1 * mm});
            skCircle(sketch, "E27.96.21.0", {"center": v(50.4, 8) * mm, "radius": 1 * mm});
            skCircle(sketch, "E27.98.21.0", {"center": v(26.4, 8) * mm, "radius": 1 * mm});
            skCircle(sketch, "E27.100.21.0", {"center": v(20.4, 8) * mm, "radius": 1 * mm});
            skCircle(sketch, "E27.102.21.0", {"center": v(39.9, 9.5) * mm, "radius": 1 * mm});
            skCircle(sketch, "E27.104.21.0", {"center": v(-0.6, 8) * mm, "radius": 1 * mm});
            skCircle(sketch, "E27.106.21.0", {"center": v(47.4, 8) * mm, "radius": 1 * mm});
            skCircle(sketch, "E27.110.21.0", {"center": v(-39.6, 8) * mm, "radius": 1 * mm});
            skCircle(sketch, "E27.112.21.0", {"center": v(38.4, 8) * mm, "radius": 1 * mm});
            skCircle(sketch, "E27.114.21.0", {"center": v(-35.1, 9.5) * mm, "radius": 1 * mm});
            skCircle(sketch, "E27.116.21.0", {"center": v(17.4, 8) * mm, "radius": 1 * mm});
            skCircle(sketch, "E27.118.21.0", {"center": v(51.9, 9.5) * mm, "radius": 1 * mm});
            skCircle(sketch, "E27.120.21.0", {"center": v(-33.6, 8) * mm, "radius": 1 * mm});
            skCircle(sketch, "E27.124.21.0", {"center": v(-15.6, 8) * mm, "radius": 1 * mm});
            skCircle(sketch, "E27.126.21.0", {"center": v(14.4, 8) * mm, "radius": 1 * mm});
            skCircle(sketch, "E27.128.21.0", {"center": v(45.9, 9.5) * mm, "radius": 1 * mm});
            skCircle(sketch, "E27.130.21.0", {"center": v(-6.6, 8) * mm, "radius": 1 * mm});
            skCircle(sketch, "E27.132.21.0", {"center": v(32.4, 8) * mm, "radius": 1 * mm});
            skCircle(sketch, "E27.134.21.0", {"center": v(-21.6, 8) * mm, "radius": 1 * mm});
            skCircle(sketch, "E27.136.21.0", {"center": v(6.9, 9.5) * mm, "radius": 1 * mm});
            skCircle(sketch, "E27.138.21.0", {"center": v(-20.1, 9.5) * mm, "radius": 1 * mm});
            skCircle(sketch, "E27.140.21.0", {"center": v(-41.1, 9.5) * mm, "radius": 1 * mm});
            skCircle(sketch, "E27.144.21.0", {"center": v(-47.1, 9.5) * mm, "radius": 1 * mm});
            skCircle(sketch, "E27.146.21.0", {"center": v(-42.6, 8) * mm, "radius": 1 * mm});
            skCircle(sketch, "E27.148.21.0", {"center": v(-45.6, 8) * mm, "radius": 1 * mm});
            skCircle(sketch, "E27.150.21.0", {"center": v(-48.6, 8) * mm, "radius": 1 * mm});
            skLineSegment(sketch, "E27.152.21.0", {"start": v(-50.1, 9.5) * mm, "end": v(-50.1, 10.5) * mm, "construction": true});
            skCircle(sketch, "E27.155.21.0", {"center": v(-50.1, 9.5) * mm, "radius": 1 * mm});
            skLineSegment(sketch, "E27.157.21.0", {"start": v(-51.1, 9.5) * mm, "end": v(-50.1, 9.5) * mm, "construction": true});
            skLineSegment(sketch, "E27.160.21.0", {"start": v(-51.1, 8) * mm, "end": v(-48.6, 8) * mm, "construction": true});
            skLineSegment(sketch, "E27.163.21.0", {"start": v(-48.6, 8) * mm, "end": v(-48.6, 10.5) * mm, "construction": true});
            skCircle(sketch, "E27.0.22.0", {"center": v(27.9, 6.5) * mm, "radius": 1 * mm});
            skCircle(sketch, "E27.2.22.0", {"center": v(-32.1, 6.5) * mm, "radius": 1 * mm});
            skCircle(sketch, "E27.4.22.0", {"center": v(36.9, 6.5) * mm, "radius": 1 * mm});
            skCircle(sketch, "E27.6.22.0", {"center": v(3.9, 6.5) * mm, "radius": 1 * mm});
            skCircle(sketch, "E27.8.22.0", {"center": v(54.9, 6.5) * mm, "radius": 1 * mm});
            skCircle(sketch, "E27.10.22.0", {"center": v(53.4, 5) * mm, "radius": 1 * mm});
            skCircle(sketch, "E27.12.22.0", {"center": v(29.4, 5) * mm, "radius": 1 * mm});
            skCircle(sketch, "E27.14.22.0", {"center": v(2.4, 5) * mm, "radius": 1 * mm});
            skCircle(sketch, "E27.18.22.0", {"center": v(18.9, 6.5) * mm, "radius": 1 * mm});
            skCircle(sketch, "E27.20.22.0", {"center": v(-30.6, 5) * mm, "radius": 1 * mm});
            skCircle(sketch, "E27.24.22.0", {"center": v(-44.1, 6.5) * mm, "radius": 1 * mm});
            skCircle(sketch, "E27.26.22.0", {"center": v(30.9, 6.5) * mm, "radius": 1 * mm});
            skCircle(sketch, "E27.28.22.0", {"center": v(-9.6, 5) * mm, "radius": 1 * mm});
            skCircle(sketch, "E27.32.22.0", {"center": v(-14.1, 6.5) * mm, "radius": 1 * mm});
            skCircle(sketch, "E27.34.22.0", {"center": v(-2.1, 6.5) * mm, "radius": 1 * mm});
            skCircle(sketch, "E27.36.22.0", {"center": v(9.9, 6.5) * mm, "radius": 1 * mm});
            skCircle(sketch, "E27.38.22.0", {"center": v(24.9, 6.5) * mm, "radius": 1 * mm});
            skCircle(sketch, "E27.40.22.0", {"center": v(5.4, 5) * mm, "radius": 1 * mm});
            skCircle(sketch, "E27.42.22.0", {"center": v(-23.1, 6.5) * mm, "radius": 1 * mm});
            skCircle(sketch, "E27.44.22.0", {"center": v(-5.1, 6.5) * mm, "radius": 1 * mm});
            skCircle(sketch, "E27.46.22.0", {"center": v(23.4, 5) * mm, "radius": 1 * mm});
            skCircle(sketch, "E27.48.22.0", {"center": v(42.9, 6.5) * mm, "radius": 1 * mm});
            skCircle(sketch, "E27.50.22.0", {"center": v(0.9, 6.5) * mm, "radius": 1 * mm});
            skCircle(sketch, "E27.52.22.0", {"center": v(-36.6, 5) * mm, "radius": 1 * mm});
            skCircle(sketch, "E27.54.22.0", {"center": v(41.4, 5) * mm, "radius": 1 * mm});
            skCircle(sketch, "E27.56.22.0", {"center": v(-12.6, 5) * mm, "radius": 1 * mm});
            skCircle(sketch, "E27.58.22.0", {"center": v(-26.1, 6.5) * mm, "radius": 1 * mm});
            skCircle(sketch, "E27.60.22.0", {"center": v(-8.1, 6.5) * mm, "radius": 1 * mm});
            skCircle(sketch, "E27.62.22.0", {"center": v(-27.6, 5) * mm, "radius": 1 * mm});
            skCircle(sketch, "E27.64.22.0", {"center": v(-29.1, 6.5) * mm, "radius": 1 * mm});
            skCircle(sketch, "E27.66.22.0", {"center": v(15.9, 6.5) * mm, "radius": 1 * mm});
            skCircle(sketch, "E27.68.22.0", {"center": v(-3.6, 5) * mm, "radius": 1 * mm});
            skCircle(sketch, "E27.70.22.0", {"center": v(-11.1, 6.5) * mm, "radius": 1 * mm});
            skCircle(sketch, "E27.72.22.0", {"center": v(44.4, 5) * mm, "radius": 1 * mm});
            skCircle(sketch, "E27.74.22.0", {"center": v(8.4, 5) * mm, "radius": 1 * mm});
            skCircle(sketch, "E27.76.22.0", {"center": v(33.9, 6.5) * mm, "radius": 1 * mm});
            skCircle(sketch, "E27.78.22.0", {"center": v(12.9, 6.5) * mm, "radius": 1 * mm});
            skCircle(sketch, "E27.80.22.0", {"center": v(-38.1, 6.5) * mm, "radius": 1 * mm});
            skCircle(sketch, "E27.82.22.0", {"center": v(-18.6, 5) * mm, "radius": 1 * mm});
            skCircle(sketch, "E27.84.22.0", {"center": v(-17.1, 6.5) * mm, "radius": 1 * mm});
            skCircle(sketch, "E27.86.22.0", {"center": v(48.9, 6.5) * mm, "radius": 1 * mm});
            skCircle(sketch, "E27.88.22.0", {"center": v(35.4, 5) * mm, "radius": 1 * mm});
            skCircle(sketch, "E27.90.22.0", {"center": v(11.4, 5) * mm, "radius": 1 * mm});
            skCircle(sketch, "E27.92.22.0", {"center": v(-24.6, 5) * mm, "radius": 1 * mm});
            skCircle(sketch, "E27.94.22.0", {"center": v(21.9, 6.5) * mm, "radius": 1 * mm});
            skCircle(sketch, "E27.96.22.0", {"center": v(50.4, 5) * mm, "radius": 1 * mm});
            skCircle(sketch, "E27.98.22.0", {"center": v(26.4, 5) * mm, "radius": 1 * mm});
            skCircle(sketch, "E27.100.22.0", {"center": v(20.4, 5) * mm, "radius": 1 * mm});
            skCircle(sketch, "E27.102.22.0", {"center": v(39.9, 6.5) * mm, "radius": 1 * mm});
            skCircle(sketch, "E27.104.22.0", {"center": v(-0.6, 5) * mm, "radius": 1 * mm});
            skCircle(sketch, "E27.106.22.0", {"center": v(47.4, 5) * mm, "radius": 1 * mm});
            skCircle(sketch, "E27.110.22.0", {"center": v(-39.6, 5) * mm, "radius": 1 * mm});
            skCircle(sketch, "E27.112.22.0", {"center": v(38.4, 5) * mm, "radius": 1 * mm});
            skCircle(sketch, "E27.114.22.0", {"center": v(-35.1, 6.5) * mm, "radius": 1 * mm});
            skCircle(sketch, "E27.116.22.0", {"center": v(17.4, 5) * mm, "radius": 1 * mm});
            skCircle(sketch, "E27.118.22.0", {"center": v(51.9, 6.5) * mm, "radius": 1 * mm});
            skCircle(sketch, "E27.120.22.0", {"center": v(-33.6, 5) * mm, "radius": 1 * mm});
            skCircle(sketch, "E27.124.22.0", {"center": v(-15.6, 5) * mm, "radius": 1 * mm});
            skCircle(sketch, "E27.126.22.0", {"center": v(14.4, 5) * mm, "radius": 1 * mm});
            skCircle(sketch, "E27.128.22.0", {"center": v(45.9, 6.5) * mm, "radius": 1 * mm});
            skCircle(sketch, "E27.130.22.0", {"center": v(-6.6, 5) * mm, "radius": 1 * mm});
            skCircle(sketch, "E27.132.22.0", {"center": v(32.4, 5) * mm, "radius": 1 * mm});
            skCircle(sketch, "E27.134.22.0", {"center": v(-21.6, 5) * mm, "radius": 1 * mm});
            skCircle(sketch, "E27.136.22.0", {"center": v(6.9, 6.5) * mm, "radius": 1 * mm});
            skCircle(sketch, "E27.138.22.0", {"center": v(-20.1, 6.5) * mm, "radius": 1 * mm});
            skCircle(sketch, "E27.140.22.0", {"center": v(-41.1, 6.5) * mm, "radius": 1 * mm});
            skCircle(sketch, "E27.144.22.0", {"center": v(-47.1, 6.5) * mm, "radius": 1 * mm});
            skCircle(sketch, "E27.146.22.0", {"center": v(-42.6, 5) * mm, "radius": 1 * mm});
            skCircle(sketch, "E27.148.22.0", {"center": v(-45.6, 5) * mm, "radius": 1 * mm});
            skCircle(sketch, "E27.150.22.0", {"center": v(-48.6, 5) * mm, "radius": 1 * mm});
            skLineSegment(sketch, "E27.152.22.0", {"start": v(-50.1, 6.5) * mm, "end": v(-50.1, 7.5) * mm, "construction": true});
            skCircle(sketch, "E27.155.22.0", {"center": v(-50.1, 6.5) * mm, "radius": 1 * mm});
            skLineSegment(sketch, "E27.157.22.0", {"start": v(-51.1, 6.5) * mm, "end": v(-50.1, 6.5) * mm, "construction": true});
            skLineSegment(sketch, "E27.160.22.0", {"start": v(-51.1, 5) * mm, "end": v(-48.6, 5) * mm, "construction": true});
            skLineSegment(sketch, "E27.163.22.0", {"start": v(-48.6, 5) * mm, "end": v(-48.6, 7.5) * mm, "construction": true});
            skCircle(sketch, "E27.0.23.0", {"center": v(27.9, 3.5) * mm, "radius": 1 * mm});
            skCircle(sketch, "E27.2.23.0", {"center": v(-32.1, 3.5) * mm, "radius": 1 * mm});
            skCircle(sketch, "E27.4.23.0", {"center": v(36.9, 3.5) * mm, "radius": 1 * mm});
            skCircle(sketch, "E27.6.23.0", {"center": v(3.9, 3.5) * mm, "radius": 1 * mm});
            skCircle(sketch, "E27.8.23.0", {"center": v(54.9, 3.5) * mm, "radius": 1 * mm});
            skCircle(sketch, "E27.10.23.0", {"center": v(53.4, 2) * mm, "radius": 1 * mm});
            skCircle(sketch, "E27.12.23.0", {"center": v(29.4, 2) * mm, "radius": 1 * mm});
            skCircle(sketch, "E27.14.23.0", {"center": v(2.4, 2) * mm, "radius": 1 * mm});
            skCircle(sketch, "E27.18.23.0", {"center": v(18.9, 3.5) * mm, "radius": 1 * mm});
            skCircle(sketch, "E27.20.23.0", {"center": v(-30.6, 2) * mm, "radius": 1 * mm});
            skCircle(sketch, "E27.24.23.0", {"center": v(-44.1, 3.5) * mm, "radius": 1 * mm});
            skCircle(sketch, "E27.26.23.0", {"center": v(30.9, 3.5) * mm, "radius": 1 * mm});
            skCircle(sketch, "E27.28.23.0", {"center": v(-9.6, 2) * mm, "radius": 1 * mm});
            skCircle(sketch, "E27.32.23.0", {"center": v(-14.1, 3.5) * mm, "radius": 1 * mm});
            skCircle(sketch, "E27.34.23.0", {"center": v(-2.1, 3.5) * mm, "radius": 1 * mm});
            skCircle(sketch, "E27.36.23.0", {"center": v(9.9, 3.5) * mm, "radius": 1 * mm});
            skCircle(sketch, "E27.38.23.0", {"center": v(24.9, 3.5) * mm, "radius": 1 * mm});
            skCircle(sketch, "E27.40.23.0", {"center": v(5.4, 2) * mm, "radius": 1 * mm});
            skCircle(sketch, "E27.42.23.0", {"center": v(-23.1, 3.5) * mm, "radius": 1 * mm});
            skCircle(sketch, "E27.44.23.0", {"center": v(-5.1, 3.5) * mm, "radius": 1 * mm});
            skCircle(sketch, "E27.46.23.0", {"center": v(23.4, 2) * mm, "radius": 1 * mm});
            skCircle(sketch, "E27.48.23.0", {"center": v(42.9, 3.5) * mm, "radius": 1 * mm});
            skCircle(sketch, "E27.50.23.0", {"center": v(0.9, 3.5) * mm, "radius": 1 * mm});
            skCircle(sketch, "E27.52.23.0", {"center": v(-36.6, 2) * mm, "radius": 1 * mm});
            skCircle(sketch, "E27.54.23.0", {"center": v(41.4, 2) * mm, "radius": 1 * mm});
            skCircle(sketch, "E27.56.23.0", {"center": v(-12.6, 2) * mm, "radius": 1 * mm});
            skCircle(sketch, "E27.58.23.0", {"center": v(-26.1, 3.5) * mm, "radius": 1 * mm});
            skCircle(sketch, "E27.60.23.0", {"center": v(-8.1, 3.5) * mm, "radius": 1 * mm});
            skCircle(sketch, "E27.62.23.0", {"center": v(-27.6, 2) * mm, "radius": 1 * mm});
            skCircle(sketch, "E27.64.23.0", {"center": v(-29.1, 3.5) * mm, "radius": 1 * mm});
            skCircle(sketch, "E27.66.23.0", {"center": v(15.9, 3.5) * mm, "radius": 1 * mm});
            skCircle(sketch, "E27.68.23.0", {"center": v(-3.6, 2) * mm, "radius": 1 * mm});
            skCircle(sketch, "E27.70.23.0", {"center": v(-11.1, 3.5) * mm, "radius": 1 * mm});
            skCircle(sketch, "E27.72.23.0", {"center": v(44.4, 2) * mm, "radius": 1 * mm});
            skCircle(sketch, "E27.74.23.0", {"center": v(8.4, 2) * mm, "radius": 1 * mm});
            skCircle(sketch, "E27.76.23.0", {"center": v(33.9, 3.5) * mm, "radius": 1 * mm});
            skCircle(sketch, "E27.78.23.0", {"center": v(12.9, 3.5) * mm, "radius": 1 * mm});
            skCircle(sketch, "E27.80.23.0", {"center": v(-38.1, 3.5) * mm, "radius": 1 * mm});
            skCircle(sketch, "E27.82.23.0", {"center": v(-18.6, 2) * mm, "radius": 1 * mm});
            skCircle(sketch, "E27.84.23.0", {"center": v(-17.1, 3.5) * mm, "radius": 1 * mm});
            skCircle(sketch, "E27.86.23.0", {"center": v(48.9, 3.5) * mm, "radius": 1 * mm});
            skCircle(sketch, "E27.88.23.0", {"center": v(35.4, 2) * mm, "radius": 1 * mm});
            skCircle(sketch, "E27.90.23.0", {"center": v(11.4, 2) * mm, "radius": 1 * mm});
            skCircle(sketch, "E27.92.23.0", {"center": v(-24.6, 2) * mm, "radius": 1 * mm});
            skCircle(sketch, "E27.94.23.0", {"center": v(21.9, 3.5) * mm, "radius": 1 * mm});
            skCircle(sketch, "E27.96.23.0", {"center": v(50.4, 2) * mm, "radius": 1 * mm});
            skCircle(sketch, "E27.98.23.0", {"center": v(26.4, 2) * mm, "radius": 1 * mm});
            skCircle(sketch, "E27.100.23.0", {"center": v(20.4, 2) * mm, "radius": 1 * mm});
            skCircle(sketch, "E27.102.23.0", {"center": v(39.9, 3.5) * mm, "radius": 1 * mm});
            skCircle(sketch, "E27.104.23.0", {"center": v(-0.6, 2) * mm, "radius": 1 * mm});
            skCircle(sketch, "E27.106.23.0", {"center": v(47.4, 2) * mm, "radius": 1 * mm});
            skCircle(sketch, "E27.110.23.0", {"center": v(-39.6, 2) * mm, "radius": 1 * mm});
            skCircle(sketch, "E27.112.23.0", {"center": v(38.4, 2) * mm, "radius": 1 * mm});
            skCircle(sketch, "E27.114.23.0", {"center": v(-35.1, 3.5) * mm, "radius": 1 * mm});
            skCircle(sketch, "E27.116.23.0", {"center": v(17.4, 2) * mm, "radius": 1 * mm});
            skCircle(sketch, "E27.118.23.0", {"center": v(51.9, 3.5) * mm, "radius": 1 * mm});
            skCircle(sketch, "E27.120.23.0", {"center": v(-33.6, 2) * mm, "radius": 1 * mm});
            skCircle(sketch, "E27.124.23.0", {"center": v(-15.6, 2) * mm, "radius": 1 * mm});
            skCircle(sketch, "E27.126.23.0", {"center": v(14.4, 2) * mm, "radius": 1 * mm});
            skCircle(sketch, "E27.128.23.0", {"center": v(45.9, 3.5) * mm, "radius": 1 * mm});
            skCircle(sketch, "E27.130.23.0", {"center": v(-6.6, 2) * mm, "radius": 1 * mm});
            skCircle(sketch, "E27.132.23.0", {"center": v(32.4, 2) * mm, "radius": 1 * mm});
            skCircle(sketch, "E27.134.23.0", {"center": v(-21.6, 2) * mm, "radius": 1 * mm});
            skCircle(sketch, "E27.136.23.0", {"center": v(6.9, 3.5) * mm, "radius": 1 * mm});
            skCircle(sketch, "E27.138.23.0", {"center": v(-20.1, 3.5) * mm, "radius": 1 * mm});
            skCircle(sketch, "E27.140.23.0", {"center": v(-41.1, 3.5) * mm, "radius": 1 * mm});
            skCircle(sketch, "E27.144.23.0", {"center": v(-47.1, 3.5) * mm, "radius": 1 * mm});
            skCircle(sketch, "E27.146.23.0", {"center": v(-42.6, 2) * mm, "radius": 1 * mm});
            skCircle(sketch, "E27.148.23.0", {"center": v(-45.6, 2) * mm, "radius": 1 * mm});
            skCircle(sketch, "E27.150.23.0", {"center": v(-48.6, 2) * mm, "radius": 1 * mm});
            skLineSegment(sketch, "E27.152.23.0", {"start": v(-50.1, 3.5) * mm, "end": v(-50.1, 4.5) * mm, "construction": true});
            skCircle(sketch, "E27.155.23.0", {"center": v(-50.1, 3.5) * mm, "radius": 1 * mm});
            skLineSegment(sketch, "E27.157.23.0", {"start": v(-51.1, 3.5) * mm, "end": v(-50.1, 3.5) * mm, "construction": true});
            skLineSegment(sketch, "E27.160.23.0", {"start": v(-51.1, 2) * mm, "end": v(-48.6, 2) * mm, "construction": true});
            skLineSegment(sketch, "E27.163.23.0", {"start": v(-48.6, 2) * mm, "end": v(-48.6, 4.5) * mm, "construction": true});
            skCircle(sketch, "E27.0.24.0", {"center": v(27.9, 0.5) * mm, "radius": 1 * mm});
            skCircle(sketch, "E27.2.24.0", {"center": v(-32.1, 0.5) * mm, "radius": 1 * mm});
            skCircle(sketch, "E27.4.24.0", {"center": v(36.9, 0.5) * mm, "radius": 1 * mm});
            skCircle(sketch, "E27.6.24.0", {"center": v(3.9, 0.5) * mm, "radius": 1 * mm});
            skCircle(sketch, "E27.8.24.0", {"center": v(54.9, 0.5) * mm, "radius": 1 * mm});
            skCircle(sketch, "E27.10.24.0", {"center": v(53.4, -1) * mm, "radius": 1 * mm});
            skCircle(sketch, "E27.12.24.0", {"center": v(29.4, -1) * mm, "radius": 1 * mm});
            skCircle(sketch, "E27.14.24.0", {"center": v(2.4, -1) * mm, "radius": 1 * mm});
            skCircle(sketch, "E27.18.24.0", {"center": v(18.9, 0.5) * mm, "radius": 1 * mm});
            skCircle(sketch, "E27.20.24.0", {"center": v(-30.6, -1) * mm, "radius": 1 * mm});
            skCircle(sketch, "E27.24.24.0", {"center": v(-44.1, 0.5) * mm, "radius": 1 * mm});
            skCircle(sketch, "E27.26.24.0", {"center": v(30.9, 0.5) * mm, "radius": 1 * mm});
            skCircle(sketch, "E27.28.24.0", {"center": v(-9.6, -1) * mm, "radius": 1 * mm});
            skCircle(sketch, "E27.32.24.0", {"center": v(-14.1, 0.5) * mm, "radius": 1 * mm});
            skCircle(sketch, "E27.34.24.0", {"center": v(-2.1, 0.5) * mm, "radius": 1 * mm});
            skCircle(sketch, "E27.36.24.0", {"center": v(9.9, 0.5) * mm, "radius": 1 * mm});
            skCircle(sketch, "E27.38.24.0", {"center": v(24.9, 0.5) * mm, "radius": 1 * mm});
            skCircle(sketch, "E27.40.24.0", {"center": v(5.4, -1) * mm, "radius": 1 * mm});
            skCircle(sketch, "E27.42.24.0", {"center": v(-23.1, 0.5) * mm, "radius": 1 * mm});
            skCircle(sketch, "E27.44.24.0", {"center": v(-5.1, 0.5) * mm, "radius": 1 * mm});
            skCircle(sketch, "E27.46.24.0", {"center": v(23.4, -1) * mm, "radius": 1 * mm});
            skCircle(sketch, "E27.48.24.0", {"center": v(42.9, 0.5) * mm, "radius": 1 * mm});
            skCircle(sketch, "E27.50.24.0", {"center": v(0.9, 0.5) * mm, "radius": 1 * mm});
            skCircle(sketch, "E27.52.24.0", {"center": v(-36.6, -1) * mm, "radius": 1 * mm});
            skCircle(sketch, "E27.54.24.0", {"center": v(41.4, -1) * mm, "radius": 1 * mm});
            skCircle(sketch, "E27.56.24.0", {"center": v(-12.6, -1) * mm, "radius": 1 * mm});
            skCircle(sketch, "E27.58.24.0", {"center": v(-26.1, 0.5) * mm, "radius": 1 * mm});
            skCircle(sketch, "E27.60.24.0", {"center": v(-8.1, 0.5) * mm, "radius": 1 * mm});
            skCircle(sketch, "E27.62.24.0", {"center": v(-27.6, -1) * mm, "radius": 1 * mm});
            skCircle(sketch, "E27.64.24.0", {"center": v(-29.1, 0.5) * mm, "radius": 1 * mm});
            skCircle(sketch, "E27.66.24.0", {"center": v(15.9, 0.5) * mm, "radius": 1 * mm});
            skCircle(sketch, "E27.68.24.0", {"center": v(-3.6, -1) * mm, "radius": 1 * mm});
            skCircle(sketch, "E27.70.24.0", {"center": v(-11.1, 0.5) * mm, "radius": 1 * mm});
            skCircle(sketch, "E27.72.24.0", {"center": v(44.4, -1) * mm, "radius": 1 * mm});
            skCircle(sketch, "E27.74.24.0", {"center": v(8.4, -1) * mm, "radius": 1 * mm});
            skCircle(sketch, "E27.76.24.0", {"center": v(33.9, 0.5) * mm, "radius": 1 * mm});
            skCircle(sketch, "E27.78.24.0", {"center": v(12.9, 0.5) * mm, "radius": 1 * mm});
            skCircle(sketch, "E27.80.24.0", {"center": v(-38.1, 0.5) * mm, "radius": 1 * mm});
            skCircle(sketch, "E27.82.24.0", {"center": v(-18.6, -1) * mm, "radius": 1 * mm});
            skCircle(sketch, "E27.84.24.0", {"center": v(-17.1, 0.5) * mm, "radius": 1 * mm});
            skCircle(sketch, "E27.86.24.0", {"center": v(48.9, 0.5) * mm, "radius": 1 * mm});
            skCircle(sketch, "E27.88.24.0", {"center": v(35.4, -1) * mm, "radius": 1 * mm});
            skCircle(sketch, "E27.90.24.0", {"center": v(11.4, -1) * mm, "radius": 1 * mm});
            skCircle(sketch, "E27.92.24.0", {"center": v(-24.6, -1) * mm, "radius": 1 * mm});
            skCircle(sketch, "E27.94.24.0", {"center": v(21.9, 0.5) * mm, "radius": 1 * mm});
            skCircle(sketch, "E27.96.24.0", {"center": v(50.4, -1) * mm, "radius": 1 * mm});
            skCircle(sketch, "E27.98.24.0", {"center": v(26.4, -1) * mm, "radius": 1 * mm});
            skCircle(sketch, "E27.100.24.0", {"center": v(20.4, -1) * mm, "radius": 1 * mm});
            skCircle(sketch, "E27.102.24.0", {"center": v(39.9, 0.5) * mm, "radius": 1 * mm});
            skCircle(sketch, "E27.104.24.0", {"center": v(-0.6, -1) * mm, "radius": 1 * mm});
            skCircle(sketch, "E27.106.24.0", {"center": v(47.4, -1) * mm, "radius": 1 * mm});
            skCircle(sketch, "E27.110.24.0", {"center": v(-39.6, -1) * mm, "radius": 1 * mm});
            skCircle(sketch, "E27.112.24.0", {"center": v(38.4, -1) * mm, "radius": 1 * mm});
            skCircle(sketch, "E27.114.24.0", {"center": v(-35.1, 0.5) * mm, "radius": 1 * mm});
            skCircle(sketch, "E27.116.24.0", {"center": v(17.4, -1) * mm, "radius": 1 * mm});
            skCircle(sketch, "E27.118.24.0", {"center": v(51.9, 0.5) * mm, "radius": 1 * mm});
            skCircle(sketch, "E27.120.24.0", {"center": v(-33.6, -1) * mm, "radius": 1 * mm});
            skCircle(sketch, "E27.124.24.0", {"center": v(-15.6, -1) * mm, "radius": 1 * mm});
            skCircle(sketch, "E27.126.24.0", {"center": v(14.4, -1) * mm, "radius": 1 * mm});
            skCircle(sketch, "E27.128.24.0", {"center": v(45.9, 0.5) * mm, "radius": 1 * mm});
            skCircle(sketch, "E27.130.24.0", {"center": v(-6.6, -1) * mm, "radius": 1 * mm});
            skCircle(sketch, "E27.132.24.0", {"center": v(32.4, -1) * mm, "radius": 1 * mm});
            skCircle(sketch, "E27.134.24.0", {"center": v(-21.6, -1) * mm, "radius": 1 * mm});
            skCircle(sketch, "E27.136.24.0", {"center": v(6.9, 0.5) * mm, "radius": 1 * mm});
            skCircle(sketch, "E27.138.24.0", {"center": v(-20.1, 0.5) * mm, "radius": 1 * mm});
            skCircle(sketch, "E27.140.24.0", {"center": v(-41.1, 0.5) * mm, "radius": 1 * mm});
            skCircle(sketch, "E27.144.24.0", {"center": v(-47.1, 0.5) * mm, "radius": 1 * mm});
            skCircle(sketch, "E27.146.24.0", {"center": v(-42.6, -1) * mm, "radius": 1 * mm});
            skCircle(sketch, "E27.148.24.0", {"center": v(-45.6, -1) * mm, "radius": 1 * mm});
            skCircle(sketch, "E27.150.24.0", {"center": v(-48.6, -1) * mm, "radius": 1 * mm});
            skLineSegment(sketch, "E27.152.24.0", {"start": v(-50.1, 0.5) * mm, "end": v(-50.1, 1.5) * mm, "construction": true});
            skCircle(sketch, "E27.155.24.0", {"center": v(-50.1, 0.5) * mm, "radius": 1 * mm});
            skLineSegment(sketch, "E27.157.24.0", {"start": v(-51.1, 0.5) * mm, "end": v(-50.1, 0.5) * mm, "construction": true});
            skLineSegment(sketch, "E27.160.24.0", {"start": v(-51.1, -1) * mm, "end": v(-48.6, -1) * mm, "construction": true});
            skLineSegment(sketch, "E27.163.24.0", {"start": v(-48.6, -1) * mm, "end": v(-48.6, 1.5) * mm, "construction": true});
            skCircle(sketch, "E27.0.25.0", {"center": v(27.9, -2.5) * mm, "radius": 1 * mm});
            skCircle(sketch, "E27.2.25.0", {"center": v(-32.1, -2.5) * mm, "radius": 1 * mm});
            skCircle(sketch, "E27.4.25.0", {"center": v(36.9, -2.5) * mm, "radius": 1 * mm});
            skCircle(sketch, "E27.6.25.0", {"center": v(3.9, -2.5) * mm, "radius": 1 * mm});
            skCircle(sketch, "E27.8.25.0", {"center": v(54.9, -2.5) * mm, "radius": 1 * mm});
            skCircle(sketch, "E27.10.25.0", {"center": v(53.4, -4) * mm, "radius": 1 * mm});
            skCircle(sketch, "E27.12.25.0", {"center": v(29.4, -4) * mm, "radius": 1 * mm});
            skCircle(sketch, "E27.14.25.0", {"center": v(2.4, -4) * mm, "radius": 1 * mm});
            skCircle(sketch, "E27.18.25.0", {"center": v(18.9, -2.5) * mm, "radius": 1 * mm});
            skCircle(sketch, "E27.20.25.0", {"center": v(-30.6, -4) * mm, "radius": 1 * mm});
            skCircle(sketch, "E27.24.25.0", {"center": v(-44.1, -2.5) * mm, "radius": 1 * mm});
            skCircle(sketch, "E27.26.25.0", {"center": v(30.9, -2.5) * mm, "radius": 1 * mm});
            skCircle(sketch, "E27.28.25.0", {"center": v(-9.6, -4) * mm, "radius": 1 * mm});
            skCircle(sketch, "E27.32.25.0", {"center": v(-14.1, -2.5) * mm, "radius": 1 * mm});
            skCircle(sketch, "E27.34.25.0", {"center": v(-2.1, -2.5) * mm, "radius": 1 * mm});
            skCircle(sketch, "E27.36.25.0", {"center": v(9.9, -2.5) * mm, "radius": 1 * mm});
            skCircle(sketch, "E27.38.25.0", {"center": v(24.9, -2.5) * mm, "radius": 1 * mm});
            skCircle(sketch, "E27.40.25.0", {"center": v(5.4, -4) * mm, "radius": 1 * mm});
            skCircle(sketch, "E27.42.25.0", {"center": v(-23.1, -2.5) * mm, "radius": 1 * mm});
            skCircle(sketch, "E27.44.25.0", {"center": v(-5.1, -2.5) * mm, "radius": 1 * mm});
            skCircle(sketch, "E27.46.25.0", {"center": v(23.4, -4) * mm, "radius": 1 * mm});
            skCircle(sketch, "E27.48.25.0", {"center": v(42.9, -2.5) * mm, "radius": 1 * mm});
            skCircle(sketch, "E27.50.25.0", {"center": v(0.9, -2.5) * mm, "radius": 1 * mm});
            skCircle(sketch, "E27.52.25.0", {"center": v(-36.6, -4) * mm, "radius": 1 * mm});
            skCircle(sketch, "E27.54.25.0", {"center": v(41.4, -4) * mm, "radius": 1 * mm});
            skCircle(sketch, "E27.56.25.0", {"center": v(-12.6, -4) * mm, "radius": 1 * mm});
            skCircle(sketch, "E27.58.25.0", {"center": v(-26.1, -2.5) * mm, "radius": 1 * mm});
            skCircle(sketch, "E27.60.25.0", {"center": v(-8.1, -2.5) * mm, "radius": 1 * mm});
            skCircle(sketch, "E27.62.25.0", {"center": v(-27.6, -4) * mm, "radius": 1 * mm});
            skCircle(sketch, "E27.64.25.0", {"center": v(-29.1, -2.5) * mm, "radius": 1 * mm});
            skCircle(sketch, "E27.66.25.0", {"center": v(15.9, -2.5) * mm, "radius": 1 * mm});
            skCircle(sketch, "E27.68.25.0", {"center": v(-3.6, -4) * mm, "radius": 1 * mm});
            skCircle(sketch, "E27.70.25.0", {"center": v(-11.1, -2.5) * mm, "radius": 1 * mm});
            skCircle(sketch, "E27.72.25.0", {"center": v(44.4, -4) * mm, "radius": 1 * mm});
            skCircle(sketch, "E27.74.25.0", {"center": v(8.4, -4) * mm, "radius": 1 * mm});
            skCircle(sketch, "E27.76.25.0", {"center": v(33.9, -2.5) * mm, "radius": 1 * mm});
            skCircle(sketch, "E27.78.25.0", {"center": v(12.9, -2.5) * mm, "radius": 1 * mm});
            skCircle(sketch, "E27.80.25.0", {"center": v(-38.1, -2.5) * mm, "radius": 1 * mm});
            skCircle(sketch, "E27.82.25.0", {"center": v(-18.6, -4) * mm, "radius": 1 * mm});
            skCircle(sketch, "E27.84.25.0", {"center": v(-17.1, -2.5) * mm, "radius": 1 * mm});
            skCircle(sketch, "E27.86.25.0", {"center": v(48.9, -2.5) * mm, "radius": 1 * mm});
            skCircle(sketch, "E27.88.25.0", {"center": v(35.4, -4) * mm, "radius": 1 * mm});
            skCircle(sketch, "E27.90.25.0", {"center": v(11.4, -4) * mm, "radius": 1 * mm});
            skCircle(sketch, "E27.92.25.0", {"center": v(-24.6, -4) * mm, "radius": 1 * mm});
            skCircle(sketch, "E27.94.25.0", {"center": v(21.9, -2.5) * mm, "radius": 1 * mm});
            skCircle(sketch, "E27.96.25.0", {"center": v(50.4, -4) * mm, "radius": 1 * mm});
            skCircle(sketch, "E27.98.25.0", {"center": v(26.4, -4) * mm, "radius": 1 * mm});
            skCircle(sketch, "E27.100.25.0", {"center": v(20.4, -4) * mm, "radius": 1 * mm});
            skCircle(sketch, "E27.102.25.0", {"center": v(39.9, -2.5) * mm, "radius": 1 * mm});
            skCircle(sketch, "E27.104.25.0", {"center": v(-0.6, -4) * mm, "radius": 1 * mm});
            skCircle(sketch, "E27.106.25.0", {"center": v(47.4, -4) * mm, "radius": 1 * mm});
            skCircle(sketch, "E27.110.25.0", {"center": v(-39.6, -4) * mm, "radius": 1 * mm});
            skCircle(sketch, "E27.112.25.0", {"center": v(38.4, -4) * mm, "radius": 1 * mm});
            skCircle(sketch, "E27.114.25.0", {"center": v(-35.1, -2.5) * mm, "radius": 1 * mm});
            skCircle(sketch, "E27.116.25.0", {"center": v(17.4, -4) * mm, "radius": 1 * mm});
            skCircle(sketch, "E27.118.25.0", {"center": v(51.9, -2.5) * mm, "radius": 1 * mm});
            skCircle(sketch, "E27.120.25.0", {"center": v(-33.6, -4) * mm, "radius": 1 * mm});
            skCircle(sketch, "E27.124.25.0", {"center": v(-15.6, -4) * mm, "radius": 1 * mm});
            skCircle(sketch, "E27.126.25.0", {"center": v(14.4, -4) * mm, "radius": 1 * mm});
            skCircle(sketch, "E27.128.25.0", {"center": v(45.9, -2.5) * mm, "radius": 1 * mm});
            skCircle(sketch, "E27.130.25.0", {"center": v(-6.6, -4) * mm, "radius": 1 * mm});
            skCircle(sketch, "E27.132.25.0", {"center": v(32.4, -4) * mm, "radius": 1 * mm});
            skCircle(sketch, "E27.134.25.0", {"center": v(-21.6, -4) * mm, "radius": 1 * mm});
            skCircle(sketch, "E27.136.25.0", {"center": v(6.9, -2.5) * mm, "radius": 1 * mm});
            skCircle(sketch, "E27.138.25.0", {"center": v(-20.1, -2.5) * mm, "radius": 1 * mm});
            skCircle(sketch, "E27.140.25.0", {"center": v(-41.1, -2.5) * mm, "radius": 1 * mm});
            skCircle(sketch, "E27.144.25.0", {"center": v(-47.1, -2.5) * mm, "radius": 1 * mm});
            skCircle(sketch, "E27.146.25.0", {"center": v(-42.6, -4) * mm, "radius": 1 * mm});
            skCircle(sketch, "E27.148.25.0", {"center": v(-45.6, -4) * mm, "radius": 1 * mm});
            skCircle(sketch, "E27.150.25.0", {"center": v(-48.6, -4) * mm, "radius": 1 * mm});
            skLineSegment(sketch, "E27.152.25.0", {"start": v(-50.1, -2.5) * mm, "end": v(-50.1, -1.5) * mm, "construction": true});
            skCircle(sketch, "E27.155.25.0", {"center": v(-50.1, -2.5) * mm, "radius": 1 * mm});
            skLineSegment(sketch, "E27.157.25.0", {"start": v(-51.1, -2.5) * mm, "end": v(-50.1, -2.5) * mm, "construction": true});
            skLineSegment(sketch, "E27.160.25.0", {"start": v(-51.1, -4) * mm, "end": v(-48.6, -4) * mm, "construction": true});
            skLineSegment(sketch, "E27.163.25.0", {"start": v(-48.6, -4) * mm, "end": v(-48.6, -1.5) * mm, "construction": true});
            skCircle(sketch, "E27.0.26.0", {"center": v(27.9, -5.5) * mm, "radius": 1 * mm});
            skCircle(sketch, "E27.2.26.0", {"center": v(-32.1, -5.5) * mm, "radius": 1 * mm});
            skCircle(sketch, "E27.4.26.0", {"center": v(36.9, -5.5) * mm, "radius": 1 * mm});
            skCircle(sketch, "E27.6.26.0", {"center": v(3.9, -5.5) * mm, "radius": 1 * mm});
            skCircle(sketch, "E27.8.26.0", {"center": v(54.9, -5.5) * mm, "radius": 1 * mm});
            skCircle(sketch, "E27.10.26.0", {"center": v(53.4, -7) * mm, "radius": 1 * mm});
            skCircle(sketch, "E27.12.26.0", {"center": v(29.4, -7) * mm, "radius": 1 * mm});
            skCircle(sketch, "E27.14.26.0", {"center": v(2.4, -7) * mm, "radius": 1 * mm});
            skCircle(sketch, "E27.18.26.0", {"center": v(18.9, -5.5) * mm, "radius": 1 * mm});
            skCircle(sketch, "E27.20.26.0", {"center": v(-30.6, -7) * mm, "radius": 1 * mm});
            skCircle(sketch, "E27.24.26.0", {"center": v(-44.1, -5.5) * mm, "radius": 1 * mm});
            skCircle(sketch, "E27.26.26.0", {"center": v(30.9, -5.5) * mm, "radius": 1 * mm});
            skCircle(sketch, "E27.28.26.0", {"center": v(-9.6, -7) * mm, "radius": 1 * mm});
            skCircle(sketch, "E27.32.26.0", {"center": v(-14.1, -5.5) * mm, "radius": 1 * mm});
            skCircle(sketch, "E27.34.26.0", {"center": v(-2.1, -5.5) * mm, "radius": 1 * mm});
            skCircle(sketch, "E27.36.26.0", {"center": v(9.9, -5.5) * mm, "radius": 1 * mm});
            skCircle(sketch, "E27.38.26.0", {"center": v(24.9, -5.5) * mm, "radius": 1 * mm});
            skCircle(sketch, "E27.40.26.0", {"center": v(5.4, -7) * mm, "radius": 1 * mm});
            skCircle(sketch, "E27.42.26.0", {"center": v(-23.1, -5.5) * mm, "radius": 1 * mm});
            skCircle(sketch, "E27.44.26.0", {"center": v(-5.1, -5.5) * mm, "radius": 1 * mm});
            skCircle(sketch, "E27.46.26.0", {"center": v(23.4, -7) * mm, "radius": 1 * mm});
            skCircle(sketch, "E27.48.26.0", {"center": v(42.9, -5.5) * mm, "radius": 1 * mm});
            skCircle(sketch, "E27.50.26.0", {"center": v(0.9, -5.5) * mm, "radius": 1 * mm});
            skCircle(sketch, "E27.52.26.0", {"center": v(-36.6, -7) * mm, "radius": 1 * mm});
            skCircle(sketch, "E27.54.26.0", {"center": v(41.4, -7) * mm, "radius": 1 * mm});
            skCircle(sketch, "E27.56.26.0", {"center": v(-12.6, -7) * mm, "radius": 1 * mm});
            skCircle(sketch, "E27.58.26.0", {"center": v(-26.1, -5.5) * mm, "radius": 1 * mm});
            skCircle(sketch, "E27.60.26.0", {"center": v(-8.1, -5.5) * mm, "radius": 1 * mm});
            skCircle(sketch, "E27.62.26.0", {"center": v(-27.6, -7) * mm, "radius": 1 * mm});
            skCircle(sketch, "E27.64.26.0", {"center": v(-29.1, -5.5) * mm, "radius": 1 * mm});
            skCircle(sketch, "E27.66.26.0", {"center": v(15.9, -5.5) * mm, "radius": 1 * mm});
            skCircle(sketch, "E27.68.26.0", {"center": v(-3.6, -7) * mm, "radius": 1 * mm});
            skCircle(sketch, "E27.70.26.0", {"center": v(-11.1, -5.5) * mm, "radius": 1 * mm});
            skCircle(sketch, "E27.72.26.0", {"center": v(44.4, -7) * mm, "radius": 1 * mm});
            skCircle(sketch, "E27.74.26.0", {"center": v(8.4, -7) * mm, "radius": 1 * mm});
            skCircle(sketch, "E27.76.26.0", {"center": v(33.9, -5.5) * mm, "radius": 1 * mm});
            skCircle(sketch, "E27.78.26.0", {"center": v(12.9, -5.5) * mm, "radius": 1 * mm});
            skCircle(sketch, "E27.80.26.0", {"center": v(-38.1, -5.5) * mm, "radius": 1 * mm});
            skCircle(sketch, "E27.82.26.0", {"center": v(-18.6, -7) * mm, "radius": 1 * mm});
            skCircle(sketch, "E27.84.26.0", {"center": v(-17.1, -5.5) * mm, "radius": 1 * mm});
            skCircle(sketch, "E27.86.26.0", {"center": v(48.9, -5.5) * mm, "radius": 1 * mm});
            skCircle(sketch, "E27.88.26.0", {"center": v(35.4, -7) * mm, "radius": 1 * mm});
            skCircle(sketch, "E27.90.26.0", {"center": v(11.4, -7) * mm, "radius": 1 * mm});
            skCircle(sketch, "E27.92.26.0", {"center": v(-24.6, -7) * mm, "radius": 1 * mm});
            skCircle(sketch, "E27.94.26.0", {"center": v(21.9, -5.5) * mm, "radius": 1 * mm});
            skCircle(sketch, "E27.96.26.0", {"center": v(50.4, -7) * mm, "radius": 1 * mm});
            skCircle(sketch, "E27.98.26.0", {"center": v(26.4, -7) * mm, "radius": 1 * mm});
            skCircle(sketch, "E27.100.26.0", {"center": v(20.4, -7) * mm, "radius": 1 * mm});
            skCircle(sketch, "E27.102.26.0", {"center": v(39.9, -5.5) * mm, "radius": 1 * mm});
            skCircle(sketch, "E27.104.26.0", {"center": v(-0.6, -7) * mm, "radius": 1 * mm});
            skCircle(sketch, "E27.106.26.0", {"center": v(47.4, -7) * mm, "radius": 1 * mm});
            skCircle(sketch, "E27.110.26.0", {"center": v(-39.6, -7) * mm, "radius": 1 * mm});
            skCircle(sketch, "E27.112.26.0", {"center": v(38.4, -7) * mm, "radius": 1 * mm});
            skCircle(sketch, "E27.114.26.0", {"center": v(-35.1, -5.5) * mm, "radius": 1 * mm});
            skCircle(sketch, "E27.116.26.0", {"center": v(17.4, -7) * mm, "radius": 1 * mm});
            skCircle(sketch, "E27.118.26.0", {"center": v(51.9, -5.5) * mm, "radius": 1 * mm});
            skCircle(sketch, "E27.120.26.0", {"center": v(-33.6, -7) * mm, "radius": 1 * mm});
            skCircle(sketch, "E27.124.26.0", {"center": v(-15.6, -7) * mm, "radius": 1 * mm});
            skCircle(sketch, "E27.126.26.0", {"center": v(14.4, -7) * mm, "radius": 1 * mm});
            skCircle(sketch, "E27.128.26.0", {"center": v(45.9, -5.5) * mm, "radius": 1 * mm});
            skCircle(sketch, "E27.130.26.0", {"center": v(-6.6, -7) * mm, "radius": 1 * mm});
            skCircle(sketch, "E27.132.26.0", {"center": v(32.4, -7) * mm, "radius": 1 * mm});
            skCircle(sketch, "E27.134.26.0", {"center": v(-21.6, -7) * mm, "radius": 1 * mm});
            skCircle(sketch, "E27.136.26.0", {"center": v(6.9, -5.5) * mm, "radius": 1 * mm});
            skCircle(sketch, "E27.138.26.0", {"center": v(-20.1, -5.5) * mm, "radius": 1 * mm});
            skCircle(sketch, "E27.140.26.0", {"center": v(-41.1, -5.5) * mm, "radius": 1 * mm});
            skCircle(sketch, "E27.144.26.0", {"center": v(-47.1, -5.5) * mm, "radius": 1 * mm});
            skCircle(sketch, "E27.146.26.0", {"center": v(-42.6, -7) * mm, "radius": 1 * mm});
            skCircle(sketch, "E27.148.26.0", {"center": v(-45.6, -7) * mm, "radius": 1 * mm});
            skCircle(sketch, "E27.150.26.0", {"center": v(-48.6, -7) * mm, "radius": 1 * mm});
            skLineSegment(sketch, "E27.152.26.0", {"start": v(-50.1, -5.5) * mm, "end": v(-50.1, -4.5) * mm, "construction": true});
            skCircle(sketch, "E27.155.26.0", {"center": v(-50.1, -5.5) * mm, "radius": 1 * mm});
            skLineSegment(sketch, "E27.157.26.0", {"start": v(-51.1, -5.5) * mm, "end": v(-50.1, -5.5) * mm, "construction": true});
            skLineSegment(sketch, "E27.160.26.0", {"start": v(-51.1, -7) * mm, "end": v(-48.6, -7) * mm, "construction": true});
            skLineSegment(sketch, "E27.163.26.0", {"start": v(-48.6, -7) * mm, "end": v(-48.6, -4.5) * mm, "construction": true});
            skCircle(sketch, "E27.0.27.0", {"center": v(27.9, -8.5) * mm, "radius": 1 * mm});
            skCircle(sketch, "E27.2.27.0", {"center": v(-32.1, -8.5) * mm, "radius": 1 * mm});
            skCircle(sketch, "E27.4.27.0", {"center": v(36.9, -8.5) * mm, "radius": 1 * mm});
            skCircle(sketch, "E27.6.27.0", {"center": v(3.9, -8.5) * mm, "radius": 1 * mm});
            skCircle(sketch, "E27.8.27.0", {"center": v(54.9, -8.5) * mm, "radius": 1 * mm});
            skCircle(sketch, "E27.10.27.0", {"center": v(53.4, -10) * mm, "radius": 1 * mm});
            skCircle(sketch, "E27.12.27.0", {"center": v(29.4, -10) * mm, "radius": 1 * mm});
            skCircle(sketch, "E27.14.27.0", {"center": v(2.4, -10) * mm, "radius": 1 * mm});
            skCircle(sketch, "E27.18.27.0", {"center": v(18.9, -8.5) * mm, "radius": 1 * mm});
            skCircle(sketch, "E27.20.27.0", {"center": v(-30.6, -10) * mm, "radius": 1 * mm});
            skCircle(sketch, "E27.24.27.0", {"center": v(-44.1, -8.5) * mm, "radius": 1 * mm});
            skCircle(sketch, "E27.26.27.0", {"center": v(30.9, -8.5) * mm, "radius": 1 * mm});
            skCircle(sketch, "E27.28.27.0", {"center": v(-9.6, -10) * mm, "radius": 1 * mm});
            skCircle(sketch, "E27.32.27.0", {"center": v(-14.1, -8.5) * mm, "radius": 1 * mm});
            skCircle(sketch, "E27.34.27.0", {"center": v(-2.1, -8.5) * mm, "radius": 1 * mm});
            skCircle(sketch, "E27.36.27.0", {"center": v(9.9, -8.5) * mm, "radius": 1 * mm});
            skCircle(sketch, "E27.38.27.0", {"center": v(24.9, -8.5) * mm, "radius": 1 * mm});
            skCircle(sketch, "E27.40.27.0", {"center": v(5.4, -10) * mm, "radius": 1 * mm});
            skCircle(sketch, "E27.42.27.0", {"center": v(-23.1, -8.5) * mm, "radius": 1 * mm});
            skCircle(sketch, "E27.44.27.0", {"center": v(-5.1, -8.5) * mm, "radius": 1 * mm});
            skCircle(sketch, "E27.46.27.0", {"center": v(23.4, -10) * mm, "radius": 1 * mm});
            skCircle(sketch, "E27.48.27.0", {"center": v(42.9, -8.5) * mm, "radius": 1 * mm});
            skCircle(sketch, "E27.50.27.0", {"center": v(0.9, -8.5) * mm, "radius": 1 * mm});
            skCircle(sketch, "E27.52.27.0", {"center": v(-36.6, -10) * mm, "radius": 1 * mm});
            skCircle(sketch, "E27.54.27.0", {"center": v(41.4, -10) * mm, "radius": 1 * mm});
            skCircle(sketch, "E27.56.27.0", {"center": v(-12.6, -10) * mm, "radius": 1 * mm});
            skCircle(sketch, "E27.58.27.0", {"center": v(-26.1, -8.5) * mm, "radius": 1 * mm});
            skCircle(sketch, "E27.60.27.0", {"center": v(-8.1, -8.5) * mm, "radius": 1 * mm});
            skCircle(sketch, "E27.62.27.0", {"center": v(-27.6, -10) * mm, "radius": 1 * mm});
            skCircle(sketch, "E27.64.27.0", {"center": v(-29.1, -8.5) * mm, "radius": 1 * mm});
            skCircle(sketch, "E27.66.27.0", {"center": v(15.9, -8.5) * mm, "radius": 1 * mm});
            skCircle(sketch, "E27.68.27.0", {"center": v(-3.6, -10) * mm, "radius": 1 * mm});
            skCircle(sketch, "E27.70.27.0", {"center": v(-11.1, -8.5) * mm, "radius": 1 * mm});
            skCircle(sketch, "E27.72.27.0", {"center": v(44.4, -10) * mm, "radius": 1 * mm});
            skCircle(sketch, "E27.74.27.0", {"center": v(8.4, -10) * mm, "radius": 1 * mm});
            skCircle(sketch, "E27.76.27.0", {"center": v(33.9, -8.5) * mm, "radius": 1 * mm});
            skCircle(sketch, "E27.78.27.0", {"center": v(12.9, -8.5) * mm, "radius": 1 * mm});
            skCircle(sketch, "E27.80.27.0", {"center": v(-38.1, -8.5) * mm, "radius": 1 * mm});
            skCircle(sketch, "E27.82.27.0", {"center": v(-18.6, -10) * mm, "radius": 1 * mm});
            skCircle(sketch, "E27.84.27.0", {"center": v(-17.1, -8.5) * mm, "radius": 1 * mm});
            skCircle(sketch, "E27.86.27.0", {"center": v(48.9, -8.5) * mm, "radius": 1 * mm});
            skCircle(sketch, "E27.88.27.0", {"center": v(35.4, -10) * mm, "radius": 1 * mm});
            skCircle(sketch, "E27.90.27.0", {"center": v(11.4, -10) * mm, "radius": 1 * mm});
            skCircle(sketch, "E27.92.27.0", {"center": v(-24.6, -10) * mm, "radius": 1 * mm});
            skCircle(sketch, "E27.94.27.0", {"center": v(21.9, -8.5) * mm, "radius": 1 * mm});
            skCircle(sketch, "E27.96.27.0", {"center": v(50.4, -10) * mm, "radius": 1 * mm});
            skCircle(sketch, "E27.98.27.0", {"center": v(26.4, -10) * mm, "radius": 1 * mm});
            skCircle(sketch, "E27.100.27.0", {"center": v(20.4, -10) * mm, "radius": 1 * mm});
            skCircle(sketch, "E27.102.27.0", {"center": v(39.9, -8.5) * mm, "radius": 1 * mm});
            skCircle(sketch, "E27.104.27.0", {"center": v(-0.6, -10) * mm, "radius": 1 * mm});
            skCircle(sketch, "E27.106.27.0", {"center": v(47.4, -10) * mm, "radius": 1 * mm});
            skCircle(sketch, "E27.110.27.0", {"center": v(-39.6, -10) * mm, "radius": 1 * mm});
            skCircle(sketch, "E27.112.27.0", {"center": v(38.4, -10) * mm, "radius": 1 * mm});
            skCircle(sketch, "E27.114.27.0", {"center": v(-35.1, -8.5) * mm, "radius": 1 * mm});
            skCircle(sketch, "E27.116.27.0", {"center": v(17.4, -10) * mm, "radius": 1 * mm});
            skCircle(sketch, "E27.118.27.0", {"center": v(51.9, -8.5) * mm, "radius": 1 * mm});
            skCircle(sketch, "E27.120.27.0", {"center": v(-33.6, -10) * mm, "radius": 1 * mm});
            skCircle(sketch, "E27.124.27.0", {"center": v(-15.6, -10) * mm, "radius": 1 * mm});
            skCircle(sketch, "E27.126.27.0", {"center": v(14.4, -10) * mm, "radius": 1 * mm});
            skCircle(sketch, "E27.128.27.0", {"center": v(45.9, -8.5) * mm, "radius": 1 * mm});
            skCircle(sketch, "E27.130.27.0", {"center": v(-6.6, -10) * mm, "radius": 1 * mm});
            skCircle(sketch, "E27.132.27.0", {"center": v(32.4, -10) * mm, "radius": 1 * mm});
            skCircle(sketch, "E27.134.27.0", {"center": v(-21.6, -10) * mm, "radius": 1 * mm});
            skCircle(sketch, "E27.136.27.0", {"center": v(6.9, -8.5) * mm, "radius": 1 * mm});
            skCircle(sketch, "E27.138.27.0", {"center": v(-20.1, -8.5) * mm, "radius": 1 * mm});
            skCircle(sketch, "E27.140.27.0", {"center": v(-41.1, -8.5) * mm, "radius": 1 * mm});
            skCircle(sketch, "E27.144.27.0", {"center": v(-47.1, -8.5) * mm, "radius": 1 * mm});
            skCircle(sketch, "E27.146.27.0", {"center": v(-42.6, -10) * mm, "radius": 1 * mm});
            skCircle(sketch, "E27.148.27.0", {"center": v(-45.6, -10) * mm, "radius": 1 * mm});
            skCircle(sketch, "E27.150.27.0", {"center": v(-48.6, -10) * mm, "radius": 1 * mm});
            skLineSegment(sketch, "E27.152.27.0", {"start": v(-50.1, -8.5) * mm, "end": v(-50.1, -7.5) * mm, "construction": true});
            skCircle(sketch, "E27.155.27.0", {"center": v(-50.1, -8.5) * mm, "radius": 1 * mm});
            skLineSegment(sketch, "E27.157.27.0", {"start": v(-51.1, -8.5) * mm, "end": v(-50.1, -8.5) * mm, "construction": true});
            skLineSegment(sketch, "E27.160.27.0", {"start": v(-51.1, -10) * mm, "end": v(-48.6, -10) * mm, "construction": true});
            skLineSegment(sketch, "E27.163.27.0", {"start": v(-48.6, -10) * mm, "end": v(-48.6, -7.5) * mm, "construction": true});
            skCircle(sketch, "E27.0.28.0", {"center": v(27.9, -11.5) * mm, "radius": 1 * mm});
            skCircle(sketch, "E27.2.28.0", {"center": v(-32.1, -11.5) * mm, "radius": 1 * mm});
            skCircle(sketch, "E27.4.28.0", {"center": v(36.9, -11.5) * mm, "radius": 1 * mm});
            skCircle(sketch, "E27.6.28.0", {"center": v(3.9, -11.5) * mm, "radius": 1 * mm});
            skCircle(sketch, "E27.8.28.0", {"center": v(54.9, -11.5) * mm, "radius": 1 * mm});
            skCircle(sketch, "E27.10.28.0", {"center": v(53.4, -13) * mm, "radius": 1 * mm});
            skCircle(sketch, "E27.12.28.0", {"center": v(29.4, -13) * mm, "radius": 1 * mm});
            skCircle(sketch, "E27.14.28.0", {"center": v(2.4, -13) * mm, "radius": 1 * mm});
            skCircle(sketch, "E27.18.28.0", {"center": v(18.9, -11.5) * mm, "radius": 1 * mm});
            skCircle(sketch, "E27.20.28.0", {"center": v(-30.6, -13) * mm, "radius": 1 * mm});
            skCircle(sketch, "E27.24.28.0", {"center": v(-44.1, -11.5) * mm, "radius": 1 * mm});
            skCircle(sketch, "E27.26.28.0", {"center": v(30.9, -11.5) * mm, "radius": 1 * mm});
            skCircle(sketch, "E27.28.28.0", {"center": v(-9.6, -13) * mm, "radius": 1 * mm});
            skCircle(sketch, "E27.32.28.0", {"center": v(-14.1, -11.5) * mm, "radius": 1 * mm});
            skCircle(sketch, "E27.34.28.0", {"center": v(-2.1, -11.5) * mm, "radius": 1 * mm});
            skCircle(sketch, "E27.36.28.0", {"center": v(9.9, -11.5) * mm, "radius": 1 * mm});
            skCircle(sketch, "E27.38.28.0", {"center": v(24.9, -11.5) * mm, "radius": 1 * mm});
            skCircle(sketch, "E27.40.28.0", {"center": v(5.4, -13) * mm, "radius": 1 * mm});
            skCircle(sketch, "E27.42.28.0", {"center": v(-23.1, -11.5) * mm, "radius": 1 * mm});
            skCircle(sketch, "E27.44.28.0", {"center": v(-5.1, -11.5) * mm, "radius": 1 * mm});
            skCircle(sketch, "E27.46.28.0", {"center": v(23.4, -13) * mm, "radius": 1 * mm});
            skCircle(sketch, "E27.48.28.0", {"center": v(42.9, -11.5) * mm, "radius": 1 * mm});
            skCircle(sketch, "E27.50.28.0", {"center": v(0.9, -11.5) * mm, "radius": 1 * mm});
            skCircle(sketch, "E27.52.28.0", {"center": v(-36.6, -13) * mm, "radius": 1 * mm});
            skCircle(sketch, "E27.54.28.0", {"center": v(41.4, -13) * mm, "radius": 1 * mm});
            skCircle(sketch, "E27.56.28.0", {"center": v(-12.6, -13) * mm, "radius": 1 * mm});
            skCircle(sketch, "E27.58.28.0", {"center": v(-26.1, -11.5) * mm, "radius": 1 * mm});
            skCircle(sketch, "E27.60.28.0", {"center": v(-8.1, -11.5) * mm, "radius": 1 * mm});
            skCircle(sketch, "E27.62.28.0", {"center": v(-27.6, -13) * mm, "radius": 1 * mm});
            skCircle(sketch, "E27.64.28.0", {"center": v(-29.1, -11.5) * mm, "radius": 1 * mm});
            skCircle(sketch, "E27.66.28.0", {"center": v(15.9, -11.5) * mm, "radius": 1 * mm});
            skCircle(sketch, "E27.68.28.0", {"center": v(-3.6, -13) * mm, "radius": 1 * mm});
            skCircle(sketch, "E27.70.28.0", {"center": v(-11.1, -11.5) * mm, "radius": 1 * mm});
            skCircle(sketch, "E27.72.28.0", {"center": v(44.4, -13) * mm, "radius": 1 * mm});
            skCircle(sketch, "E27.74.28.0", {"center": v(8.4, -13) * mm, "radius": 1 * mm});
            skCircle(sketch, "E27.76.28.0", {"center": v(33.9, -11.5) * mm, "radius": 1 * mm});
            skCircle(sketch, "E27.78.28.0", {"center": v(12.9, -11.5) * mm, "radius": 1 * mm});
            skCircle(sketch, "E27.80.28.0", {"center": v(-38.1, -11.5) * mm, "radius": 1 * mm});
            skCircle(sketch, "E27.82.28.0", {"center": v(-18.6, -13) * mm, "radius": 1 * mm});
            skCircle(sketch, "E27.84.28.0", {"center": v(-17.1, -11.5) * mm, "radius": 1 * mm});
            skCircle(sketch, "E27.86.28.0", {"center": v(48.9, -11.5) * mm, "radius": 1 * mm});
            skCircle(sketch, "E27.88.28.0", {"center": v(35.4, -13) * mm, "radius": 1 * mm});
            skCircle(sketch, "E27.90.28.0", {"center": v(11.4, -13) * mm, "radius": 1 * mm});
            skCircle(sketch, "E27.92.28.0", {"center": v(-24.6, -13) * mm, "radius": 1 * mm});
            skCircle(sketch, "E27.94.28.0", {"center": v(21.9, -11.5) * mm, "radius": 1 * mm});
            skCircle(sketch, "E27.96.28.0", {"center": v(50.4, -13) * mm, "radius": 1 * mm});
            skCircle(sketch, "E27.98.28.0", {"center": v(26.4, -13) * mm, "radius": 1 * mm});
            skCircle(sketch, "E27.100.28.0", {"center": v(20.4, -13) * mm, "radius": 1 * mm});
            skCircle(sketch, "E27.102.28.0", {"center": v(39.9, -11.5) * mm, "radius": 1 * mm});
            skCircle(sketch, "E27.104.28.0", {"center": v(-0.6, -13) * mm, "radius": 1 * mm});
            skCircle(sketch, "E27.106.28.0", {"center": v(47.4, -13) * mm, "radius": 1 * mm});
            skCircle(sketch, "E27.110.28.0", {"center": v(-39.6, -13) * mm, "radius": 1 * mm});
            skCircle(sketch, "E27.112.28.0", {"center": v(38.4, -13) * mm, "radius": 1 * mm});
            skCircle(sketch, "E27.114.28.0", {"center": v(-35.1, -11.5) * mm, "radius": 1 * mm});
            skCircle(sketch, "E27.116.28.0", {"center": v(17.4, -13) * mm, "radius": 1 * mm});
            skCircle(sketch, "E27.118.28.0", {"center": v(51.9, -11.5) * mm, "radius": 1 * mm});
            skCircle(sketch, "E27.120.28.0", {"center": v(-33.6, -13) * mm, "radius": 1 * mm});
            skCircle(sketch, "E27.124.28.0", {"center": v(-15.6, -13) * mm, "radius": 1 * mm});
            skCircle(sketch, "E27.126.28.0", {"center": v(14.4, -13) * mm, "radius": 1 * mm});
            skCircle(sketch, "E27.128.28.0", {"center": v(45.9, -11.5) * mm, "radius": 1 * mm});
            skCircle(sketch, "E27.130.28.0", {"center": v(-6.6, -13) * mm, "radius": 1 * mm});
            skCircle(sketch, "E27.132.28.0", {"center": v(32.4, -13) * mm, "radius": 1 * mm});
            skCircle(sketch, "E27.134.28.0", {"center": v(-21.6, -13) * mm, "radius": 1 * mm});
            skCircle(sketch, "E27.136.28.0", {"center": v(6.9, -11.5) * mm, "radius": 1 * mm});
            skCircle(sketch, "E27.138.28.0", {"center": v(-20.1, -11.5) * mm, "radius": 1 * mm});
            skCircle(sketch, "E27.140.28.0", {"center": v(-41.1, -11.5) * mm, "radius": 1 * mm});
            skCircle(sketch, "E27.144.28.0", {"center": v(-47.1, -11.5) * mm, "radius": 1 * mm});
            skCircle(sketch, "E27.146.28.0", {"center": v(-42.6, -13) * mm, "radius": 1 * mm});
            skCircle(sketch, "E27.148.28.0", {"center": v(-45.6, -13) * mm, "radius": 1 * mm});
            skCircle(sketch, "E27.150.28.0", {"center": v(-48.6, -13) * mm, "radius": 1 * mm});
            skLineSegment(sketch, "E27.152.28.0", {"start": v(-50.1, -11.5) * mm, "end": v(-50.1, -10.5) * mm, "construction": true});
            skCircle(sketch, "E27.155.28.0", {"center": v(-50.1, -11.5) * mm, "radius": 1 * mm});
            skLineSegment(sketch, "E27.157.28.0", {"start": v(-51.1, -11.5) * mm, "end": v(-50.1, -11.5) * mm, "construction": true});
            skLineSegment(sketch, "E27.160.28.0", {"start": v(-51.1, -13) * mm, "end": v(-48.6, -13) * mm, "construction": true});
            skLineSegment(sketch, "E27.163.28.0", {"start": v(-48.6, -13) * mm, "end": v(-48.6, -10.5) * mm, "construction": true});
            skCircle(sketch, "E27.0.29.0", {"center": v(27.9, -14.5) * mm, "radius": 1 * mm});
            skCircle(sketch, "E27.2.29.0", {"center": v(-32.1, -14.5) * mm, "radius": 1 * mm});
            skCircle(sketch, "E27.4.29.0", {"center": v(36.9, -14.5) * mm, "radius": 1 * mm});
            skCircle(sketch, "E27.6.29.0", {"center": v(3.9, -14.5) * mm, "radius": 1 * mm});
            skCircle(sketch, "E27.8.29.0", {"center": v(54.9, -14.5) * mm, "radius": 1 * mm});
            skCircle(sketch, "E27.10.29.0", {"center": v(53.4, -16) * mm, "radius": 1 * mm});
            skCircle(sketch, "E27.12.29.0", {"center": v(29.4, -16) * mm, "radius": 1 * mm});
            skCircle(sketch, "E27.14.29.0", {"center": v(2.4, -16) * mm, "radius": 1 * mm});
            skCircle(sketch, "E27.18.29.0", {"center": v(18.9, -14.5) * mm, "radius": 1 * mm});
            skCircle(sketch, "E27.20.29.0", {"center": v(-30.6, -16) * mm, "radius": 1 * mm});
            skCircle(sketch, "E27.24.29.0", {"center": v(-44.1, -14.5) * mm, "radius": 1 * mm});
            skCircle(sketch, "E27.26.29.0", {"center": v(30.9, -14.5) * mm, "radius": 1 * mm});
            skCircle(sketch, "E27.28.29.0", {"center": v(-9.6, -16) * mm, "radius": 1 * mm});
            skCircle(sketch, "E27.32.29.0", {"center": v(-14.1, -14.5) * mm, "radius": 1 * mm});
            skCircle(sketch, "E27.34.29.0", {"center": v(-2.1, -14.5) * mm, "radius": 1 * mm});
            skCircle(sketch, "E27.36.29.0", {"center": v(9.9, -14.5) * mm, "radius": 1 * mm});
            skCircle(sketch, "E27.38.29.0", {"center": v(24.9, -14.5) * mm, "radius": 1 * mm});
            skCircle(sketch, "E27.40.29.0", {"center": v(5.4, -16) * mm, "radius": 1 * mm});
            skCircle(sketch, "E27.42.29.0", {"center": v(-23.1, -14.5) * mm, "radius": 1 * mm});
            skCircle(sketch, "E27.44.29.0", {"center": v(-5.1, -14.5) * mm, "radius": 1 * mm});
            skCircle(sketch, "E27.46.29.0", {"center": v(23.4, -16) * mm, "radius": 1 * mm});
            skCircle(sketch, "E27.48.29.0", {"center": v(42.9, -14.5) * mm, "radius": 1 * mm});
            skCircle(sketch, "E27.50.29.0", {"center": v(0.9, -14.5) * mm, "radius": 1 * mm});
            skCircle(sketch, "E27.52.29.0", {"center": v(-36.6, -16) * mm, "radius": 1 * mm});
            skCircle(sketch, "E27.54.29.0", {"center": v(41.4, -16) * mm, "radius": 1 * mm});
            skCircle(sketch, "E27.56.29.0", {"center": v(-12.6, -16) * mm, "radius": 1 * mm});
            skCircle(sketch, "E27.58.29.0", {"center": v(-26.1, -14.5) * mm, "radius": 1 * mm});
            skCircle(sketch, "E27.60.29.0", {"center": v(-8.1, -14.5) * mm, "radius": 1 * mm});
            skCircle(sketch, "E27.62.29.0", {"center": v(-27.6, -16) * mm, "radius": 1 * mm});
            skCircle(sketch, "E27.64.29.0", {"center": v(-29.1, -14.5) * mm, "radius": 1 * mm});
            skCircle(sketch, "E27.66.29.0", {"center": v(15.9, -14.5) * mm, "radius": 1 * mm});
            skCircle(sketch, "E27.68.29.0", {"center": v(-3.6, -16) * mm, "radius": 1 * mm});
            skCircle(sketch, "E27.70.29.0", {"center": v(-11.1, -14.5) * mm, "radius": 1 * mm});
            skCircle(sketch, "E27.72.29.0", {"center": v(44.4, -16) * mm, "radius": 1 * mm});
            skCircle(sketch, "E27.74.29.0", {"center": v(8.4, -16) * mm, "radius": 1 * mm});
            skCircle(sketch, "E27.76.29.0", {"center": v(33.9, -14.5) * mm, "radius": 1 * mm});
            skCircle(sketch, "E27.78.29.0", {"center": v(12.9, -14.5) * mm, "radius": 1 * mm});
            skCircle(sketch, "E27.80.29.0", {"center": v(-38.1, -14.5) * mm, "radius": 1 * mm});
            skCircle(sketch, "E27.82.29.0", {"center": v(-18.6, -16) * mm, "radius": 1 * mm});
            skCircle(sketch, "E27.84.29.0", {"center": v(-17.1, -14.5) * mm, "radius": 1 * mm});
            skCircle(sketch, "E27.86.29.0", {"center": v(48.9, -14.5) * mm, "radius": 1 * mm});
            skCircle(sketch, "E27.88.29.0", {"center": v(35.4, -16) * mm, "radius": 1 * mm});
            skCircle(sketch, "E27.90.29.0", {"center": v(11.4, -16) * mm, "radius": 1 * mm});
            skCircle(sketch, "E27.92.29.0", {"center": v(-24.6, -16) * mm, "radius": 1 * mm});
            skCircle(sketch, "E27.94.29.0", {"center": v(21.9, -14.5) * mm, "radius": 1 * mm});
            skCircle(sketch, "E27.96.29.0", {"center": v(50.4, -16) * mm, "radius": 1 * mm});
            skCircle(sketch, "E27.98.29.0", {"center": v(26.4, -16) * mm, "radius": 1 * mm});
            skCircle(sketch, "E27.100.29.0", {"center": v(20.4, -16) * mm, "radius": 1 * mm});
            skCircle(sketch, "E27.102.29.0", {"center": v(39.9, -14.5) * mm, "radius": 1 * mm});
            skCircle(sketch, "E27.104.29.0", {"center": v(-0.6, -16) * mm, "radius": 1 * mm});
            skCircle(sketch, "E27.106.29.0", {"center": v(47.4, -16) * mm, "radius": 1 * mm});
            skCircle(sketch, "E27.110.29.0", {"center": v(-39.6, -16) * mm, "radius": 1 * mm});
            skCircle(sketch, "E27.112.29.0", {"center": v(38.4, -16) * mm, "radius": 1 * mm});
            skCircle(sketch, "E27.114.29.0", {"center": v(-35.1, -14.5) * mm, "radius": 1 * mm});
            skCircle(sketch, "E27.116.29.0", {"center": v(17.4, -16) * mm, "radius": 1 * mm});
            skCircle(sketch, "E27.118.29.0", {"center": v(51.9, -14.5) * mm, "radius": 1 * mm});
            skCircle(sketch, "E27.120.29.0", {"center": v(-33.6, -16) * mm, "radius": 1 * mm});
            skCircle(sketch, "E27.124.29.0", {"center": v(-15.6, -16) * mm, "radius": 1 * mm});
            skCircle(sketch, "E27.126.29.0", {"center": v(14.4, -16) * mm, "radius": 1 * mm});
            skCircle(sketch, "E27.128.29.0", {"center": v(45.9, -14.5) * mm, "radius": 1 * mm});
            skCircle(sketch, "E27.130.29.0", {"center": v(-6.6, -16) * mm, "radius": 1 * mm});
            skCircle(sketch, "E27.132.29.0", {"center": v(32.4, -16) * mm, "radius": 1 * mm});
            skCircle(sketch, "E27.134.29.0", {"center": v(-21.6, -16) * mm, "radius": 1 * mm});
            skCircle(sketch, "E27.136.29.0", {"center": v(6.9, -14.5) * mm, "radius": 1 * mm});
            skCircle(sketch, "E27.138.29.0", {"center": v(-20.1, -14.5) * mm, "radius": 1 * mm});
            skCircle(sketch, "E27.140.29.0", {"center": v(-41.1, -14.5) * mm, "radius": 1 * mm});
            skCircle(sketch, "E27.144.29.0", {"center": v(-47.1, -14.5) * mm, "radius": 1 * mm});
            skCircle(sketch, "E27.146.29.0", {"center": v(-42.6, -16) * mm, "radius": 1 * mm});
            skCircle(sketch, "E27.148.29.0", {"center": v(-45.6, -16) * mm, "radius": 1 * mm});
            skCircle(sketch, "E27.150.29.0", {"center": v(-48.6, -16) * mm, "radius": 1 * mm});
            skLineSegment(sketch, "E27.152.29.0", {"start": v(-50.1, -14.5) * mm, "end": v(-50.1, -13.5) * mm, "construction": true});
            skCircle(sketch, "E27.155.29.0", {"center": v(-50.1, -14.5) * mm, "radius": 1 * mm});
            skLineSegment(sketch, "E27.157.29.0", {"start": v(-51.1, -14.5) * mm, "end": v(-50.1, -14.5) * mm, "construction": true});
            skLineSegment(sketch, "E27.160.29.0", {"start": v(-51.1, -16) * mm, "end": v(-48.6, -16) * mm, "construction": true});
            skLineSegment(sketch, "E27.163.29.0", {"start": v(-48.6, -16) * mm, "end": v(-48.6, -13.5) * mm, "construction": true});
            skCircle(sketch, "E27.0.30.0", {"center": v(27.9, -17.5) * mm, "radius": 1 * mm});
            skCircle(sketch, "E27.2.30.0", {"center": v(-32.1, -17.5) * mm, "radius": 1 * mm});
            skCircle(sketch, "E27.4.30.0", {"center": v(36.9, -17.5) * mm, "radius": 1 * mm});
            skCircle(sketch, "E27.6.30.0", {"center": v(3.9, -17.5) * mm, "radius": 1 * mm});
            skCircle(sketch, "E27.8.30.0", {"center": v(54.9, -17.5) * mm, "radius": 1 * mm});
            skCircle(sketch, "E27.10.30.0", {"center": v(53.4, -19) * mm, "radius": 1 * mm});
            skCircle(sketch, "E27.12.30.0", {"center": v(29.4, -19) * mm, "radius": 1 * mm});
            skCircle(sketch, "E27.14.30.0", {"center": v(2.4, -19) * mm, "radius": 1 * mm});
            skCircle(sketch, "E27.18.30.0", {"center": v(18.9, -17.5) * mm, "radius": 1 * mm});
            skCircle(sketch, "E27.20.30.0", {"center": v(-30.6, -19) * mm, "radius": 1 * mm});
            skCircle(sketch, "E27.24.30.0", {"center": v(-44.1, -17.5) * mm, "radius": 1 * mm});
            skCircle(sketch, "E27.26.30.0", {"center": v(30.9, -17.5) * mm, "radius": 1 * mm});
            skCircle(sketch, "E27.28.30.0", {"center": v(-9.6, -19) * mm, "radius": 1 * mm});
            skCircle(sketch, "E27.32.30.0", {"center": v(-14.1, -17.5) * mm, "radius": 1 * mm});
            skCircle(sketch, "E27.34.30.0", {"center": v(-2.1, -17.5) * mm, "radius": 1 * mm});
            skCircle(sketch, "E27.36.30.0", {"center": v(9.9, -17.5) * mm, "radius": 1 * mm});
            skCircle(sketch, "E27.38.30.0", {"center": v(24.9, -17.5) * mm, "radius": 1 * mm});
            skCircle(sketch, "E27.40.30.0", {"center": v(5.4, -19) * mm, "radius": 1 * mm});
            skCircle(sketch, "E27.42.30.0", {"center": v(-23.1, -17.5) * mm, "radius": 1 * mm});
            skCircle(sketch, "E27.44.30.0", {"center": v(-5.1, -17.5) * mm, "radius": 1 * mm});
            skCircle(sketch, "E27.46.30.0", {"center": v(23.4, -19) * mm, "radius": 1 * mm});
            skCircle(sketch, "E27.48.30.0", {"center": v(42.9, -17.5) * mm, "radius": 1 * mm});
            skCircle(sketch, "E27.50.30.0", {"center": v(0.9, -17.5) * mm, "radius": 1 * mm});
            skCircle(sketch, "E27.52.30.0", {"center": v(-36.6, -19) * mm, "radius": 1 * mm});
            skCircle(sketch, "E27.54.30.0", {"center": v(41.4, -19) * mm, "radius": 1 * mm});
            skCircle(sketch, "E27.56.30.0", {"center": v(-12.6, -19) * mm, "radius": 1 * mm});
            skCircle(sketch, "E27.58.30.0", {"center": v(-26.1, -17.5) * mm, "radius": 1 * mm});
            skCircle(sketch, "E27.60.30.0", {"center": v(-8.1, -17.5) * mm, "radius": 1 * mm});
            skCircle(sketch, "E27.62.30.0", {"center": v(-27.6, -19) * mm, "radius": 1 * mm});
            skCircle(sketch, "E27.64.30.0", {"center": v(-29.1, -17.5) * mm, "radius": 1 * mm});
            skCircle(sketch, "E27.66.30.0", {"center": v(15.9, -17.5) * mm, "radius": 1 * mm});
            skCircle(sketch, "E27.68.30.0", {"center": v(-3.6, -19) * mm, "radius": 1 * mm});
            skCircle(sketch, "E27.70.30.0", {"center": v(-11.1, -17.5) * mm, "radius": 1 * mm});
            skCircle(sketch, "E27.72.30.0", {"center": v(44.4, -19) * mm, "radius": 1 * mm});
            skCircle(sketch, "E27.74.30.0", {"center": v(8.4, -19) * mm, "radius": 1 * mm});
            skCircle(sketch, "E27.76.30.0", {"center": v(33.9, -17.5) * mm, "radius": 1 * mm});
            skCircle(sketch, "E27.78.30.0", {"center": v(12.9, -17.5) * mm, "radius": 1 * mm});
            skCircle(sketch, "E27.80.30.0", {"center": v(-38.1, -17.5) * mm, "radius": 1 * mm});
            skCircle(sketch, "E27.82.30.0", {"center": v(-18.6, -19) * mm, "radius": 1 * mm});
            skCircle(sketch, "E27.84.30.0", {"center": v(-17.1, -17.5) * mm, "radius": 1 * mm});
            skCircle(sketch, "E27.86.30.0", {"center": v(48.9, -17.5) * mm, "radius": 1 * mm});
            skCircle(sketch, "E27.88.30.0", {"center": v(35.4, -19) * mm, "radius": 1 * mm});
            skCircle(sketch, "E27.90.30.0", {"center": v(11.4, -19) * mm, "radius": 1 * mm});
            skCircle(sketch, "E27.92.30.0", {"center": v(-24.6, -19) * mm, "radius": 1 * mm});
            skCircle(sketch, "E27.94.30.0", {"center": v(21.9, -17.5) * mm, "radius": 1 * mm});
            skCircle(sketch, "E27.96.30.0", {"center": v(50.4, -19) * mm, "radius": 1 * mm});
            skCircle(sketch, "E27.98.30.0", {"center": v(26.4, -19) * mm, "radius": 1 * mm});
            skCircle(sketch, "E27.100.30.0", {"center": v(20.4, -19) * mm, "radius": 1 * mm});
            skCircle(sketch, "E27.102.30.0", {"center": v(39.9, -17.5) * mm, "radius": 1 * mm});
            skCircle(sketch, "E27.104.30.0", {"center": v(-0.6, -19) * mm, "radius": 1 * mm});
            skCircle(sketch, "E27.106.30.0", {"center": v(47.4, -19) * mm, "radius": 1 * mm});
            skCircle(sketch, "E27.110.30.0", {"center": v(-39.6, -19) * mm, "radius": 1 * mm});
            skCircle(sketch, "E27.112.30.0", {"center": v(38.4, -19) * mm, "radius": 1 * mm});
            skCircle(sketch, "E27.114.30.0", {"center": v(-35.1, -17.5) * mm, "radius": 1 * mm});
            skCircle(sketch, "E27.116.30.0", {"center": v(17.4, -19) * mm, "radius": 1 * mm});
            skCircle(sketch, "E27.118.30.0", {"center": v(51.9, -17.5) * mm, "radius": 1 * mm});
            skCircle(sketch, "E27.120.30.0", {"center": v(-33.6, -19) * mm, "radius": 1 * mm});
            skCircle(sketch, "E27.124.30.0", {"center": v(-15.6, -19) * mm, "radius": 1 * mm});
            skCircle(sketch, "E27.126.30.0", {"center": v(14.4, -19) * mm, "radius": 1 * mm});
            skCircle(sketch, "E27.128.30.0", {"center": v(45.9, -17.5) * mm, "radius": 1 * mm});
            skCircle(sketch, "E27.130.30.0", {"center": v(-6.6, -19) * mm, "radius": 1 * mm});
            skCircle(sketch, "E27.132.30.0", {"center": v(32.4, -19) * mm, "radius": 1 * mm});
            skCircle(sketch, "E27.134.30.0", {"center": v(-21.6, -19) * mm, "radius": 1 * mm});
            skCircle(sketch, "E27.136.30.0", {"center": v(6.9, -17.5) * mm, "radius": 1 * mm});
            skCircle(sketch, "E27.138.30.0", {"center": v(-20.1, -17.5) * mm, "radius": 1 * mm});
            skCircle(sketch, "E27.140.30.0", {"center": v(-41.1, -17.5) * mm, "radius": 1 * mm});
            skCircle(sketch, "E27.144.30.0", {"center": v(-47.1, -17.5) * mm, "radius": 1 * mm});
            skCircle(sketch, "E27.146.30.0", {"center": v(-42.6, -19) * mm, "radius": 1 * mm});
            skCircle(sketch, "E27.148.30.0", {"center": v(-45.6, -19) * mm, "radius": 1 * mm});
            skCircle(sketch, "E27.150.30.0", {"center": v(-48.6, -19) * mm, "radius": 1 * mm});
            skLineSegment(sketch, "E27.152.30.0", {"start": v(-50.1, -17.5) * mm, "end": v(-50.1, -16.5) * mm, "construction": true});
            skCircle(sketch, "E27.155.30.0", {"center": v(-50.1, -17.5) * mm, "radius": 1 * mm});
            skLineSegment(sketch, "E27.157.30.0", {"start": v(-51.1, -17.5) * mm, "end": v(-50.1, -17.5) * mm, "construction": true});
            skLineSegment(sketch, "E27.160.30.0", {"start": v(-51.1, -19) * mm, "end": v(-48.6, -19) * mm, "construction": true});
            skLineSegment(sketch, "E27.163.30.0", {"start": v(-48.6, -19) * mm, "end": v(-48.6, -16.5) * mm, "construction": true});
            skCircle(sketch, "E27.0.31.0", {"center": v(27.9, -20.5) * mm, "radius": 1 * mm});
            skCircle(sketch, "E27.2.31.0", {"center": v(-32.1, -20.5) * mm, "radius": 1 * mm});
            skCircle(sketch, "E27.4.31.0", {"center": v(36.9, -20.5) * mm, "radius": 1 * mm});
            skCircle(sketch, "E27.6.31.0", {"center": v(3.9, -20.5) * mm, "radius": 1 * mm});
            skCircle(sketch, "E27.8.31.0", {"center": v(54.9, -20.5) * mm, "radius": 1 * mm});
            skCircle(sketch, "E27.10.31.0", {"center": v(53.4, -22) * mm, "radius": 1 * mm});
            skCircle(sketch, "E27.12.31.0", {"center": v(29.4, -22) * mm, "radius": 1 * mm});
            skCircle(sketch, "E27.14.31.0", {"center": v(2.4, -22) * mm, "radius": 1 * mm});
            skCircle(sketch, "E27.18.31.0", {"center": v(18.9, -20.5) * mm, "radius": 1 * mm});
            skCircle(sketch, "E27.20.31.0", {"center": v(-30.6, -22) * mm, "radius": 1 * mm});
            skCircle(sketch, "E27.24.31.0", {"center": v(-44.1, -20.5) * mm, "radius": 1 * mm});
            skCircle(sketch, "E27.26.31.0", {"center": v(30.9, -20.5) * mm, "radius": 1 * mm});
            skCircle(sketch, "E27.28.31.0", {"center": v(-9.6, -22) * mm, "radius": 1 * mm});
            skCircle(sketch, "E27.32.31.0", {"center": v(-14.1, -20.5) * mm, "radius": 1 * mm});
            skCircle(sketch, "E27.34.31.0", {"center": v(-2.1, -20.5) * mm, "radius": 1 * mm});
            skCircle(sketch, "E27.36.31.0", {"center": v(9.9, -20.5) * mm, "radius": 1 * mm});
            skCircle(sketch, "E27.38.31.0", {"center": v(24.9, -20.5) * mm, "radius": 1 * mm});
            skCircle(sketch, "E27.40.31.0", {"center": v(5.4, -22) * mm, "radius": 1 * mm});
            skCircle(sketch, "E27.42.31.0", {"center": v(-23.1, -20.5) * mm, "radius": 1 * mm});
            skCircle(sketch, "E27.44.31.0", {"center": v(-5.1, -20.5) * mm, "radius": 1 * mm});
            skCircle(sketch, "E27.46.31.0", {"center": v(23.4, -22) * mm, "radius": 1 * mm});
            skCircle(sketch, "E27.48.31.0", {"center": v(42.9, -20.5) * mm, "radius": 1 * mm});
            skCircle(sketch, "E27.50.31.0", {"center": v(0.9, -20.5) * mm, "radius": 1 * mm});
            skCircle(sketch, "E27.52.31.0", {"center": v(-36.6, -22) * mm, "radius": 1 * mm});
            skCircle(sketch, "E27.54.31.0", {"center": v(41.4, -22) * mm, "radius": 1 * mm});
            skCircle(sketch, "E27.56.31.0", {"center": v(-12.6, -22) * mm, "radius": 1 * mm});
            skCircle(sketch, "E27.58.31.0", {"center": v(-26.1, -20.5) * mm, "radius": 1 * mm});
            skCircle(sketch, "E27.60.31.0", {"center": v(-8.1, -20.5) * mm, "radius": 1 * mm});
            skCircle(sketch, "E27.62.31.0", {"center": v(-27.6, -22) * mm, "radius": 1 * mm});
            skCircle(sketch, "E27.64.31.0", {"center": v(-29.1, -20.5) * mm, "radius": 1 * mm});
            skCircle(sketch, "E27.66.31.0", {"center": v(15.9, -20.5) * mm, "radius": 1 * mm});
            skCircle(sketch, "E27.68.31.0", {"center": v(-3.6, -22) * mm, "radius": 1 * mm});
            skCircle(sketch, "E27.70.31.0", {"center": v(-11.1, -20.5) * mm, "radius": 1 * mm});
            skCircle(sketch, "E27.72.31.0", {"center": v(44.4, -22) * mm, "radius": 1 * mm});
            skCircle(sketch, "E27.74.31.0", {"center": v(8.4, -22) * mm, "radius": 1 * mm});
            skCircle(sketch, "E27.76.31.0", {"center": v(33.9, -20.5) * mm, "radius": 1 * mm});
            skCircle(sketch, "E27.78.31.0", {"center": v(12.9, -20.5) * mm, "radius": 1 * mm});
            skCircle(sketch, "E27.80.31.0", {"center": v(-38.1, -20.5) * mm, "radius": 1 * mm});
            skCircle(sketch, "E27.82.31.0", {"center": v(-18.6, -22) * mm, "radius": 1 * mm});
            skCircle(sketch, "E27.84.31.0", {"center": v(-17.1, -20.5) * mm, "radius": 1 * mm});
            skCircle(sketch, "E27.86.31.0", {"center": v(48.9, -20.5) * mm, "radius": 1 * mm});
            skCircle(sketch, "E27.88.31.0", {"center": v(35.4, -22) * mm, "radius": 1 * mm});
            skCircle(sketch, "E27.90.31.0", {"center": v(11.4, -22) * mm, "radius": 1 * mm});
            skCircle(sketch, "E27.92.31.0", {"center": v(-24.6, -22) * mm, "radius": 1 * mm});
            skCircle(sketch, "E27.94.31.0", {"center": v(21.9, -20.5) * mm, "radius": 1 * mm});
            skCircle(sketch, "E27.96.31.0", {"center": v(50.4, -22) * mm, "radius": 1 * mm});
            skCircle(sketch, "E27.98.31.0", {"center": v(26.4, -22) * mm, "radius": 1 * mm});
            skCircle(sketch, "E27.100.31.0", {"center": v(20.4, -22) * mm, "radius": 1 * mm});
            skCircle(sketch, "E27.102.31.0", {"center": v(39.9, -20.5) * mm, "radius": 1 * mm});
            skCircle(sketch, "E27.104.31.0", {"center": v(-0.6, -22) * mm, "radius": 1 * mm});
            skCircle(sketch, "E27.106.31.0", {"center": v(47.4, -22) * mm, "radius": 1 * mm});
            skCircle(sketch, "E27.110.31.0", {"center": v(-39.6, -22) * mm, "radius": 1 * mm});
            skCircle(sketch, "E27.112.31.0", {"center": v(38.4, -22) * mm, "radius": 1 * mm});
            skCircle(sketch, "E27.114.31.0", {"center": v(-35.1, -20.5) * mm, "radius": 1 * mm});
            skCircle(sketch, "E27.116.31.0", {"center": v(17.4, -22) * mm, "radius": 1 * mm});
            skCircle(sketch, "E27.118.31.0", {"center": v(51.9, -20.5) * mm, "radius": 1 * mm});
            skCircle(sketch, "E27.120.31.0", {"center": v(-33.6, -22) * mm, "radius": 1 * mm});
            skCircle(sketch, "E27.124.31.0", {"center": v(-15.6, -22) * mm, "radius": 1 * mm});
            skCircle(sketch, "E27.126.31.0", {"center": v(14.4, -22) * mm, "radius": 1 * mm});
            skCircle(sketch, "E27.128.31.0", {"center": v(45.9, -20.5) * mm, "radius": 1 * mm});
            skCircle(sketch, "E27.130.31.0", {"center": v(-6.6, -22) * mm, "radius": 1 * mm});
            skCircle(sketch, "E27.132.31.0", {"center": v(32.4, -22) * mm, "radius": 1 * mm});
            skCircle(sketch, "E27.134.31.0", {"center": v(-21.6, -22) * mm, "radius": 1 * mm});
            skCircle(sketch, "E27.136.31.0", {"center": v(6.9, -20.5) * mm, "radius": 1 * mm});
            skCircle(sketch, "E27.138.31.0", {"center": v(-20.1, -20.5) * mm, "radius": 1 * mm});
            skCircle(sketch, "E27.140.31.0", {"center": v(-41.1, -20.5) * mm, "radius": 1 * mm});
            skCircle(sketch, "E27.144.31.0", {"center": v(-47.1, -20.5) * mm, "radius": 1 * mm});
            skCircle(sketch, "E27.146.31.0", {"center": v(-42.6, -22) * mm, "radius": 1 * mm});
            skCircle(sketch, "E27.148.31.0", {"center": v(-45.6, -22) * mm, "radius": 1 * mm});
            skCircle(sketch, "E27.150.31.0", {"center": v(-48.6, -22) * mm, "radius": 1 * mm});
            skLineSegment(sketch, "E27.152.31.0", {"start": v(-50.1, -20.5) * mm, "end": v(-50.1, -19.5) * mm, "construction": true});
            skCircle(sketch, "E27.155.31.0", {"center": v(-50.1, -20.5) * mm, "radius": 1 * mm});
            skLineSegment(sketch, "E27.157.31.0", {"start": v(-51.1, -20.5) * mm, "end": v(-50.1, -20.5) * mm, "construction": true});
            skLineSegment(sketch, "E27.160.31.0", {"start": v(-51.1, -22) * mm, "end": v(-48.6, -22) * mm, "construction": true});
            skLineSegment(sketch, "E27.163.31.0", {"start": v(-48.6, -22) * mm, "end": v(-48.6, -19.5) * mm, "construction": true});
            skCircle(sketch, "E27.0.32.0", {"center": v(27.9, -23.5) * mm, "radius": 1 * mm});
            skCircle(sketch, "E27.2.32.0", {"center": v(-32.1, -23.5) * mm, "radius": 1 * mm});
            skCircle(sketch, "E27.4.32.0", {"center": v(36.9, -23.5) * mm, "radius": 1 * mm});
            skCircle(sketch, "E27.6.32.0", {"center": v(3.9, -23.5) * mm, "radius": 1 * mm});
            skCircle(sketch, "E27.8.32.0", {"center": v(54.9, -23.5) * mm, "radius": 1 * mm});
            skCircle(sketch, "E27.10.32.0", {"center": v(53.4, -25) * mm, "radius": 1 * mm});
            skCircle(sketch, "E27.12.32.0", {"center": v(29.4, -25) * mm, "radius": 1 * mm});
            skCircle(sketch, "E27.14.32.0", {"center": v(2.4, -25) * mm, "radius": 1 * mm});
            skCircle(sketch, "E27.18.32.0", {"center": v(18.9, -23.5) * mm, "radius": 1 * mm});
            skCircle(sketch, "E27.20.32.0", {"center": v(-30.6, -25) * mm, "radius": 1 * mm});
            skCircle(sketch, "E27.24.32.0", {"center": v(-44.1, -23.5) * mm, "radius": 1 * mm});
            skCircle(sketch, "E27.26.32.0", {"center": v(30.9, -23.5) * mm, "radius": 1 * mm});
            skCircle(sketch, "E27.28.32.0", {"center": v(-9.6, -25) * mm, "radius": 1 * mm});
            skCircle(sketch, "E27.32.32.0", {"center": v(-14.1, -23.5) * mm, "radius": 1 * mm});
            skCircle(sketch, "E27.34.32.0", {"center": v(-2.1, -23.5) * mm, "radius": 1 * mm});
            skCircle(sketch, "E27.36.32.0", {"center": v(9.9, -23.5) * mm, "radius": 1 * mm});
            skCircle(sketch, "E27.38.32.0", {"center": v(24.9, -23.5) * mm, "radius": 1 * mm});
            skCircle(sketch, "E27.40.32.0", {"center": v(5.4, -25) * mm, "radius": 1 * mm});
            skCircle(sketch, "E27.42.32.0", {"center": v(-23.1, -23.5) * mm, "radius": 1 * mm});
            skCircle(sketch, "E27.44.32.0", {"center": v(-5.1, -23.5) * mm, "radius": 1 * mm});
            skCircle(sketch, "E27.46.32.0", {"center": v(23.4, -25) * mm, "radius": 1 * mm});
            skCircle(sketch, "E27.48.32.0", {"center": v(42.9, -23.5) * mm, "radius": 1 * mm});
            skCircle(sketch, "E27.50.32.0", {"center": v(0.9, -23.5) * mm, "radius": 1 * mm});
            skCircle(sketch, "E27.52.32.0", {"center": v(-36.6, -25) * mm, "radius": 1 * mm});
            skCircle(sketch, "E27.54.32.0", {"center": v(41.4, -25) * mm, "radius": 1 * mm});
            skCircle(sketch, "E27.56.32.0", {"center": v(-12.6, -25) * mm, "radius": 1 * mm});
            skCircle(sketch, "E27.58.32.0", {"center": v(-26.1, -23.5) * mm, "radius": 1 * mm});
            skCircle(sketch, "E27.60.32.0", {"center": v(-8.1, -23.5) * mm, "radius": 1 * mm});
            skCircle(sketch, "E27.62.32.0", {"center": v(-27.6, -25) * mm, "radius": 1 * mm});
            skCircle(sketch, "E27.64.32.0", {"center": v(-29.1, -23.5) * mm, "radius": 1 * mm});
            skCircle(sketch, "E27.66.32.0", {"center": v(15.9, -23.5) * mm, "radius": 1 * mm});
            skCircle(sketch, "E27.68.32.0", {"center": v(-3.6, -25) * mm, "radius": 1 * mm});
            skCircle(sketch, "E27.70.32.0", {"center": v(-11.1, -23.5) * mm, "radius": 1 * mm});
            skCircle(sketch, "E27.72.32.0", {"center": v(44.4, -25) * mm, "radius": 1 * mm});
            skCircle(sketch, "E27.74.32.0", {"center": v(8.4, -25) * mm, "radius": 1 * mm});
            skCircle(sketch, "E27.76.32.0", {"center": v(33.9, -23.5) * mm, "radius": 1 * mm});
            skCircle(sketch, "E27.78.32.0", {"center": v(12.9, -23.5) * mm, "radius": 1 * mm});
            skCircle(sketch, "E27.80.32.0", {"center": v(-38.1, -23.5) * mm, "radius": 1 * mm});
            skCircle(sketch, "E27.82.32.0", {"center": v(-18.6, -25) * mm, "radius": 1 * mm});
            skCircle(sketch, "E27.84.32.0", {"center": v(-17.1, -23.5) * mm, "radius": 1 * mm});
            skCircle(sketch, "E27.86.32.0", {"center": v(48.9, -23.5) * mm, "radius": 1 * mm});
            skCircle(sketch, "E27.88.32.0", {"center": v(35.4, -25) * mm, "radius": 1 * mm});
            skCircle(sketch, "E27.90.32.0", {"center": v(11.4, -25) * mm, "radius": 1 * mm});
            skCircle(sketch, "E27.92.32.0", {"center": v(-24.6, -25) * mm, "radius": 1 * mm});
            skCircle(sketch, "E27.94.32.0", {"center": v(21.9, -23.5) * mm, "radius": 1 * mm});
            skCircle(sketch, "E27.96.32.0", {"center": v(50.4, -25) * mm, "radius": 1 * mm});
            skCircle(sketch, "E27.98.32.0", {"center": v(26.4, -25) * mm, "radius": 1 * mm});
            skCircle(sketch, "E27.100.32.0", {"center": v(20.4, -25) * mm, "radius": 1 * mm});
            skCircle(sketch, "E27.102.32.0", {"center": v(39.9, -23.5) * mm, "radius": 1 * mm});
            skCircle(sketch, "E27.104.32.0", {"center": v(-0.6, -25) * mm, "radius": 1 * mm});
            skCircle(sketch, "E27.106.32.0", {"center": v(47.4, -25) * mm, "radius": 1 * mm});
            skCircle(sketch, "E27.110.32.0", {"center": v(-39.6, -25) * mm, "radius": 1 * mm});
            skCircle(sketch, "E27.112.32.0", {"center": v(38.4, -25) * mm, "radius": 1 * mm});
            skCircle(sketch, "E27.114.32.0", {"center": v(-35.1, -23.5) * mm, "radius": 1 * mm});
            skCircle(sketch, "E27.116.32.0", {"center": v(17.4, -25) * mm, "radius": 1 * mm});
            skCircle(sketch, "E27.118.32.0", {"center": v(51.9, -23.5) * mm, "radius": 1 * mm});
            skCircle(sketch, "E27.120.32.0", {"center": v(-33.6, -25) * mm, "radius": 1 * mm});
            skCircle(sketch, "E27.124.32.0", {"center": v(-15.6, -25) * mm, "radius": 1 * mm});
            skCircle(sketch, "E27.126.32.0", {"center": v(14.4, -25) * mm, "radius": 1 * mm});
            skCircle(sketch, "E27.128.32.0", {"center": v(45.9, -23.5) * mm, "radius": 1 * mm});
            skCircle(sketch, "E27.130.32.0", {"center": v(-6.6, -25) * mm, "radius": 1 * mm});
            skCircle(sketch, "E27.132.32.0", {"center": v(32.4, -25) * mm, "radius": 1 * mm});
            skCircle(sketch, "E27.134.32.0", {"center": v(-21.6, -25) * mm, "radius": 1 * mm});
            skCircle(sketch, "E27.136.32.0", {"center": v(6.9, -23.5) * mm, "radius": 1 * mm});
            skCircle(sketch, "E27.138.32.0", {"center": v(-20.1, -23.5) * mm, "radius": 1 * mm});
            skCircle(sketch, "E27.140.32.0", {"center": v(-41.1, -23.5) * mm, "radius": 1 * mm});
            skCircle(sketch, "E27.144.32.0", {"center": v(-47.1, -23.5) * mm, "radius": 1 * mm});
            skCircle(sketch, "E27.146.32.0", {"center": v(-42.6, -25) * mm, "radius": 1 * mm});
            skCircle(sketch, "E27.148.32.0", {"center": v(-45.6, -25) * mm, "radius": 1 * mm});
            skCircle(sketch, "E27.150.32.0", {"center": v(-48.6, -25) * mm, "radius": 1 * mm});
            skLineSegment(sketch, "E27.152.32.0", {"start": v(-50.1, -23.5) * mm, "end": v(-50.1, -22.5) * mm, "construction": true});
            skCircle(sketch, "E27.155.32.0", {"center": v(-50.1, -23.5) * mm, "radius": 1 * mm});
            skLineSegment(sketch, "E27.157.32.0", {"start": v(-51.1, -23.5) * mm, "end": v(-50.1, -23.5) * mm, "construction": true});
            skLineSegment(sketch, "E27.160.32.0", {"start": v(-51.1, -25) * mm, "end": v(-48.6, -25) * mm, "construction": true});
            skLineSegment(sketch, "E27.163.32.0", {"start": v(-48.6, -25) * mm, "end": v(-48.6, -22.5) * mm, "construction": true});
            skCircle(sketch, "E27.0.33.0", {"center": v(27.9, -26.5) * mm, "radius": 1 * mm});
            skCircle(sketch, "E27.2.33.0", {"center": v(-32.1, -26.5) * mm, "radius": 1 * mm});
            skCircle(sketch, "E27.4.33.0", {"center": v(36.9, -26.5) * mm, "radius": 1 * mm});
            skCircle(sketch, "E27.6.33.0", {"center": v(3.9, -26.5) * mm, "radius": 1 * mm});
            skCircle(sketch, "E27.8.33.0", {"center": v(54.9, -26.5) * mm, "radius": 1 * mm});
            skCircle(sketch, "E27.10.33.0", {"center": v(53.4, -28) * mm, "radius": 1 * mm});
            skCircle(sketch, "E27.12.33.0", {"center": v(29.4, -28) * mm, "radius": 1 * mm});
            skCircle(sketch, "E27.14.33.0", {"center": v(2.4, -28) * mm, "radius": 1 * mm});
            skCircle(sketch, "E27.18.33.0", {"center": v(18.9, -26.5) * mm, "radius": 1 * mm});
            skCircle(sketch, "E27.20.33.0", {"center": v(-30.6, -28) * mm, "radius": 1 * mm});
            skCircle(sketch, "E27.24.33.0", {"center": v(-44.1, -26.5) * mm, "radius": 1 * mm});
            skCircle(sketch, "E27.26.33.0", {"center": v(30.9, -26.5) * mm, "radius": 1 * mm});
            skCircle(sketch, "E27.28.33.0", {"center": v(-9.6, -28) * mm, "radius": 1 * mm});
            skCircle(sketch, "E27.32.33.0", {"center": v(-14.1, -26.5) * mm, "radius": 1 * mm});
            skCircle(sketch, "E27.34.33.0", {"center": v(-2.1, -26.5) * mm, "radius": 1 * mm});
            skCircle(sketch, "E27.36.33.0", {"center": v(9.9, -26.5) * mm, "radius": 1 * mm});
            skCircle(sketch, "E27.38.33.0", {"center": v(24.9, -26.5) * mm, "radius": 1 * mm});
            skCircle(sketch, "E27.40.33.0", {"center": v(5.4, -28) * mm, "radius": 1 * mm});
            skCircle(sketch, "E27.42.33.0", {"center": v(-23.1, -26.5) * mm, "radius": 1 * mm});
            skCircle(sketch, "E27.44.33.0", {"center": v(-5.1, -26.5) * mm, "radius": 1 * mm});
            skCircle(sketch, "E27.46.33.0", {"center": v(23.4, -28) * mm, "radius": 1 * mm});
            skCircle(sketch, "E27.48.33.0", {"center": v(42.9, -26.5) * mm, "radius": 1 * mm});
            skCircle(sketch, "E27.50.33.0", {"center": v(0.9, -26.5) * mm, "radius": 1 * mm});
            skCircle(sketch, "E27.52.33.0", {"center": v(-36.6, -28) * mm, "radius": 1 * mm});
            skCircle(sketch, "E27.54.33.0", {"center": v(41.4, -28) * mm, "radius": 1 * mm});
            skCircle(sketch, "E27.56.33.0", {"center": v(-12.6, -28) * mm, "radius": 1 * mm});
            skCircle(sketch, "E27.58.33.0", {"center": v(-26.1, -26.5) * mm, "radius": 1 * mm});
            skCircle(sketch, "E27.60.33.0", {"center": v(-8.1, -26.5) * mm, "radius": 1 * mm});
            skCircle(sketch, "E27.62.33.0", {"center": v(-27.6, -28) * mm, "radius": 1 * mm});
            skCircle(sketch, "E27.64.33.0", {"center": v(-29.1, -26.5) * mm, "radius": 1 * mm});
            skCircle(sketch, "E27.66.33.0", {"center": v(15.9, -26.5) * mm, "radius": 1 * mm});
            skCircle(sketch, "E27.68.33.0", {"center": v(-3.6, -28) * mm, "radius": 1 * mm});
            skCircle(sketch, "E27.70.33.0", {"center": v(-11.1, -26.5) * mm, "radius": 1 * mm});
            skCircle(sketch, "E27.72.33.0", {"center": v(44.4, -28) * mm, "radius": 1 * mm});
            skCircle(sketch, "E27.74.33.0", {"center": v(8.4, -28) * mm, "radius": 1 * mm});
            skCircle(sketch, "E27.76.33.0", {"center": v(33.9, -26.5) * mm, "radius": 1 * mm});
            skCircle(sketch, "E27.78.33.0", {"center": v(12.9, -26.5) * mm, "radius": 1 * mm});
            skCircle(sketch, "E27.80.33.0", {"center": v(-38.1, -26.5) * mm, "radius": 1 * mm});
            skCircle(sketch, "E27.82.33.0", {"center": v(-18.6, -28) * mm, "radius": 1 * mm});
            skCircle(sketch, "E27.84.33.0", {"center": v(-17.1, -26.5) * mm, "radius": 1 * mm});
            skCircle(sketch, "E27.86.33.0", {"center": v(48.9, -26.5) * mm, "radius": 1 * mm});
            skCircle(sketch, "E27.88.33.0", {"center": v(35.4, -28) * mm, "radius": 1 * mm});
            skCircle(sketch, "E27.90.33.0", {"center": v(11.4, -28) * mm, "radius": 1 * mm});
            skCircle(sketch, "E27.92.33.0", {"center": v(-24.6, -28) * mm, "radius": 1 * mm});
            skCircle(sketch, "E27.94.33.0", {"center": v(21.9, -26.5) * mm, "radius": 1 * mm});
            skCircle(sketch, "E27.96.33.0", {"center": v(50.4, -28) * mm, "radius": 1 * mm});
            skCircle(sketch, "E27.98.33.0", {"center": v(26.4, -28) * mm, "radius": 1 * mm});
            skCircle(sketch, "E27.100.33.0", {"center": v(20.4, -28) * mm, "radius": 1 * mm});
            skCircle(sketch, "E27.102.33.0", {"center": v(39.9, -26.5) * mm, "radius": 1 * mm});
            skCircle(sketch, "E27.104.33.0", {"center": v(-0.6, -28) * mm, "radius": 1 * mm});
            skCircle(sketch, "E27.106.33.0", {"center": v(47.4, -28) * mm, "radius": 1 * mm});
            skCircle(sketch, "E27.110.33.0", {"center": v(-39.6, -28) * mm, "radius": 1 * mm});
            skCircle(sketch, "E27.112.33.0", {"center": v(38.4, -28) * mm, "radius": 1 * mm});
            skCircle(sketch, "E27.114.33.0", {"center": v(-35.1, -26.5) * mm, "radius": 1 * mm});
            skCircle(sketch, "E27.116.33.0", {"center": v(17.4, -28) * mm, "radius": 1 * mm});
            skCircle(sketch, "E27.118.33.0", {"center": v(51.9, -26.5) * mm, "radius": 1 * mm});
            skCircle(sketch, "E27.120.33.0", {"center": v(-33.6, -28) * mm, "radius": 1 * mm});
            skCircle(sketch, "E27.124.33.0", {"center": v(-15.6, -28) * mm, "radius": 1 * mm});
            skCircle(sketch, "E27.126.33.0", {"center": v(14.4, -28) * mm, "radius": 1 * mm});
            skCircle(sketch, "E27.128.33.0", {"center": v(45.9, -26.5) * mm, "radius": 1 * mm});
            skCircle(sketch, "E27.130.33.0", {"center": v(-6.6, -28) * mm, "radius": 1 * mm});
            skCircle(sketch, "E27.132.33.0", {"center": v(32.4, -28) * mm, "radius": 1 * mm});
            skCircle(sketch, "E27.134.33.0", {"center": v(-21.6, -28) * mm, "radius": 1 * mm});
            skCircle(sketch, "E27.136.33.0", {"center": v(6.9, -26.5) * mm, "radius": 1 * mm});
            skCircle(sketch, "E27.138.33.0", {"center": v(-20.1, -26.5) * mm, "radius": 1 * mm});
            skCircle(sketch, "E27.140.33.0", {"center": v(-41.1, -26.5) * mm, "radius": 1 * mm});
            skCircle(sketch, "E27.144.33.0", {"center": v(-47.1, -26.5) * mm, "radius": 1 * mm});
            skCircle(sketch, "E27.146.33.0", {"center": v(-42.6, -28) * mm, "radius": 1 * mm});
            skCircle(sketch, "E27.148.33.0", {"center": v(-45.6, -28) * mm, "radius": 1 * mm});
            skCircle(sketch, "E27.150.33.0", {"center": v(-48.6, -28) * mm, "radius": 1 * mm});
            skLineSegment(sketch, "E27.152.33.0", {"start": v(-50.1, -26.5) * mm, "end": v(-50.1, -25.5) * mm, "construction": true});
            skCircle(sketch, "E27.155.33.0", {"center": v(-50.1, -26.5) * mm, "radius": 1 * mm});
            skLineSegment(sketch, "E27.157.33.0", {"start": v(-51.1, -26.5) * mm, "end": v(-50.1, -26.5) * mm, "construction": true});
            skLineSegment(sketch, "E27.160.33.0", {"start": v(-51.1, -28) * mm, "end": v(-48.6, -28) * mm, "construction": true});
            skLineSegment(sketch, "E27.163.33.0", {"start": v(-48.6, -28) * mm, "end": v(-48.6, -25.5) * mm, "construction": true});
            skCircle(sketch, "E27.0.34.0", {"center": v(27.9, -29.5) * mm, "radius": 1 * mm});
            skCircle(sketch, "E27.2.34.0", {"center": v(-32.1, -29.5) * mm, "radius": 1 * mm});
            skCircle(sketch, "E27.4.34.0", {"center": v(36.9, -29.5) * mm, "radius": 1 * mm});
            skCircle(sketch, "E27.6.34.0", {"center": v(3.9, -29.5) * mm, "radius": 1 * mm});
            skCircle(sketch, "E27.8.34.0", {"center": v(54.9, -29.5) * mm, "radius": 1 * mm});
            skCircle(sketch, "E27.10.34.0", {"center": v(53.4, -31) * mm, "radius": 1 * mm});
            skCircle(sketch, "E27.12.34.0", {"center": v(29.4, -31) * mm, "radius": 1 * mm});
            skCircle(sketch, "E27.14.34.0", {"center": v(2.4, -31) * mm, "radius": 1 * mm});
            skCircle(sketch, "E27.18.34.0", {"center": v(18.9, -29.5) * mm, "radius": 1 * mm});
            skCircle(sketch, "E27.20.34.0", {"center": v(-30.6, -31) * mm, "radius": 1 * mm});
            skCircle(sketch, "E27.24.34.0", {"center": v(-44.1, -29.5) * mm, "radius": 1 * mm});
            skCircle(sketch, "E27.26.34.0", {"center": v(30.9, -29.5) * mm, "radius": 1 * mm});
            skCircle(sketch, "E27.28.34.0", {"center": v(-9.6, -31) * mm, "radius": 1 * mm});
            skCircle(sketch, "E27.32.34.0", {"center": v(-14.1, -29.5) * mm, "radius": 1 * mm});
            skCircle(sketch, "E27.34.34.0", {"center": v(-2.1, -29.5) * mm, "radius": 1 * mm});
            skCircle(sketch, "E27.36.34.0", {"center": v(9.9, -29.5) * mm, "radius": 1 * mm});
            skCircle(sketch, "E27.38.34.0", {"center": v(24.9, -29.5) * mm, "radius": 1 * mm});
            skCircle(sketch, "E27.40.34.0", {"center": v(5.4, -31) * mm, "radius": 1 * mm});
            skCircle(sketch, "E27.42.34.0", {"center": v(-23.1, -29.5) * mm, "radius": 1 * mm});
            skCircle(sketch, "E27.44.34.0", {"center": v(-5.1, -29.5) * mm, "radius": 1 * mm});
            skCircle(sketch, "E27.46.34.0", {"center": v(23.4, -31) * mm, "radius": 1 * mm});
            skCircle(sketch, "E27.48.34.0", {"center": v(42.9, -29.5) * mm, "radius": 1 * mm});
            skCircle(sketch, "E27.50.34.0", {"center": v(0.9, -29.5) * mm, "radius": 1 * mm});
            skCircle(sketch, "E27.52.34.0", {"center": v(-36.6, -31) * mm, "radius": 1 * mm});
            skCircle(sketch, "E27.54.34.0", {"center": v(41.4, -31) * mm, "radius": 1 * mm});
            skCircle(sketch, "E27.56.34.0", {"center": v(-12.6, -31) * mm, "radius": 1 * mm});
            skCircle(sketch, "E27.58.34.0", {"center": v(-26.1, -29.5) * mm, "radius": 1 * mm});
            skCircle(sketch, "E27.60.34.0", {"center": v(-8.1, -29.5) * mm, "radius": 1 * mm});
            skCircle(sketch, "E27.62.34.0", {"center": v(-27.6, -31) * mm, "radius": 1 * mm});
            skCircle(sketch, "E27.64.34.0", {"center": v(-29.1, -29.5) * mm, "radius": 1 * mm});
            skCircle(sketch, "E27.66.34.0", {"center": v(15.9, -29.5) * mm, "radius": 1 * mm});
            skCircle(sketch, "E27.68.34.0", {"center": v(-3.6, -31) * mm, "radius": 1 * mm});
            skCircle(sketch, "E27.70.34.0", {"center": v(-11.1, -29.5) * mm, "radius": 1 * mm});
            skCircle(sketch, "E27.72.34.0", {"center": v(44.4, -31) * mm, "radius": 1 * mm});
            skCircle(sketch, "E27.74.34.0", {"center": v(8.4, -31) * mm, "radius": 1 * mm});
            skCircle(sketch, "E27.76.34.0", {"center": v(33.9, -29.5) * mm, "radius": 1 * mm});
            skCircle(sketch, "E27.78.34.0", {"center": v(12.9, -29.5) * mm, "radius": 1 * mm});
            skCircle(sketch, "E27.80.34.0", {"center": v(-38.1, -29.5) * mm, "radius": 1 * mm});
            skCircle(sketch, "E27.82.34.0", {"center": v(-18.6, -31) * mm, "radius": 1 * mm});
            skCircle(sketch, "E27.84.34.0", {"center": v(-17.1, -29.5) * mm, "radius": 1 * mm});
            skCircle(sketch, "E27.86.34.0", {"center": v(48.9, -29.5) * mm, "radius": 1 * mm});
            skCircle(sketch, "E27.88.34.0", {"center": v(35.4, -31) * mm, "radius": 1 * mm});
            skCircle(sketch, "E27.90.34.0", {"center": v(11.4, -31) * mm, "radius": 1 * mm});
            skCircle(sketch, "E27.92.34.0", {"center": v(-24.6, -31) * mm, "radius": 1 * mm});
            skCircle(sketch, "E27.94.34.0", {"center": v(21.9, -29.5) * mm, "radius": 1 * mm});
            skCircle(sketch, "E27.96.34.0", {"center": v(50.4, -31) * mm, "radius": 1 * mm});
            skCircle(sketch, "E27.98.34.0", {"center": v(26.4, -31) * mm, "radius": 1 * mm});
            skCircle(sketch, "E27.100.34.0", {"center": v(20.4, -31) * mm, "radius": 1 * mm});
            skCircle(sketch, "E27.102.34.0", {"center": v(39.9, -29.5) * mm, "radius": 1 * mm});
            skCircle(sketch, "E27.104.34.0", {"center": v(-0.6, -31) * mm, "radius": 1 * mm});
            skCircle(sketch, "E27.106.34.0", {"center": v(47.4, -31) * mm, "radius": 1 * mm});
            skCircle(sketch, "E27.110.34.0", {"center": v(-39.6, -31) * mm, "radius": 1 * mm});
            skCircle(sketch, "E27.112.34.0", {"center": v(38.4, -31) * mm, "radius": 1 * mm});
            skCircle(sketch, "E27.114.34.0", {"center": v(-35.1, -29.5) * mm, "radius": 1 * mm});
            skCircle(sketch, "E27.116.34.0", {"center": v(17.4, -31) * mm, "radius": 1 * mm});
            skCircle(sketch, "E27.118.34.0", {"center": v(51.9, -29.5) * mm, "radius": 1 * mm});
            skCircle(sketch, "E27.120.34.0", {"center": v(-33.6, -31) * mm, "radius": 1 * mm});
            skCircle(sketch, "E27.124.34.0", {"center": v(-15.6, -31) * mm, "radius": 1 * mm});
            skCircle(sketch, "E27.126.34.0", {"center": v(14.4, -31) * mm, "radius": 1 * mm});
            skCircle(sketch, "E27.128.34.0", {"center": v(45.9, -29.5) * mm, "radius": 1 * mm});
            skCircle(sketch, "E27.130.34.0", {"center": v(-6.6, -31) * mm, "radius": 1 * mm});
            skCircle(sketch, "E27.132.34.0", {"center": v(32.4, -31) * mm, "radius": 1 * mm});
            skCircle(sketch, "E27.134.34.0", {"center": v(-21.6, -31) * mm, "radius": 1 * mm});
            skCircle(sketch, "E27.136.34.0", {"center": v(6.9, -29.5) * mm, "radius": 1 * mm});
            skCircle(sketch, "E27.138.34.0", {"center": v(-20.1, -29.5) * mm, "radius": 1 * mm});
            skCircle(sketch, "E27.140.34.0", {"center": v(-41.1, -29.5) * mm, "radius": 1 * mm});
            skCircle(sketch, "E27.144.34.0", {"center": v(-47.1, -29.5) * mm, "radius": 1 * mm});
            skCircle(sketch, "E27.146.34.0", {"center": v(-42.6, -31) * mm, "radius": 1 * mm});
            skCircle(sketch, "E27.148.34.0", {"center": v(-45.6, -31) * mm, "radius": 1 * mm});
            skCircle(sketch, "E27.150.34.0", {"center": v(-48.6, -31) * mm, "radius": 1 * mm});
            skLineSegment(sketch, "E27.152.34.0", {"start": v(-50.1, -29.5) * mm, "end": v(-50.1, -28.5) * mm, "construction": true});
            skCircle(sketch, "E27.155.34.0", {"center": v(-50.1, -29.5) * mm, "radius": 1 * mm});
            skLineSegment(sketch, "E27.157.34.0", {"start": v(-51.1, -29.5) * mm, "end": v(-50.1, -29.5) * mm, "construction": true});
            skLineSegment(sketch, "E27.160.34.0", {"start": v(-51.1, -31) * mm, "end": v(-48.6, -31) * mm, "construction": true});
            skLineSegment(sketch, "E27.163.34.0", {"start": v(-48.6, -31) * mm, "end": v(-48.6, -28.5) * mm, "construction": true});
            skCircle(sketch, "E27.0.35.0", {"center": v(27.9, -32.5) * mm, "radius": 1 * mm});
            skCircle(sketch, "E27.2.35.0", {"center": v(-32.1, -32.5) * mm, "radius": 1 * mm});
            skCircle(sketch, "E27.4.35.0", {"center": v(36.9, -32.5) * mm, "radius": 1 * mm});
            skCircle(sketch, "E27.6.35.0", {"center": v(3.9, -32.5) * mm, "radius": 1 * mm});
            skCircle(sketch, "E27.8.35.0", {"center": v(54.9, -32.5) * mm, "radius": 1 * mm});
            skCircle(sketch, "E27.18.35.0", {"center": v(18.9, -32.5) * mm, "radius": 1 * mm});
            skCircle(sketch, "E27.24.35.0", {"center": v(-44.1, -32.5) * mm, "radius": 1 * mm});
            skCircle(sketch, "E27.26.35.0", {"center": v(30.9, -32.5) * mm, "radius": 1 * mm});
            skCircle(sketch, "E27.32.35.0", {"center": v(-14.1, -32.5) * mm, "radius": 1 * mm});
            skCircle(sketch, "E27.34.35.0", {"center": v(-2.1, -32.5) * mm, "radius": 1 * mm});
            skCircle(sketch, "E27.36.35.0", {"center": v(9.9, -32.5) * mm, "radius": 1 * mm});
            skCircle(sketch, "E27.38.35.0", {"center": v(24.9, -32.5) * mm, "radius": 1 * mm});
            skCircle(sketch, "E27.42.35.0", {"center": v(-23.1, -32.5) * mm, "radius": 1 * mm});
            skCircle(sketch, "E27.44.35.0", {"center": v(-5.1, -32.5) * mm, "radius": 1 * mm});
            skCircle(sketch, "E27.48.35.0", {"center": v(42.9, -32.5) * mm, "radius": 1 * mm});
            skCircle(sketch, "E27.50.35.0", {"center": v(0.9, -32.5) * mm, "radius": 1 * mm});
            skCircle(sketch, "E27.58.35.0", {"center": v(-26.1, -32.5) * mm, "radius": 1 * mm});
            skCircle(sketch, "E27.60.35.0", {"center": v(-8.1, -32.5) * mm, "radius": 1 * mm});
            skCircle(sketch, "E27.64.35.0", {"center": v(-29.1, -32.5) * mm, "radius": 1 * mm});
            skCircle(sketch, "E27.66.35.0", {"center": v(15.9, -32.5) * mm, "radius": 1 * mm});
            skCircle(sketch, "E27.70.35.0", {"center": v(-11.1, -32.5) * mm, "radius": 1 * mm});
            skCircle(sketch, "E27.76.35.0", {"center": v(33.9, -32.5) * mm, "radius": 1 * mm});
            skCircle(sketch, "E27.78.35.0", {"center": v(12.9, -32.5) * mm, "radius": 1 * mm});
            skCircle(sketch, "E27.80.35.0", {"center": v(-38.1, -32.5) * mm, "radius": 1 * mm});
            skCircle(sketch, "E27.84.35.0", {"center": v(-17.1, -32.5) * mm, "radius": 1 * mm});
            skCircle(sketch, "E27.86.35.0", {"center": v(48.9, -32.5) * mm, "radius": 1 * mm});
            skCircle(sketch, "E27.94.35.0", {"center": v(21.9, -32.5) * mm, "radius": 1 * mm});
            skCircle(sketch, "E27.102.35.0", {"center": v(39.9, -32.5) * mm, "radius": 1 * mm});
            skCircle(sketch, "E27.114.35.0", {"center": v(-35.1, -32.5) * mm, "radius": 1 * mm});
            skCircle(sketch, "E27.118.35.0", {"center": v(51.9, -32.5) * mm, "radius": 1 * mm});
            skCircle(sketch, "E27.128.35.0", {"center": v(45.9, -32.5) * mm, "radius": 1 * mm});
            skCircle(sketch, "E27.136.35.0", {"center": v(6.9, -32.5) * mm, "radius": 1 * mm});
            skCircle(sketch, "E27.138.35.0", {"center": v(-20.1, -32.5) * mm, "radius": 1 * mm});
            skCircle(sketch, "E27.140.35.0", {"center": v(-41.1, -32.5) * mm, "radius": 1 * mm});
            skCircle(sketch, "E27.144.35.0", {"center": v(-47.1, -32.5) * mm, "radius": 1 * mm});
            skLineSegment(sketch, "E27.152.35.0", {"start": v(-50.1, -32.5) * mm, "end": v(-50.1, -31.5) * mm, "construction": true});
            skCircle(sketch, "E27.155.35.0", {"center": v(-50.1, -32.5) * mm, "radius": 1 * mm});
            skLineSegment(sketch, "E27.157.35.0", {"start": v(-51.1, -32.5) * mm, "end": v(-50.1, -32.5) * mm, "construction": true});
            skLineSegment(sketch, "E27.160.35.0", {"start": v(-51.1, -34) * mm, "end": v(-48.6, -34) * mm, "construction": true});
            skLineSegment(sketch, "E27.163.35.0", {"start": v(-48.6, -34) * mm, "end": v(-48.6, -31.5) * mm, "construction": true});
            skSolve(sketch);
        }
        {
            var Q0;
            Q0 = qSketchRegion(id + "F10", true);
            extrude(context, id + "F11", {"entities" : qUnion([Q0]), "operationType" : NewBodyOperationType.REMOVE, "oppositeDirection" : true, "depth" : 5 * mm, "offsetDistance" : 25 * mm});
        }
    });
